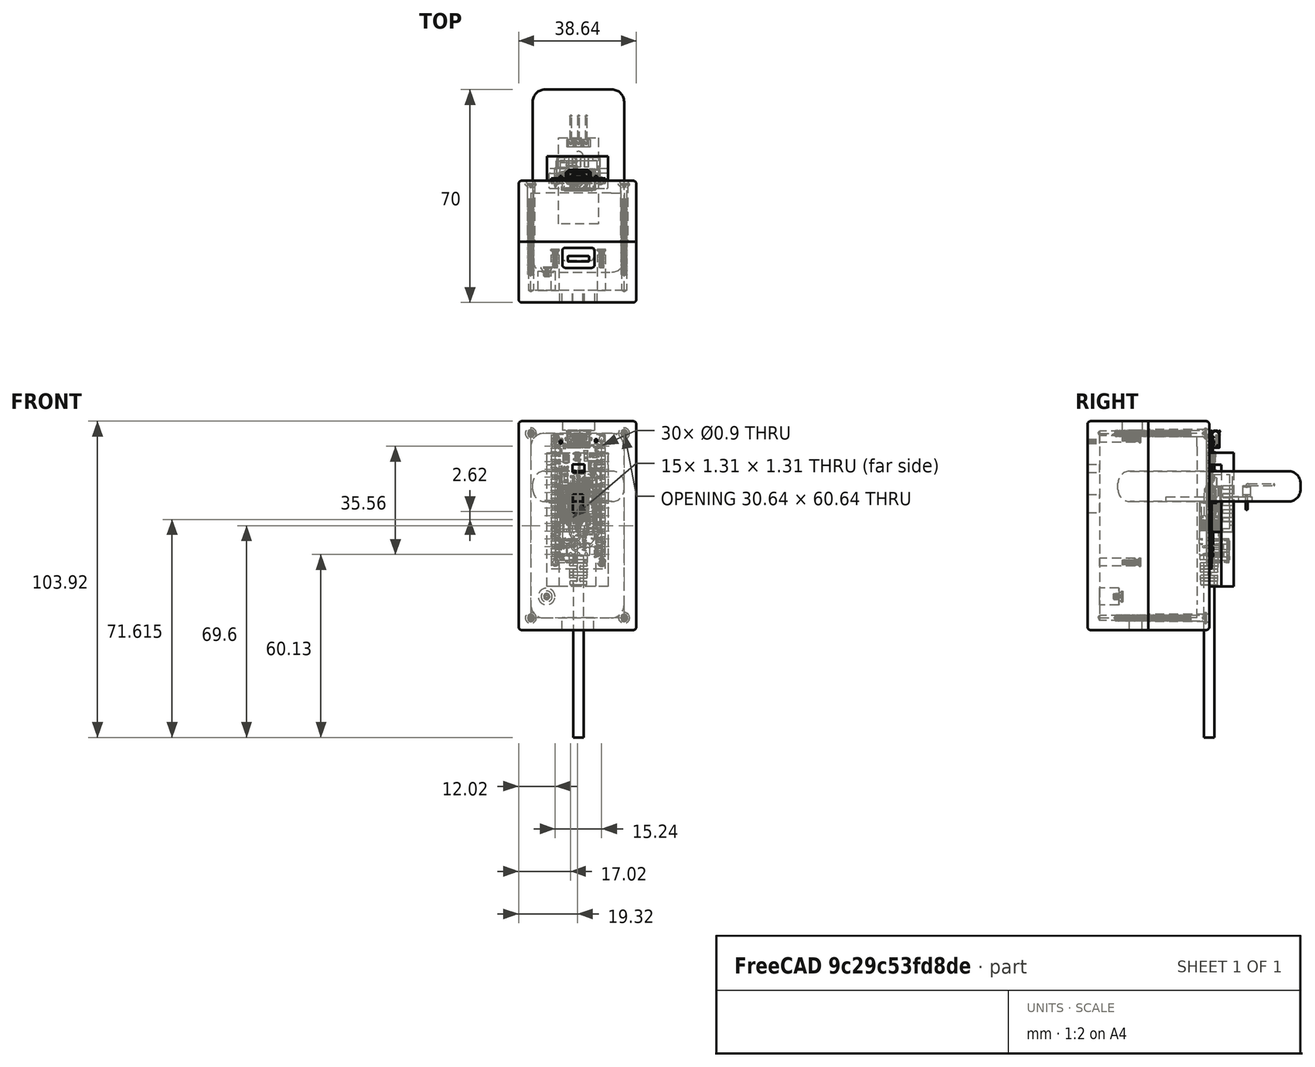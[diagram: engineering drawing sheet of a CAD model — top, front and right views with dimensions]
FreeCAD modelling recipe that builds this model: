
FCSTD DOCUMENT  (FreeCAD 1.0RUnknown)
Label: iot_assembly
License: All rights reserved
LicenseURL: https://en.wikipedia.org/wiki/All_rights_reserved
objects: TechDraw::DrawViewDimension×105, Part::Feature×69, Sketcher::SketchObject×21, App::FeaturePython×18, TechDraw::DrawProjGroupItem×18, App::Part×14, PartDesign::Pad×11, TechDraw::DrawViewDetail×10, TechDraw::DrawViewBalloon×9, Part::FeaturePython×7, PartDesign::SubShapeBinder×6, PartDesign::Pocket×6, PartDesign::Fillet×5, TechDraw::DrawViewSection×5, Spreadsheet::Sheet×4, PartDesign::Hole×4, Assembly::JointGroup×3, Assembly::AssemblyObject×3, PartDesign::Body×3, TechDraw::DrawSVGTemplate×3, +7 more types
note: 411 computed .brp shape members not serialized (recipe doc carries the construction recipe); baked Part::Feature solids carry a one-line shape summary decoded from their .brp

FEATURE [Part::Feature] Part__Feature  label="Nano_33IoT Body"
  shape: bbox 17.78 x 1.75 x 44 mm, 2561 faces (baked)
FEATURE [Part::Feature] Part__Feature001  label="User Library-arduino_nano_reset core"
  shape: bbox 5.209 x 2.159 x 2.809 mm, 76 faces (baked)
FEATURE [Part::Feature] Part__Feature002  label="User Library-arduino_nano_reset shell"
  Placement = pos=(1e-16,1.65,-1e-16) rot=(0,-1,0;1.5708rad)
  shape: bbox 4 x 1.65 x 3 mm, 71 faces (baked)
FEATURE [App::Part] Reser_Button  label="Reser Button"
  Group = -> [Part__Feature001,Part__Feature002]
  Origin = -> Origin001
  Placement = pos=(4.5e-15,0.8,10.91) rot=(0,0,1;0rad)
FEATURE [Part::Feature] Part__Feature003  label="atmegaSAMD21"
  Placement = pos=(-1.21,0.82,-0.24) rot=(0,1,0;1.5708rad)
  shape: bbox 7.242 x 1.032 x 7.242 mm, 984 faces (baked)
FEATURE [Part::Feature] Part__Feature004  label="HSMG-C190 LED"
  Placement = pos=(5.79,0.8,19.6) rot=(0,-1,0;1.5708rad)
  shape: bbox 0.8 x 0.8 x 1.6 mm, 18 faces (baked)
FEATURE [Part::Feature] Part__Feature005  label="HSMG-C190 LED001"
  Placement = pos=(-5.81,0.8,20.1) rot=(0,-1,0;1.5708rad)
  shape: bbox 0.8 x 0.8 x 1.6 mm, 18 faces (baked)
FEATURE [Part::Feature] Part__Feature006  label="ZX62-AB-5PA Micro USB"
  Placement = pos=(-4e-16,2.22,19.2) rot=(0,0,1;0rad)
  shape: bbox 8.814 x 3.085 x 5.639 mm, 861 faces (baked)
FEATURE [Part::Feature] Part__Feature007  label="ZX62-AB-5PA Micro USB001"
  Placement = pos=(-4e-16,2.22,19.2) rot=(0,0,1;0rad)
  shape: bbox 2e-07 x 0.3 x 0.3464 mm, 2 faces, 0 solids (baked)
FEATURE [Part::Feature] Part__Feature008  label="ZX62-AB-5PA Micro USB002"
  Placement = pos=(-4e-16,2.22,19.2) rot=(0,0,1;0rad)
  shape: bbox 2e-07 x 0.3 x 0.3464 mm, 2 faces, 0 solids (baked)
FEATURE [Part::Feature] Part__Feature009  label="ZX62-AB-5PA Micro USB003"
  Placement = pos=(-4e-16,2.22,19.2) rot=(0,0,1;0rad)
  shape: bbox 2e-07 x 0.3 x 0.3464 mm, 2 faces, 0 solids (baked)
FEATURE [Part::Feature] Part__Feature010  label="ZX62-AB-5PA Micro USB004"
  Placement = pos=(-4e-16,2.22,19.2) rot=(0,0,1;0rad)
  shape: bbox 2e-07 x 0.3 x 0.3464 mm, 2 faces, 0 solids (baked)
FEATURE [Part::Feature] Part__Feature011  label="ZX62-AB-5PA Micro USB005"
  Placement = pos=(-4e-16,2.22,19.2) rot=(0,0,1;0rad)
  shape: bbox 0.3 x 0.3 x 2e-07 mm, 1 faces, 0 solids (baked)
FEATURE [Part::Feature] Part__Feature012  label="ZX62-AB-5PA Micro USB006"
  Placement = pos=(-4e-16,2.22,19.2) rot=(0,0,1;0rad)
  shape: bbox 0.3 x 0.3 x 2e-07 mm, 1 faces, 0 solids (baked)
FEATURE [App::Part] ZX62_AB_5PA_Micro_USB  label="ZX62-AB-5PA Micro USB007"
  Group = -> [Part__Feature006,Part__Feature007,Part__Feature008,Part__Feature009,Part__Feature010,Part__Feature011,Part__Feature012]
  Origin = -> Origin002
FEATURE [Part::Feature] Part__Feature013  label="LSM6DS3 Accelerometer"
  Placement = pos=(4.6275,0.82,12) rot=(0,1,0;3.14159rad)
  shape: bbox 2.5 x 0.85 x 3 mm, 190 faces (baked)
FEATURE [Part::Feature] Part__Feature014  label="MPM3610 Step-Down Module"
  Placement = pos=(3.69,1.65,6.25) rot=(0,-1,0;1.5708rad)
  shape: bbox 5.15 x 1.65 x 3.3 mm, 330 faces (baked)
FEATURE [Part::Feature] Part__Feature015  label="NINA-W102 Body"
  shape: bbox 14 x 0.85 x 10 mm, 250 faces (baked)
FEATURE [Part::Feature] Part__Feature016  label="NINA-W102 Antenna"
  Placement = pos=(7,0.8,2.2e-15) rot=(0,0,1;0rad)
  shape: bbox 3.8 x 3 x 10 mm, 99 faces (baked)
FEATURE [Part::Feature] Part__Feature017  label="NINA-W102 Cover"
  Placement = pos=(-1.7,2,0) rot=(0,-1,0;1.5708rad)
  shape: bbox 9.6 x 1.45 x 9.5 mm, 75 faces (baked)
FEATURE [App::Part] NINA_W102_Module  label="NINA-W102 Module"
  Group = -> [Part__Feature015,Part__Feature016,Part__Feature017]
  Origin = -> Origin003
  Placement = pos=(2.17e-14,0.85,-14.5) rot=(0,1,0;1.5708rad)
FEATURE [Part::Feature] Part__Feature018  label="ATECC608A No Lead Crypto Auth"
  Placement = pos=(-4.035,0.8,-6.08) rot=(0,1,0;1.5708rad)
  shape: bbox 3.3 x 0.55 x 2 mm, 213 faces (baked)
FEATURE [Part::Feature] Part__Feature019  label="CL21A226MQCLQNC Capacitor"
  Placement = pos=(4.44,1.225,-5.85) rot=(0,1,0;3.14159rad)
  shape: bbox 3 x 0.8705 x 1.25 mm, 52 faces (baked)
FEATURE [Part::Feature] Part__Feature020  label="TDK C1005 Capacitor"
  Placement = pos=(5.5825,1.05,-15.55) rot=(0,1,0;1.5708rad)
  shape: bbox 0.5 x 0.5165 x 1.8 mm, 46 faces (baked)
FEATURE [Part::Feature] Part__Feature021  label="TDK C1005 Capacitor001"
  Placement = pos=(5.5825,1.05,-17.5125) rot=(0,1,0;1.5708rad)
  shape: bbox 0.5 x 0.5165 x 1.8 mm, 46 faces (baked)
FEATURE [Part::Feature] Part__Feature022  label="CL21A226MQCLQNC Capacitor001"
  Placement = pos=(-4.11,1.225,7.8375) rot=(0,-1,0;1.5708rad)
  shape: bbox 1.25 x 0.8705 x 3 mm, 52 faces (baked)
FEATURE [Part::Feature] Part__Feature023  label="TDK C1005 Capacitor002"
  Placement = pos=(5.385,1.05,15.7375) rot=(0,0,1;0rad)
  shape: bbox 1.8 x 0.5165 x 0.5 mm, 46 faces (baked)
FEATURE [Part::Feature] Part__Feature024  label="TDK C1005 Capacitor003"
  Placement = pos=(5.385,1.05,14.7625) rot=(0,0,1;0rad)
  shape: bbox 1.8 x 0.5165 x 0.5 mm, 46 faces (baked)
FEATURE [Part::Feature] Part__Feature025  label="PRTR5V0U2X Protection Diode"
  Placement = pos=(-0.41,1.45,14.77) rot=(0,1,0;1.5708rad)
  shape: bbox 2.5 x 1.1 x 3 mm, 139 faces (baked)
FEATURE [Part::Feature] Part__Feature026  label="PMEG6020AELR Diode"
  Placement = pos=(-4.06,0.85,14.1) rot=(0,-1,0;1.5708rad)
  shape: bbox 1.9 x 1.11 x 3.3 mm, 80 faces (baked)
FEATURE [Part::Feature] Part__Feature027  label="C0805C472KDRACTU Capacitor"
  Placement = pos=(2.415,1.425,15.1325) rot=(0,-1,0;1.5708rad)
  shape: bbox 1.25 x 1.301 x 3.5 mm, 52 faces (baked)
FEATURE [Part::Feature] Part__Feature028  label="TDK C1005 Capacitor004"
  Placement = pos=(-1.52,1.05,-6.46) rot=(0,1,0;1.5708rad)
  shape: bbox 0.5 x 0.5165 x 1.8 mm, 46 faces (baked)
FEATURE [Part::Feature] Part__Feature029  label="BLM18PG471SN1D Ferrite Bead"
  Placement = pos=(0.61,1.2,-6.1) rot=(0,1,0;3.14159rad)
  shape: bbox 2.5 x 0.8142 x 0.8 mm, 52 faces (baked)
FEATURE [Part::Feature] Part__Feature030  label="TDK C1005 Capacitor005"
  Placement = pos=(-5.66,1.05,-4.35) rot=(0,1,0;3.14159rad)
  shape: bbox 1.8 x 0.5165 x 0.5 mm, 46 faces (baked)
FEATURE [Part::Feature] Part__Feature031  label="TDK C1005 Capacitor006"
  Placement = pos=(-3.64,1.05,10.73) rot=(0,-1,0;1.5708rad)
  shape: bbox 0.5 x 0.5165 x 1.8 mm, 46 faces (baked)
FEATURE [Part::Feature] Part__Feature032  label="TDK C1005 Capacitor007"
  Placement = pos=(-3.79,1.05,5.1) rot=(0,0,1;0rad)
  shape: bbox 1.8 x 0.5165 x 0.5 mm, 46 faces (baked)
FEATURE [Part::Feature] Part__Feature033  label="GRM188R61E475KE11D Capacitor"
  Placement = pos=(-5.59,1.2,4.4) rot=(0,-1,0;1.5708rad)
  shape: bbox 0.8 x 0.8142 x 2.5 mm, 52 faces (baked)
FEATURE [Part::Feature] Part__Feature034  label="RC0402FR-07100KL Resistor"
  Placement = pos=(-2.01,1,8.1625) rot=(0,1,0;3.14159rad)
  shape: bbox 1.47 x 0.4379 x 0.5 mm, 68 faces (baked)
FEATURE [Part::Feature] Part__Feature035  label="RC0402FR-07100KL Resistor001"
  Placement = pos=(-1.6975,1,6.7125) rot=(0,-1,0;1.5708rad)
  shape: bbox 0.5 x 0.4379 x 1.47 mm, 68 faces (baked)
FEATURE [Part::Feature] Part__Feature036  label="RC0402FR-07330RL Resistor"
  Placement = pos=(-5.81,1,16.6) rot=(0,-1,0;1.5708rad)
  shape: bbox 0.5 x 0.4379 x 1.47 mm, 68 faces (baked)
FEATURE [Part::Feature] Part__Feature037  label="RC0402FR-07330RL Resistor001"
  Placement = pos=(5.8025,1,17.2) rot=(0,-1,0;1.5708rad)
  shape: bbox 0.5 x 0.4379 x 1.47 mm, 68 faces (baked)
FEATURE [Part::Feature] Part__Feature038  label="RC0402FR-07330RL Resistor002"
  Placement = pos=(3.915,1,15.2325) rot=(0,-1,0;1.5708rad)
  shape: bbox 0.5 x 0.4379 x 1.47 mm, 68 faces (baked)
FEATURE [Part::Feature] Part__Feature039  label="TDK C1005 Capacitor008"
  Placement = pos=(5.09,1.05,3.1) rot=(0,1,0;3.14159rad)
  shape: bbox 1.8 x 0.5165 x 0.5 mm, 46 faces (baked)
FEATURE [Part::Feature] Part__Feature040  label="RC0402FR-074K7L Resistor"
  Placement = pos=(5.09,1,2.1) rot=(0,0,1;0rad)
  shape: bbox 1.47 x 0.4379 x 0.5 mm, 68 faces (baked)
FEATURE [Part::Feature] Part__Feature041  label="RC0402FR-074K7L Resistor001"
  Placement = pos=(5.09,1,1.1) rot=(0,1,0;3.14159rad)
  shape: bbox 1.47 x 0.4379 x 0.5 mm, 68 faces (baked)
FEATURE [Part::Feature] Part__Feature042  label="GRM155R61E105KA12D Capacitor"
  Placement = pos=(5.09,1.05,0.1) rot=(0,0,1;0rad)
  shape: bbox 1.8 x 0.5165 x 0.5 mm, 46 faces (baked)
FEATURE [Part::Feature] Part__Feature043  label="TDK C1005 Capacitor009"
  Placement = pos=(5.09,1.05,-0.9) rot=(0,1,0;3.14159rad)
  shape: bbox 1.8 x 0.5165 x 0.5 mm, 46 faces (baked)
FEATURE [Part::Feature] Part__Feature044  label="RC0402FR-071KL Resistor"
  Placement = pos=(5.09,1,-1.9) rot=(0,1,0;3.14159rad)
  shape: bbox 1.47 x 0.4379 x 0.5 mm, 68 faces (baked)
FEATURE [Part::Feature] Part__Feature045  label="RC0402FR-07100KL Resistor002"
  Placement = pos=(-5.74,1,-13.5) rot=(0,1,0;1.5708rad)
  shape: bbox 0.5 x 0.4379 x 1.47 mm, 68 faces (baked)
FEATURE [Part::Feature] Part__Feature046  label="RC0402FR-07100KL Resistor003"
  Placement = pos=(-4.64,1,10.73) rot=(0,-1,0;1.5708rad)
  shape: bbox 0.5 x 0.4379 x 1.47 mm, 68 faces (baked)
FEATURE [Part::Feature] Part__Feature047  label="AC0402JR-0724KL Resistor"
  Placement = pos=(4.665,0.985,9.725) rot=(0,0,1;0rad)
  shape: bbox 1.47 x 0.4079 x 0.5 mm, 68 faces (baked)
FEATURE [Part::Feature] Part__Feature048  label="AC0402JR-0775KL Resistor"
  Placement = pos=(4.665,0.985,8.725) rot=(0,0,1;0rad)
  shape: bbox 1.47 x 0.4079 x 0.5 mm, 68 faces (baked)
FEATURE [App::Part] Arduino_Nano_33_IoT  label="Part_ArduinoNano33IoT"
  Group = -> [Part__Feature,Reser_Button,Part__Feature003,Part__Feature004,Part__Feature005,ZX62_AB_5PA_Micro_USB,Part__Feature013,Part__Feature014,NINA_W102_Module,Part__Feature018,Part__Feature019,Part__Feature020,Part__Feature021,Part__Feature022,Part__Feature023,Part__Feature024,Part__Feature025,Part__Feature026,Part__Feature027,Part__Feature028,Part__Feature029,Part__Feature030,Part__Feature031,+17 more]
  Origin = -> Origin004
  Placement = pos=(0,0,0) rot=(0,0,1;3.14159rad)
FEATURE [Part::Feature] Part__Feature049  label="Part_JST2PinConnector"
  Placement = pos=(-7.47,3.7,-16.1) rot=(0.707107,0.707107,0;3.14159rad)
  shape: bbox 7.466 x 8.736 x 7.806 mm, 204 faces (baked)
FEATURE [App::FeaturePython] GroundedJoint  # Assembly grounded joint (typed FeaturePython)
  ObjectToGround = -> Arduino_Nano_33_IoT
  Placement = pos=(0,0,0) rot=(0,0,1;3.14159rad)
FEATURE [App::FeaturePython] Joint  label="Fixed"  # Assembly joint (typed FeaturePython)
  Activated = true
  AngleMax = 0
  AngleMin = 0
  Detach1 = false
  Detach2 = false
  Distance = 0
  Distance2 = 0
  EnableAngleMax = false
  EnableAngleMin = false
  EnableLengthMax = false
  EnableLengthMin = false
  JointType = 0 (Fixed)
  LengthMax = 0
  LengthMin = 0
  Offset2 = pos=(0,0,-3) rot=(0,0,1;1.5708rad)
  Placement1 = pos=(7.62,-0.85,-14.83) rot=(-1,0,0;1.5708rad)
  Placement2 = pos=(-2.85,-0.15,-1.27) rot=(0.57735,-0.57735,-0.57735;2.0944rad)
  Reference1 = -> Assembly [Arduino_Nano_33_IoT.Part__Feature.Edge6193,Arduino_Nano_33_IoT.Part__Feature.Edge6193]
  Reference2 = -> Assembly [Part__Feature049.Face14,Part__Feature049.Face14]
FEATURE [Assembly::JointGroup] Joints
  Group = -> [GroundedJoint,Joint]
FEATURE [Assembly::AssemblyObject] Assembly  label="Assembly_PCB"
  Group = -> [Joints,Arduino_Nano_33_IoT,Part__Feature049,GroundedJoint,Joint]
  Origin = -> Origin
  Placement = pos=(-6.6e-15,-23.55,-1.3e-15) rot=(0,0,1;0rad)
  Type = Assembly
FEATURE [Sketcher::SketchObject] Sketch
  ArcFitTolerance = 1e-06
  AttachmentSupport = -> [XY_Plane008]
  FullyConstrained = true
  MakeInternals = false
  MapMode = 5
  expr: Constraints[8] = <<Spreadsheet_Battery>>.BatteryWidth
  expr: Constraints[9] = <<Spreadsheet_Battery>>.BatteryLength
  sketch-geometry (4):
    g0: LineSegment StartX=-15 StartY=30 StartZ=0 EndX=-15 EndY=-30 EndZ=0
    g1: LineSegment StartX=-15 StartY=-30 StartZ=0 EndX=15 EndY=-30 EndZ=0
    g2: LineSegment StartX=15 StartY=-30 StartZ=0 EndX=15 EndY=30 EndZ=0
    g3: LineSegment StartX=15 StartY=30 StartZ=0 EndX=-15 EndY=30 EndZ=0
  constraints (11):
    c: Coincident(g0,g1)
    c: Coincident(g1,g2)
    c: Coincident(g2,g3)
    c: Coincident(g3,g0)
    c: Vertical(g0)
    c: Vertical(g2)
    c: Horizontal(g1)
    c: Horizontal(g3)
    c: DistanceX(g3,g3) = 30
    c: DistanceY(g0,g0) = 60
    c: Symmetric(g0,g1,g-1)
FEATURE [Spreadsheet::Sheet] Spreadsheet  label="Spreadsheet_Battery"
  cells = A1='BatteryHeight; B1(BatteryHeight)==10 mm; A2='BatteryLength; B2(BatteryLength)==60 mm; A3='BatteryWidth; B3(BatteryWidth)==30 mm; A4='BatteryExpansionTolerancePercentage; B4(BatteryExpansionTolerancePercentage)=8
FEATURE [PartDesign::Pad] Pad
  Direction = (0,0,1)
  Length = 10
  Length2 = 10
  Profile = -> Sketch
  ReferenceAxis = -> Sketch [N_Axis]
  Refine = true
  Suppressed = false
  Type = 0
  expr: Length = <<Spreadsheet_Battery>>.BatteryHeight
FEATURE [PartDesign::Fillet] Fillet
  Base = -> Pad [Face6,Face5,Face4,Face1]
  BaseFeature = -> Pad
  Radius = 4
  Refine = true
  SupportTransform = false
  Suppressed = false
  UseAllEdges = true
FEATURE [PartDesign::Body] Body  label="Body_Battery"
  AllowCompound = false
  Group = -> [Sketch,Pad,Fillet]
  Origin = -> Origin008
  Tip = -> Fillet
FEATURE [App::Part] Part  label="Part_Battery"
  Group = -> [Body,Spreadsheet]
  Origin = -> Origin007
  Placement = pos=(-0.32,-4,-7.9) rot=(1,0,0;1.5708rad)
FEATURE [Spreadsheet::Sheet] Spreadsheet001  label="Spreadsheet_Enclosure"
  cells = A1='EnclosureWallThickness; B1(EnclosureWallThickness)==4 mm; A2='EnclosureBevel; B2(EnclosureBevel)==1 mm; A3='EnclosureWallThicknessTolerance; B3(EnclosureWallThicknessTolerance)==B1 * <<Spreadsheet_Battery>>.BatteryExpansionTolerancePercentage / 100; A4='EnclosureScrewHoles; B4(EnclosureScrewHoles)==2 mm; A5='EnclosureTopDepth; B5(EnclosureTopDepth)==20 mm; A6='EnclosureBottomDepth; B6(EnclosureBottomDepth)==20 mm; A7='EnclosureSlidingMechanismLength; B7(EnclosureSlidingMechanismLength)==40 mm; A8='EnclosureSlidingMechanismWidth; B8(EnclosureSlidingMechanismWidth)==20 mm; A9='EnclosureSlidingMechanismChannel; B9(EnclosureSlidingMechanismChannel)==4 mm; A10='EnclosureSlidingMechanismThickness; B10(EnclosureSlidingMechanismThickness)==B9; A11='EnclosureGasketChannelDiameter; B11(EnclosureGasketChannelDiameter)==2 mm
FEATURE [PartDesign::SubShapeBinder] Binder  label="Binder_Battery"
  BindCopyOnChange = 0
  BindMode = 0
  ClaimChildren = false
  Context = -> Assembly001 [Assembly002.Part001.Body001.Binder.]
  Fuse = false
  MakeFace = true
  OffsetFill = false
  OffsetIntersection = false
  OffsetJoinType = 0
  OffsetOpenResult = false
  PartialLoad = false
  Refine = true
  Relative = true
  Support = -> [Part]
  _Version = 2
FEATURE [Sketcher::SketchObject] Sketch001
  ArcFitTolerance = 1e-06
  AttachmentSupport = -> [XZ_Plane010]
  ExternalGeometry = -> [Binder]
  FullyConstrained = true
  MakeInternals = false
  MapMode = 5
  Placement = pos=(0,0,0) rot=(1,0,0;1.5708rad)
  expr: Constraints[10] = <<Spreadsheet_Enclosure>>.EnclosureWallThickness + <<Spreadsheet_Enclosure>>.EnclosureWallThicknessTolerance
  expr: Constraints[11] = <<Spreadsheet_Enclosure>>.EnclosureWallThickness + <<Spreadsheet_Enclosure>>.EnclosureWallThicknessTolerance
  expr: Constraints[8] = <<Spreadsheet_Enclosure>>.EnclosureWallThickness + <<Spreadsheet_Enclosure>>.EnclosureWallThicknessTolerance
  expr: Constraints[9] = <<Spreadsheet_Enclosure>>.EnclosureWallThickness + <<Spreadsheet_Enclosure>>.EnclosureWallThicknessTolerance
  sketch-geometry (4):
    g0: LineSegment StartX=-19.64 StartY=26.42 StartZ=0 EndX=-19.64 EndY=-42.22 EndZ=0
    g1: LineSegment StartX=-19.64 StartY=-42.22 StartZ=0 EndX=19 EndY=-42.22 EndZ=0
    g2: LineSegment StartX=19 StartY=-42.22 StartZ=0 EndX=19 EndY=26.42 EndZ=0
    g3: LineSegment StartX=19 StartY=26.42 StartZ=0 EndX=-19.64 EndY=26.42 EndZ=0
  constraints (12):
    c: Coincident(g0,g1)
    c: Coincident(g1,g2)
    c: Coincident(g2,g3)
    c: Coincident(g3,g0)
    c: Vertical(g0)
    c: Vertical(g2)
    c: Horizontal(g1)
    c: Horizontal(g3)
    c: Distance(g3,g-4) = 4.32
    c: Distance(g-10,g0) = 4.32
    c: Distance(g-6,g2) = 4.32
    c: Distance(g-8,g1) = 4.32
FEATURE [PartDesign::Pad] Pad001  label="EnclosureBottom"
  Direction = (0,-1,2e-16)
  Length = 20
  Length2 = 10
  Placement = pos=(0,0,0) rot=(1,0,0;1.5708rad)
  Profile = -> Sketch001
  ReferenceAxis = -> Sketch001 [N_Axis]
  Refine = true
  Suppressed = false
  Type = 0
  expr: Length = <<Spreadsheet_Enclosure>>.EnclosureBottomDepth
FEATURE [PartDesign::Thickness] Thickness  label="EnclosureWallThickness001"
  Base = -> Pad001 [Face6]
  BaseFeature = -> Pad001
  Intersection = false
  Join = 0
  Mode = 0
  Refine = true
  Reversed = true
  SupportTransform = false
  Suppressed = false
  Value = 4
  expr: Value = <<Spreadsheet_Enclosure>>.EnclosureWallThickness
FEATURE [Part::Feature] Part__Feature050  label="Right angle 3 pin header v1"
  Placement = pos=(3.85985,21.4856,5.86108) rot=(0,0,1;3.14159rad)
  shape: bbox 2.54 x 10.45 x 8.635 mm, 35 faces (baked)
FEATURE [Part::Feature] Part__Feature051  label="Right angle 3 pin header v002"
  Placement = pos=(3.85985,21.4856,5.86108) rot=(0,0,1;3.14159rad)
  shape: bbox 2.54 x 10.45 x 8.635 mm, 35 faces (baked)
FEATURE [Part::Feature] Part__Feature052  label="Right angle 3 pin header v003"
  Placement = pos=(3.85985,21.4856,5.86108) rot=(0,0,1;3.14159rad)
  shape: bbox 2.54 x 10.45 x 8.635 mm, 35 faces (baked)
FEATURE [App::Part] Right_angle_3_pin_header_v1  label="Right angle 3 pin header v004"
  Group = -> [Part__Feature050,Part__Feature051,Part__Feature052]
  Origin = -> Origin011
FEATURE [Part::Feature] Part__Feature053  label="dht22"
  shape: bbox 14.22 x 7.7 x 25.72 mm, 182 faces (baked)
FEATURE [App::Part] DHT22_v2  label="DHT22 v2"
  Group = -> [Part__Feature053]
  Origin = -> Origin012
  Placement = pos=(-0.011245,-7.07326,1.6615) rot=(0,0.707107,0.707107;3.14159rad)
FEATURE [Part::Feature] Part__Feature054  label="SOLID"
  shape: bbox 13 x 28.3 x 1.6 mm, 7 faces (baked)
FEATURE [App::Part] DHT22_Module_v3  label="Part_DHT22Modulev3"
  Group = -> [Right_angle_3_pin_header_v1,DHT22_v2,Part__Feature054]
  Origin = -> Origin013
  Placement = pos=(8.96326,-31.3615,-31.1776) rot=(0.57735,0.57735,0.57735;4.18879rad)
FEATURE [PartDesign::SubShapeBinder] Binder001  label="Binder_EnclosureBottom"
  BindCopyOnChange = 0
  BindMode = 0
  ClaimChildren = false
  Context = -> Assembly001 [Assembly002.Part002.Body002.Binder001.]
  Fuse = false
  MakeFace = true
  OffsetFill = false
  OffsetIntersection = false
  OffsetJoinType = 0
  OffsetOpenResult = false
  PartialLoad = false
  Refine = true
  Relative = true
  Support = -> [Part001]
  _Version = 2
FEATURE [Sketcher::SketchObject] Sketch002
  ArcFitTolerance = 1e-06
  AttachmentSupport = -> [Binder001]
  ExternalGeometry = -> [Binder001]
  FullyConstrained = true
  MakeInternals = false
  MapMode = 5
  Placement = pos=(0,-20,5.2e-15) rot=(1,0,0;1.5708rad)
  sketch-geometry (4):
    g0: LineSegment StartX=-19.64 StartY=26.42 StartZ=0 EndX=-19.64 EndY=-42.22 EndZ=0
    g1: LineSegment StartX=-19.64 StartY=-42.22 StartZ=0 EndX=19 EndY=-42.22 EndZ=0
    g2: LineSegment StartX=19 StartY=-42.22 StartZ=0 EndX=19 EndY=26.42 EndZ=0
    g3: LineSegment StartX=19 StartY=26.42 StartZ=0 EndX=-19.64 EndY=26.42 EndZ=0
  constraints (12):
    c: Coincident(g0,g1)
    c: Coincident(g1,g2)
    c: Coincident(g2,g3)
    c: Coincident(g3,g0)
    c: Vertical(g0)
    c: Vertical(g2)
    c: Horizontal(g1)
    c: Horizontal(g3)
    c: Horizontal(g0,g-4)
    c: Horizontal(g0,g-6)
    c: Vertical(g-5,g0)
    c: Vertical(g-7,g2)
FEATURE [PartDesign::Pad] Pad002  label="EnclosureTop"
  Direction = (0,-1,2e-16)
  Length = 20
  Length2 = 10
  Profile = -> Sketch002
  ReferenceAxis = -> Sketch002 [N_Axis]
  Refine = true
  Suppressed = false
  Type = 0
  expr: Length = <<Spreadsheet_Enclosure>>.EnclosureTopDepth
FEATURE [PartDesign::Thickness] Thickness001  label="EnclosureWallThickness"
  Base = -> Pad002 [Face5]
  BaseFeature = -> Pad002
  Intersection = false
  Join = 0
  Mode = 0
  Refine = true
  Reversed = true
  SupportTransform = false
  Suppressed = false
  Value = 4
  expr: Value = <<Spreadsheet_Enclosure>>.EnclosureWallThickness
FEATURE [PartDesign::SubShapeBinder] Binder002  label="Binder_ArduinoNano"
  BindCopyOnChange = 0
  BindMode = 0
  ClaimChildren = false
  Context = -> Assembly001 [Assembly002.Part002.Body002.Binder002.]
  Fuse = false
  MakeFace = true
  OffsetFill = false
  OffsetIntersection = false
  OffsetJoinType = 0
  OffsetOpenResult = false
  PartialLoad = false
  Refine = true
  Relative = true
  Support = -> [Assembly]
  _Version = 2
FEATURE [PartDesign::SubShapeBinder] Binder003  label="Binder_DHT22"
  BindCopyOnChange = 0
  BindMode = 0
  ClaimChildren = false
  Context = -> Assembly001 [Assembly002.Part002.Body002.Binder003.]
  Fuse = false
  MakeFace = true
  OffsetFill = false
  OffsetIntersection = false
  OffsetJoinType = 0
  OffsetOpenResult = false
  PartialLoad = false
  Refine = true
  Relative = true
  Support = -> [DHT22_Module_v3]
  _Version = 2
FEATURE [Sketcher::SketchObject] Sketch003
  ArcFitTolerance = 1e-06
  AttachmentSupport = -> [Thickness001,Binder002]
  ExternalGeometry = -> [Binder002]
  FullyConstrained = true
  MakeInternals = false
  MapMode = 5
  Placement = pos=(0,-36,9.4e-15) rot=(0,0.707107,0.707107;3.14159rad)
  sketch-geometry (4):
    g0: Circle CenterX=-7.62 CenterY=20.73 CenterZ=0 NormalX=0 NormalY=0 NormalZ=1 AngleXU=0 Radius=1.27
    g1: Circle CenterX=7.62 CenterY=20.73 CenterZ=0 NormalX=0 NormalY=0 NormalZ=1 AngleXU=0 Radius=1.27
    g2: Circle CenterX=-7.62 CenterY=-19.91 CenterZ=0 NormalX=0 NormalY=0 NormalZ=1 AngleXU=0 Radius=1.27
    g3: Circle CenterX=7.62 CenterY=-19.91 CenterZ=0 NormalX=0 NormalY=0 NormalZ=1 AngleXU=0 Radius=1.27
  constraints (8):
    c: Coincident(g0,g-3)
    c: Tangent(g0,g-7)
    c: Coincident(g1,g-13)
    c: Tangent(g1,g-5)
    c: Coincident(g2,g-12)
    c: Tangent(g2,g-11)
    c: Coincident(g3,g-8)
    c: Tangent(g3,g-9)
FEATURE [PartDesign::Pad] Pad003  label="PCBStandoffs"
  BaseFeature = -> Thickness001
  Direction = (0,1,-2e-16)
  Length = 10
  Length2 = 10
  Profile = -> Sketch003
  ReferenceAxis = -> Sketch003 [N_Axis]
  Refine = true
  Suppressed = false
  Type = 3
  UpToFace = -> Binder002 [Face2229]
FEATURE [Sketcher::SketchObject] Sketch004
  ArcFitTolerance = 1e-06
  AttachmentSupport = -> [Pad003]
  ExternalGeometry = -> [Binder002]
  FullyConstrained = true
  MakeInternals = false
  MapMode = 5
  Placement = pos=(0,-36,9.4e-15) rot=(0,0.707107,0.707107;3.14159rad)
  sketch-geometry (2):
    g0: Circle CenterX=-7.62 CenterY=20.73 CenterZ=0 NormalX=0 NormalY=0 NormalZ=1 AngleXU=0 Radius=0.8
    g1: Circle CenterX=7.62 CenterY=-19.91 CenterZ=0 NormalX=0 NormalY=0 NormalZ=1 AngleXU=0 Radius=0.8
  constraints (4):
    c: Coincident(g0,g-3)
    c: PointOnObject(g-3,g0)
    c: Coincident(g1,g-4)
    c: PointOnObject(g-4,g1)
FEATURE [PartDesign::Pad] Pad004  label="PCBPins"
  BaseFeature = -> Pad003
  Direction = (0,1,-2e-16)
  Length = 10
  Length2 = 10
  Profile = -> Sketch004
  ReferenceAxis = -> Sketch004 [N_Axis]
  Refine = true
  Suppressed = false
  Type = 3
  UpToFace = -> Binder002 [Face1966]
FEATURE [Sketcher::SketchObject] Sketch005
  ArcFitTolerance = 1e-06
  AttachmentSupport = -> [Pad004]
  ExternalGeometry = -> [Binder002]
  FullyConstrained = true
  MakeInternals = false
  MapMode = 5
  Placement = pos=(0,-24.35,0) rot=(0,0.707107,0.707107;3.14159rad)
  sketch-geometry (2):
    g0: Circle CenterX=-7.62 CenterY=-19.91 CenterZ=0 NormalX=0 NormalY=0 NormalZ=1 AngleXU=0 Radius=0.8
    g1: Circle CenterX=7.62 CenterY=20.73 CenterZ=0 NormalX=0 NormalY=0 NormalZ=1 AngleXU=0 Radius=0.8
  constraints (4):
    c: Coincident(g0,g-4)
    c: Equal(g0,g-4)
    c: Coincident(g1,g-3)
    c: Equal(g1,g-3)
FEATURE [PartDesign::Hole] Hole  label="PCBScrewHoles"
  BaseFeature = -> Pad004
  CustomThreadClearance = 0
  Depth = 2
  DepthType = 0
  Diameter = 0.75
  DrillForDepth = false
  DrillPoint = 1
  DrillPointAngle = 118
  HoleCutCountersinkAngle = 90
  HoleCutCustomValues = false
  HoleCutDepth = 0
  HoleCutDiameter = 6.1
  HoleCutType = 0
  ModelThread = false
  Profile = -> Sketch005
  Refine = true
  Suppressed = false
  Tapered = false
  TaperedAngle = 90
  ThreadClass = 0
  ThreadDepth = 2
  ThreadDepthType = 0
  ThreadDirection = 0
  ThreadFit = 0
  ThreadSize = 0
  ThreadType = 1
  Threaded = true
  UseCustomThreadClearance = false
FEATURE [Sketcher::SketchObject] Sketch006
  ArcFitTolerance = 1e-06
  AttachmentSupport = -> [Hole]
  ExternalGeometry = -> [Binder003]
  FullyConstrained = true
  MakeInternals = false
  MapMode = 5
  Placement = pos=(0,-36,9.4e-15) rot=(0,0.707107,0.707107;3.14159rad)
  sketch-geometry (1):
    g0: Circle CenterX=10.46 CenterY=-31.1889 CenterZ=0 NormalX=0 NormalY=0 NormalZ=1 AngleXU=0 Radius=2.75
  constraints (2):
    c: Coincident(g0,g-3)
    c: Tangent(g0,g-4)
FEATURE [PartDesign::Pad] Pad005  label="DHT22Standoff"
  BaseFeature = -> Hole
  Direction = (0,1,-2e-16)
  Length = 10
  Length2 = 10
  Profile = -> Sketch006
  ReferenceAxis = -> Sketch006 [N_Axis]
  Refine = true
  Suppressed = false
  Type = 3
  UpToFace = -> Binder003 [Face161]
FEATURE [Sketcher::SketchObject] Sketch007
  ArcFitTolerance = 1e-06
  AttachmentSupport = -> [Pad005]
  ExternalGeometry = -> [Binder003]
  FullyConstrained = true
  MakeInternals = false
  MapMode = 5
  Placement = pos=(0,-29.7,1.57e-14) rot=(0,0.707107,0.707107;3.14159rad)
  sketch-geometry (1):
    g0: Circle CenterX=10.46 CenterY=-31.1889 CenterZ=0 NormalX=0 NormalY=0 NormalZ=1 AngleXU=0 Radius=1.55
  constraints (2):
    c: Coincident(g0,g-3)
    c: PointOnObject(g-3,g0)
FEATURE [PartDesign::Hole] Hole001  label="DHT22ScrewHole"
  BaseFeature = -> Pad005
  CustomThreadClearance = 0
  Depth = 1
  DepthType = 0
  Diameter = 1.6
  DrillForDepth = false
  DrillPoint = 1
  DrillPointAngle = 118
  HoleCutCountersinkAngle = 90
  HoleCutCustomValues = false
  HoleCutDepth = 0
  HoleCutDiameter = 6.1
  HoleCutType = 0
  ModelThread = false
  Profile = -> Sketch007
  Refine = true
  Suppressed = false
  Tapered = false
  TaperedAngle = 90
  ThreadClass = 0
  ThreadDepth = 1
  ThreadDepthType = 0
  ThreadDirection = 0
  ThreadFit = 0
  ThreadSize = 6
  ThreadType = 1
  Threaded = true
  UseCustomThreadClearance = false
FEATURE [Sketcher::SketchObject] Sketch008
  ArcFitTolerance = 1e-06
  AttachmentSupport = -> [Hole001]
  ExternalGeometry = -> [Hole001,Binder003]
  FullyConstrained = true
  MakeInternals = false
  MapMode = 5
  Placement = pos=(0,-9.3e-15,-42.22) rot=(1,0,0;3.14159rad)
  sketch-geometry (4):
    g0: LineSegment StartX=-5.38001 StartY=26.2 StartZ=0 EndX=-5.38001 EndY=22 EndZ=0
    g1: LineSegment StartX=-5.38001 StartY=22 StartZ=0 EndX=5 EndY=22 EndZ=0
    g2: LineSegment StartX=5 StartY=22 StartZ=0 EndX=5 EndY=26.2 EndZ=0
    g3: LineSegment StartX=5 StartY=26.2 StartZ=0 EndX=-5.38001 EndY=26.2 EndZ=0
  constraints (12):
    c: Coincident(g0,g1)
    c: Coincident(g1,g2)
    c: Coincident(g2,g3)
    c: Coincident(g3,g0)
    c: Vertical(g0)
    c: Vertical(g2)
    c: Horizontal(g1)
    c: Horizontal(g3)
    c: Distance(g1,g-3) = 2
    c: Distance(g3,g-4) = 1
    c: Distance(g2,g-2) = 5
    c: Equal(g2,g0)
FEATURE [PartDesign::Pocket] Pocket  label="DHT22Opening"
  BaseFeature = -> Hole001
  Direction = (0,0,1)
  Length = 0
  Length2 = 5
  Profile = -> Sketch008
  ReferenceAxis = -> Sketch008 [N_Axis]
  Refine = true
  Suppressed = false
  Type = 2
FEATURE [Sketcher::SketchObject] Sketch009
  ArcFitTolerance = 1e-06
  AttachmentSupport = -> [Pocket]
  ExternalGeometry = -> [Binder002]
  FullyConstrained = true
  MakeInternals = false
  MapMode = 5
  Placement = pos=(0,5.8e-15,26.42) rot=(0,0,1;0rad)
  sketch-geometry (8):
    g0: LineSegment StartX=-3.25 StartY=-24.7 StartZ=0 EndX=3.25 EndY=-24.7 EndZ=0
    g1: LineSegment StartX=3.45 StartY=-24.9 StartZ=0 EndX=3.45 EndY=-26.35 EndZ=0
    g2: LineSegment StartX=-3.25 StartY=-26.55 StartZ=0 EndX=3.25 EndY=-26.55 EndZ=0
    g3: LineSegment StartX=-3.45 StartY=-26.35 StartZ=0 EndX=-3.45 EndY=-24.9 EndZ=0
    g4: ArcOfCircle CenterX=-3.25 CenterY=-24.9 CenterZ=0 NormalX=0 NormalY=0 NormalZ=1 AngleXU=0 Radius=0.2 StartAngle=1.5708 EndAngle=3.14159
    g5: ArcOfCircle CenterX=-3.25 CenterY=-26.35 CenterZ=0 NormalX=0 NormalY=0 NormalZ=1 AngleXU=0 Radius=0.2 StartAngle=3.14159 EndAngle=4.71239
    g6: ArcOfCircle CenterX=3.25 CenterY=-24.9 CenterZ=0 NormalX=0 NormalY=0 NormalZ=1 AngleXU=0 Radius=0.2 StartAngle=7.6e-15 EndAngle=1.5708
    g7: ArcOfCircle CenterX=3.25 CenterY=-26.35 CenterZ=0 NormalX=0 NormalY=0 NormalZ=1 AngleXU=0 Radius=0.2 StartAngle=4.71239 EndAngle=6.28319
  constraints (16):
    c: Coincident(g7,g-3)
    c: Tangent(g-3,g7) = -1.5708
    c: Tangent(g6,g-4) = -1.5708
    c: Coincident(g6,g-4)
    c: Coincident(g0,g6)
    c: Coincident(g7,g2)
    c: Coincident(g1,g6)
    c: Coincident(g7,g1)
    c: Coincident(g-6,g4)
    c: Tangent(g-6,g4) = -1.5708
    c: Coincident(g5,g-5)
    c: Tangent(g-5,g5) = -1.5708
    c: Coincident(g4,g0)
    c: Coincident(g5,g2)
    c: Coincident(g3,g4)
    c: Coincident(g5,g3)
FEATURE [PartDesign::Pocket] Pocket001  label="MicroUSBConnectorOpening"
  BaseFeature = -> Pocket
  Direction = (0,0,-1)
  Length = 4
  Length2 = 5
  Profile = -> Sketch009
  ReferenceAxis = -> Sketch009 [N_Axis]
  Refine = true
  Suppressed = false
  Type = 0
FEATURE [Part::Feature] Part__Feature055  label="Cable"
  shape: bbox 3.5 x 3.5 x 60 mm, 3 faces (baked)
FEATURE [Part::Feature] Part__Feature056  label="Micro_USB_Plug_Connector"
  shape: bbox 0.32 x 1.625 x 4.7 mm, 11 faces (baked)
FEATURE [Part::Feature] Part__Feature057  label="Micro_USB_Plug_Connector001"
  shape: bbox 6.35 x 1.35 x 7.5 mm, 54 faces (baked)
FEATURE [Part::Feature] Part__Feature058  label="Micro_USB_Plug_Connector002"
  shape: bbox 6.85 x 1.85 x 7.5 mm, 68 faces (baked)
FEATURE [Part::Feature] Part__Feature059  label="Micro_USB_Plug_Connector003"
  shape: bbox 0.32 x 1.625 x 4.574 mm, 11 faces (baked)
FEATURE [App::Part] Micro_USB_Plug_Connector  label="Micro_USB_Plug_Connector004"
  Group = -> [Part__Feature056,Part__Feature057,Part__Feature058,Part__Feature059]
  Origin = -> Origin016
FEATURE [Part::Feature] Part__Feature060  label="COMPOUND"
  shape: bbox 0.2 x 0.4672 x 4.78 mm, 14 faces (baked)
FEATURE [Part::Feature] Part__Feature061  label="COMPOUND001"
  shape: bbox 0.2 x 0.4672 x 4.78 mm, 14 faces (baked)
FEATURE [Part::Feature] Part__Feature062  label="COMPOUND002"
  shape: bbox 0.2 x 0.4672 x 4.78 mm, 14 faces (baked)
FEATURE [Part::Feature] Part__Feature063  label="COMPOUND003"
  shape: bbox 0.2 x 0.4672 x 4.78 mm, 14 faces (baked)
FEATURE [Part::Feature] Part__Feature064  label="COMPOUND004"
  shape: bbox 0.2 x 0.4672 x 4.78 mm, 14 faces (baked)
FEATURE [Part::Feature] Part__Feature065  label="COMPOUND005"
  shape: bbox 10.8 x 6.798 x 27.4 mm, 378 faces (baked)
FEATURE [App::Part] COMPOUND  label="COMPOUND006"
  Group = -> [Part__Feature060,Part__Feature061,Part__Feature062,Part__Feature063,Part__Feature064,Part__Feature065]
  Origin = -> Origin017
FEATURE [App::Part] Micro_USB_Plug_v10  label="Part_MicroUSBCable"
  Group = -> [Part__Feature055,Micro_USB_Plug_Connector,COMPOUND]
  Origin = -> Origin018
  Placement = pos=(0.025,-25.625,42.85) rot=(0,1,0;3.14159rad)
FEATURE [App::FeaturePython] Joint001  label="Slider"  # Assembly joint (typed FeaturePython)
  Activated = true
  AngleMax = 0
  AngleMin = 0
  Detach1 = false
  Detach2 = false
  Distance = 0
  Distance2 = 0
  EnableAngleMax = false
  EnableAngleMin = false
  EnableLengthMax = true
  EnableLengthMin = true
  JointType = 3 (Slider)
  LengthMax = -2.41
  LengthMin = -20
  Placement1 = pos=(-3.225,-0.925,2.25) rot=(0,1,0;3.14159rad)
  Placement2 = pos=(-3.25,0.78,1.4) rot=(0,1,0;3.14159rad)
  Reference1 = -> Assembly001 [Micro_USB_Plug_v10.Micro_USB_Plug_Connector.Part__Feature058.Edge133,Micro_USB_Plug_v10.Micro_USB_Plug_Connector.Part__Feature058.Edge133]
  Reference2 = -> Assembly001 [Assembly.Arduino_Nano_33_IoT.ZX62_AB_5PA_Micro_USB.Part__Feature006.Edge36,Assembly.Arduino_Nano_33_IoT.ZX62_AB_5PA_Micro_USB.Part__Feature006.Edge36]
FEATURE [PartDesign::SubShapeBinder] Binder004  label="Binder_MicroUSBCable"
  BindCopyOnChange = 0
  BindMode = 0
  ClaimChildren = false
  Context = -> Assembly001 [Assembly002.Part002.Body002.Binder004.]
  Fuse = false
  MakeFace = true
  OffsetFill = false
  OffsetIntersection = false
  OffsetJoinType = 0
  OffsetOpenResult = false
  PartialLoad = false
  Refine = true
  Relative = true
  Support = -> [Micro_USB_Plug_v10]
  _Version = 2
FEATURE [Sketcher::SketchObject] Sketch010
  ArcFitTolerance = 1e-06
  AttachmentSupport = -> [Pocket001]
  ExternalGeometry = -> [Pocket001]
  FullyConstrained = true
  MakeInternals = false
  MapMode = 5
  Placement = pos=(0,5.8e-15,26.42) rot=(0,0,1;0rad)
  sketch-geometry (4):
    g0: LineSegment StartX=5.3 StartY=-28.6 StartZ=0 EndX=-5.3 EndY=-28.6 EndZ=0
    g1: LineSegment StartX=5.3 StartY=-22 StartZ=0 EndX=5.3 EndY=-28.6 EndZ=0
    g2: LineSegment StartX=5.3 StartY=-22 StartZ=0 EndX=-5.3 EndY=-22 EndZ=0
    g3: LineSegment StartX=-5.3 StartY=-28.6 StartZ=0 EndX=-5.3 EndY=-22 EndZ=0
  constraints (12):
    c: Distance(g2,g0) = 6.6
    c: Distance(g1,g3) = 10.6
    c: Distance(g-3,g2) = 2
    c: Horizontal(g2)
    c: Horizontal(g0)
    c: Vertical(g1)
    c: Vertical(g3)
    c: Coincident(g1,g2)
    c: Coincident(g0,g1)
    c: Coincident(g3,g0)
    c: Coincident(g2,g3)
    c: Distance(g1,g-2) = 5.3
FEATURE [PartDesign::Pocket] Pocket002  label="MicroUSBConnectorBodyOpening"
  BaseFeature = -> Pocket001
  Direction = (0,0,-1)
  Length = 3
  Length2 = 5
  Profile = -> Sketch010
  ReferenceAxis = -> Sketch010 [N_Axis]
  Refine = true
  Suppressed = false
  Type = 0
FEATURE [PartDesign::Fillet] Fillet001  label="OpeningFillets"
  Base = -> Pocket002 [Edge33,Edge39,Edge35,Edge37,Edge25,Edge30,Edge28,Edge26]
  BaseFeature = -> Pocket002
  Radius = 1
  Refine = true
  SupportTransform = false
  Suppressed = false
  UseAllEdges = false
FEATURE [Sketcher::SketchObject] Sketch011
  ArcFitTolerance = 1e-06
  AttachmentSupport = -> [Fillet001]
  ExternalGeometry = -> [Binder002]
  FullyConstrained = true
  MakeInternals = false
  MapMode = 5
  Placement = pos=(0,-40,1.04e-14) rot=(1,0,0;1.5708rad)
  sketch-geometry (8):
    g0: LineSegment StartX=-6.14626 StartY=20.0563 StartZ=0 EndX=-6.14626 EndY=19.1437 EndZ=0
    g1: LineSegment StartX=-6.14626 StartY=19.1437 StartZ=0 EndX=-5.43374 EndY=19.1437 EndZ=0
    g2: LineSegment StartX=-5.43374 StartY=19.1437 StartZ=0 EndX=-5.43374 EndY=20.0563 EndZ=0
    g3: LineSegment StartX=-5.43374 StartY=20.0563 StartZ=0 EndX=-6.14626 EndY=20.0563 EndZ=0
    g4: LineSegment StartX=5.45374 StartY=20.5563 StartZ=0 EndX=5.45374 EndY=19.6437 EndZ=0
    g5: LineSegment StartX=5.45374 StartY=19.6437 StartZ=0 EndX=6.16626 EndY=19.6437 EndZ=0
    g6: LineSegment StartX=6.16626 StartY=19.6437 StartZ=0 EndX=6.16626 EndY=20.5563 EndZ=0
    g7: LineSegment StartX=6.16626 StartY=20.5563 StartZ=0 EndX=5.45374 EndY=20.5563 EndZ=0
  constraints (20):
    c: Coincident(g0,g1)
    c: Coincident(g1,g2)
    c: Coincident(g2,g3)
    c: Coincident(g3,g0)
    c: Vertical(g0)
    c: Vertical(g2)
    c: Horizontal(g1)
    c: Horizontal(g3)
    c: Coincident(g0,g-3)
    c: Coincident(g1,g-4)
    c: Coincident(g4,g5)
    c: Coincident(g5,g6)
    c: Coincident(g6,g7)
    c: Coincident(g7,g4)
    c: Vertical(g4)
    c: Vertical(g6)
    c: Horizontal(g5)
    c: Horizontal(g7)
    c: Coincident(g4,g-7)
    c: Coincident(g5,g-8)
FEATURE [PartDesign::Pocket] Pocket003  label="LEDHoles"
  BaseFeature = -> Fillet001
  Direction = (0,1,-2e-16)
  Length = 5
  Length2 = 5
  Profile = -> Sketch011
  ReferenceAxis = -> Sketch011 [N_Axis]
  Refine = true
  Suppressed = false
  Type = 1
FEATURE [PartDesign::Fillet] Fillet002  label="EnclosureFillet001"
  Base = -> Thickness [Edge1,Edge8,Edge5,Edge2,Edge3,Edge6,Edge9,Edge11]
  BaseFeature = -> Thickness
  Radius = 1
  Refine = true
  SupportTransform = false
  Suppressed = false
  UseAllEdges = false
  expr: Radius = <<Spreadsheet_Enclosure>>.EnclosureBevel
FEATURE [PartDesign::Fillet] Fillet003  label="EnclosureFillet"
  Base = -> Pocket003 [Edge12,Edge48,Edge29,Edge39,Edge31,Edge9,Edge38,Edge11]
  BaseFeature = -> Pocket003
  Radius = 1
  Refine = true
  SupportTransform = false
  Suppressed = false
  UseAllEdges = false
  expr: Radius = <<Spreadsheet_Enclosure>>.EnclosureBevel
FEATURE [Sketcher::SketchObject] Sketch012
  ArcFitTolerance = 1e-06
  AttachmentSupport = -> [Fillet002]
  ExternalGeometry = -> [Binder,Fillet002]
  FullyConstrained = true
  MakeInternals = false
  MapMode = 5
  Placement = pos=(0,-4,0) rot=(1,0,0;1.5708rad)
  expr: Constraints[14] = <<Spreadsheet_Enclosure>>.EnclosureWallThickness + <<Spreadsheet_Enclosure>>.EnclosureWallThicknessTolerance
  expr: Constraints[1] = <<Spreadsheet_Enclosure>>.EnclosureWallThickness + <<Spreadsheet_Enclosure>>.EnclosureWallThicknessTolerance
  expr: Constraints[20] = <<Spreadsheet_Enclosure>>.EnclosureWallThickness + <<Spreadsheet_Enclosure>>.EnclosureWallThicknessTolerance
  expr: Constraints[8] = <<Spreadsheet_Enclosure>>.EnclosureWallThickness + <<Spreadsheet_Enclosure>>.EnclosureWallThicknessTolerance
  sketch-geometry (12):
    g0: ArcOfCircle CenterX=-11.32 CenterY=18.1 CenterZ=0 NormalX=0 NormalY=0 NormalZ=1 AngleXU=0 Radius=4.32 StartAngle=1.5708 EndAngle=3.14159
    g1: LineSegment StartX=-15.64 StartY=22.42 StartZ=0 EndX=-15.64 EndY=18.1 EndZ=0
    g2: LineSegment StartX=-11.32 StartY=22.42 StartZ=0 EndX=-15.64 EndY=22.42 EndZ=0
    g3: ArcOfCircle CenterX=10.68 CenterY=18.1 CenterZ=0 NormalX=0 NormalY=0 NormalZ=1 AngleXU=0 Radius=4.32 StartAngle=8.06468e-08 EndAngle=1.5708
    g4: LineSegment StartX=15 StartY=22.42 StartZ=0 EndX=15 EndY=18.1 EndZ=0
    g5: LineSegment StartX=10.68 StartY=22.42 StartZ=0 EndX=15 EndY=22.42 EndZ=0
    g6: ArcOfCircle CenterX=10.68 CenterY=-33.9 CenterZ=0 NormalX=0 NormalY=0 NormalZ=1 AngleXU=0 Radius=4.32 StartAngle=4.71239 EndAngle=6.28319
    g7: LineSegment StartX=10.68 StartY=-38.22 StartZ=0 EndX=15 EndY=-38.22 EndZ=0
    g8: LineSegment StartX=15 StartY=-38.22 StartZ=0 EndX=15 EndY=-33.9 EndZ=0
    g9: LineSegment StartX=-15.64 StartY=-38.22 StartZ=0 EndX=-15.64 EndY=-33.9 EndZ=0
    g10: ArcOfCircle CenterX=-11.32 CenterY=-33.9 CenterZ=0 NormalX=0 NormalY=0 NormalZ=1 AngleXU=0 Radius=4.32 StartAngle=3.14159 EndAngle=4.71239
    g11: LineSegment StartX=-11.32 StartY=-38.22 StartZ=0 EndX=-15.64 EndY=-38.22 EndZ=0
  constraints (32):
    c: Coincident(g0,g-3)
    c: Radius(g0) = 4.32
    c: Coincident(g2,g1)
    c: Vertical(g1)
    c: Horizontal(g2)
    c: Coincident(g1,g-5)
    c: Coincident(g0,g2)
    c: Coincident(g0,g1)
    c: Radius(g3) = 4.32
    c: Coincident(g5,g4)
    c: Vertical(g4)
    c: Horizontal(g5)
    c: Coincident(g3,g5)
    c: Coincident(g3,g4)
    c: Radius(g10) = 4.32
    c: Coincident(g11,g9)
    c: Vertical(g9)
    c: Horizontal(g11)
    c: Coincident(g10,g11)
    c: Coincident(g10,g9)
    c: Radius(g6) = 4.32
    c: Coincident(g7,g8)
    c: Vertical(g8)
    c: Horizontal(g7)
    c: Coincident(g6,g7)
    c: Coincident(g6,g8)
    c: Coincident(g-6,g3)
    c: Coincident(g4,g-9)
    c: Coincident(g7,g-10)
    c: Coincident(g6,g-8)
    c: Coincident(g9,g-10)
    c: Coincident(g10,g-7)
FEATURE [PartDesign::Pad] Pad006  label="EnclosureReinforcement"
  BaseFeature = -> Fillet002
  Direction = (0,-1,2e-16)
  Length = 10
  Length2 = 10
  Profile = -> Sketch012
  ReferenceAxis = -> Sketch012 [N_Axis]
  Refine = true
  Suppressed = false
  Type = 3
  UpToFace = -> Fillet002 [Face2]
FEATURE [Sketcher::SketchObject] Sketch013
  ArcFitTolerance = 1e-06
  AttachmentSupport = -> [Pad006]
  ExternalGeometry = -> [Pad006]
  FullyConstrained = true
  MakeInternals = false
  MapMode = 5
  Placement = pos=(0,-1.8e-15,0) rot=(0,0.707107,0.707107;3.14159rad)
  expr: Constraints[0] = <<Spreadsheet_Enclosure>>.EnclosureScrewHoles
  expr: Constraints[3] = <<Spreadsheet_Enclosure>>.EnclosureScrewHoles
  expr: Constraints[6] = <<Spreadsheet_Enclosure>>.EnclosureScrewHoles
  expr: Constraints[7] = <<Spreadsheet_Enclosure>>.EnclosureScrewHoles
  sketch-geometry (4):
    g0: Circle CenterX=-15 CenterY=22.42 CenterZ=0 NormalX=0 NormalY=0 NormalZ=1 AngleXU=0 Radius=1
    g1: Circle CenterX=15.64 CenterY=22.42 CenterZ=0 NormalX=0 NormalY=0 NormalZ=1 AngleXU=0 Radius=1
    g2: Circle CenterX=-15 CenterY=-38.22 CenterZ=0 NormalX=0 NormalY=0 NormalZ=1 AngleXU=0 Radius=1
    g3: Circle CenterX=15.64 CenterY=-38.22 CenterZ=0 NormalX=0 NormalY=0 NormalZ=1 AngleXU=0 Radius=1
  constraints (12):
    c: Diameter(g0) = 2
    c: Vertical(g0,g-8)
    c: Horizontal(g-9,g0)
    c: Diameter(g1) = 2
    c: Horizontal(g-10,g1)
    c: Vertical(g-11,g1)
    c: Diameter(g2) = 2
    c: Diameter(g3) = 2
    c: Vertical(g3,g-12)
    c: Horizontal(g3,g-13)
    c: Vertical(g-14,g2)
    c: Horizontal(g2,g-14)
FEATURE [PartDesign::Hole] Hole002  label="EnclosureScrewHoles"
  BaseFeature = -> Pad006
  CustomThreadClearance = 0
  Depth = 25
  DepthType = 0
  Diameter = 2.4
  DrillForDepth = false
  DrillPoint = 1
  DrillPointAngle = 118
  HoleCutCountersinkAngle = 90
  HoleCutCustomValues = false
  HoleCutDepth = 0
  HoleCutDiameter = 6.1
  HoleCutType = 0
  ModelThread = false
  Profile = -> Sketch013
  Refine = true
  Suppressed = false
  Tapered = false
  TaperedAngle = 90
  ThreadClass = 0
  ThreadDepth = 25
  ThreadDepthType = 0
  ThreadDirection = 0
  ThreadFit = 0
  ThreadSize = 6
  ThreadType = 1
  Threaded = false
  UseCustomThreadClearance = false
FEATURE [PartDesign::Fillet] Fillet004  label="EnclosureScrewHolesFillet"
  Base = -> Hole002 [Edge41,Edge45,Edge63,Edge43]
  BaseFeature = -> Hole002
  Radius = 1
  Refine = true
  SupportTransform = false
  Suppressed = false
  UseAllEdges = false
FEATURE [Sketcher::SketchObject] Sketch014
  ArcFitTolerance = 1e-06
  AttachmentSupport = -> [Fillet003]
  ExternalGeometry = -> [Binder001,Fillet003]
  FullyConstrained = true
  MakeInternals = false
  MapMode = 5
  Placement = pos=(0,-36,9.4e-15) rot=(0,0.707107,0.707107;3.14159rad)
  expr: Constraints[11] = <<Spreadsheet_Enclosure>>.EnclosureWallThickness + <<Spreadsheet_Enclosure>>.EnclosureWallThicknessTolerance
  expr: Constraints[19] = <<Spreadsheet_Enclosure>>.EnclosureWallThickness + <<Spreadsheet_Enclosure>>.EnclosureWallThicknessTolerance
  expr: Constraints[23] = <<Spreadsheet_Enclosure>>.EnclosureWallThickness + <<Spreadsheet_Enclosure>>.EnclosureWallThicknessTolerance
  expr: Constraints[5] = <<Spreadsheet_Enclosure>>.EnclosureWallThickness + <<Spreadsheet_Enclosure>>.EnclosureWallThicknessTolerance
  sketch-geometry (12):
    g0: ArcOfCircle CenterX=-10.68 CenterY=18.1 CenterZ=0 NormalX=0 NormalY=0 NormalZ=1 AngleXU=0 Radius=4.32 StartAngle=1.5708 EndAngle=3.14159
    g1: LineSegment StartX=-15 StartY=18.1 StartZ=0 EndX=-15 EndY=22.42 EndZ=0
    g2: LineSegment StartX=-15 StartY=22.42 StartZ=0 EndX=-10.68 EndY=22.42 EndZ=0
    g3: ArcOfCircle CenterX=11.32 CenterY=18.1 CenterZ=0 NormalX=0 NormalY=0 NormalZ=1 AngleXU=0 Radius=4.32 StartAngle=3.58653e-06 EndAngle=1.5708
    g4: LineSegment StartX=15.64 StartY=18.1 StartZ=0 EndX=15.64 EndY=22.42 EndZ=0
    g5: LineSegment StartX=15.64 StartY=22.42 StartZ=0 EndX=11.32 EndY=22.42 EndZ=0
    g6: ArcOfCircle CenterX=-10.68 CenterY=-33.9 CenterZ=0 NormalX=0 NormalY=0 NormalZ=1 AngleXU=0 Radius=4.32 StartAngle=3.14159 EndAngle=4.71238
    g7: LineSegment StartX=-15 StartY=-38.22 StartZ=0 EndX=-10.68 EndY=-38.22 EndZ=0
    g8: LineSegment StartX=-15 StartY=-33.9 StartZ=0 EndX=-15 EndY=-38.22 EndZ=0
    g9: ArcOfCircle CenterX=11.32 CenterY=-33.9 CenterZ=0 NormalX=0 NormalY=0 NormalZ=1 AngleXU=0 Radius=4.32 StartAngle=4.71239 EndAngle=6.28319
    g10: LineSegment StartX=15.64 StartY=-38.22 StartZ=0 EndX=11.32 EndY=-38.22 EndZ=0
    g11: LineSegment StartX=15.64 StartY=-33.9 StartZ=0 EndX=15.64 EndY=-38.22 EndZ=0
  constraints (32):
    c: Coincident(g1,g2)
    c: Coincident(g-11,g1)
    c: Coincident(g0,g2)
    c: Coincident(g1,g0)
    c: Coincident(g-8,g0)
    c: Radius(g0) = 4.32
    c: Horizontal(g0,g-8)
    c: Vertical(g0,g-8)
    c: Coincident(g4,g5)
    c: Coincident(g3,g5)
    c: Coincident(g4,g3)
    c: Radius(g3) = 4.32
    c: Coincident(g3,g-12)
    c: Coincident(g4,g-14)
    c: Horizontal(g3,g-12)
    c: Vertical(g3,g-12)
    c: Coincident(g8,g7)
    c: Coincident(g6,g7)
    c: Coincident(g8,g6)
    c: Radius(g6) = 4.32
    c: Coincident(g11,g10)
    c: Coincident(g9,g10)
    c: Coincident(g11,g9)
    c: Radius(g9) = 4.32
    c: Coincident(g7,g-13)
    c: Coincident(g10,g-14)
    c: Coincident(g9,g-3)
    c: Vertical(g9,g-5)
    c: Horizontal(g-4,g9)
    c: Coincident(g-9,g6)
    c: Vertical(g6,g-9)
    c: Horizontal(g-9,g6)
FEATURE [PartDesign::Pad] Pad007  label="EnclosureReinforcements"
  BaseFeature = -> Fillet003
  Direction = (0,1,-2e-16)
  Length = 10
  Length2 = 10
  Profile = -> Sketch014
  ReferenceAxis = -> Sketch014 [N_Axis]
  Refine = true
  Suppressed = false
  Type = 3
  UpToFace = -> Fillet003 [Face2]
FEATURE [Sketcher::SketchObject] Sketch015
  ArcFitTolerance = 1e-06
  AttachmentSupport = -> [Pad007]
  ExternalGeometry = -> [Binder001]
  FullyConstrained = true
  MakeInternals = false
  MapMode = 5
  Placement = pos=(0,-20,5.2e-15) rot=(0,0.707107,0.707107;3.14159rad)
  sketch-geometry (4):
    g0: Circle CenterX=-15 CenterY=22.42 CenterZ=0 NormalX=0 NormalY=0 NormalZ=1 AngleXU=0 Radius=1.2
    g1: Circle CenterX=15.64 CenterY=22.42 CenterZ=0 NormalX=0 NormalY=0 NormalZ=1 AngleXU=0 Radius=1.2
    g2: Circle CenterX=15.64 CenterY=-38.22 CenterZ=0 NormalX=0 NormalY=0 NormalZ=1 AngleXU=0 Radius=1.2
    g3: Circle CenterX=-15 CenterY=-38.22 CenterZ=0 NormalX=0 NormalY=0 NormalZ=1 AngleXU=0 Radius=1.2
  constraints (8):
    c: Coincident(g0,g-3)
    c: Equal(g0,g-3)
    c: Coincident(g1,g-4)
    c: Equal(g1,g-4)
    c: Coincident(g2,g-5)
    c: Equal(g2,g-5)
    c: Coincident(g3,g-6)
    c: Equal(g3,g-6)
FEATURE [PartDesign::Hole] Hole003  label="EnclosureScrewHoles001"
  BaseFeature = -> Pad007
  CustomThreadClearance = 0
  Depth = 16
  DepthType = 0
  Diameter = 1.6
  DrillForDepth = false
  DrillPoint = 1
  DrillPointAngle = 118
  HoleCutCountersinkAngle = 90
  HoleCutCustomValues = false
  HoleCutDepth = 0
  HoleCutDiameter = 6.1
  HoleCutType = 0
  ModelThread = false
  Profile = -> Sketch015
  Refine = true
  Suppressed = false
  Tapered = false
  TaperedAngle = 90
  ThreadClass = 0
  ThreadDepth = 16
  ThreadDepthType = 0
  ThreadDirection = 0
  ThreadFit = 0
  ThreadSize = 6
  ThreadType = 1
  Threaded = true
  UseCustomThreadClearance = false
  expr: Depth = <<Spreadsheet_Enclosure>>.EnclosureTopDepth - <<Spreadsheet_Enclosure>>.EnclosureWallThickness
FEATURE [Sketcher::SketchObject] Sketch016
  ArcFitTolerance = 1e-06
  AttachmentSupport = -> [Hole003]
  ExternalGeometry = -> [Binder002]
  FullyConstrained = true
  MakeInternals = false
  MapMode = 5
  Placement = pos=(0,-40,1.04e-14) rot=(1,0,0;1.5708rad)
  sketch-geometry (4):
    g0: LineSegment StartX=-2 StartY=12.2 StartZ=0 EndX=-2 EndY=9.62 EndZ=0
    g1: LineSegment StartX=-2 StartY=9.62 StartZ=0 EndX=2 EndY=9.62 EndZ=0
    g2: LineSegment StartX=2 StartY=9.62 StartZ=0 EndX=2 EndY=12.2 EndZ=0
    g3: LineSegment StartX=2 StartY=12.2 StartZ=0 EndX=-2 EndY=12.2 EndZ=0
  constraints (10):
    c: Coincident(g0,g1)
    c: Coincident(g1,g2)
    c: Coincident(g2,g3)
    c: Coincident(g3,g0)
    c: Vertical(g0)
    c: Vertical(g2)
    c: Horizontal(g1)
    c: Horizontal(g3)
    c: Coincident(g0,g-6)
    c: Coincident(g1,g-5)
FEATURE [PartDesign::Pocket] Pocket004  label="ResetButtonHole"
  BaseFeature = -> Hole003
  Direction = (0,1,-2e-16)
  Length = 5
  Length2 = 5
  Profile = -> Sketch016
  ReferenceAxis = -> Sketch016 [N_Axis]
  Refine = true
  Suppressed = false
  Type = 1
FEATURE [Part::Feature] Part__Feature066  label="Housing"
  shape: bbox 19.5 x 6 x 5.395 mm, 54 faces (baked)
FEATURE [Part::Feature] Part__Feature067  label="Endplate"
  shape: bbox 11.25 x 5.5 x 2.9 mm, 102 faces (baked)
FEATURE [Part::Feature] Part__Feature068  label="Switch"
  shape: bbox 2.95 x 3.3 x 8.77 mm, 13 faces (baked)
FEATURE [App::Part] SP2T_Switch  label="Part_SP2TSwitch"
  Group = -> [Part__Feature066,Part__Feature067,Part__Feature068]
  Origin = -> Origin019
  Placement = pos=(-0.190858,-36,-0.64621) rot=(0.57735,-0.57735,0.57735;2.0944rad)
FEATURE [App::FeaturePython] Joint002  label="Fixed001"  # Assembly joint (typed FeaturePython)
  Activated = true
  AngleMax = 0
  AngleMin = 0
  Detach1 = false
  Detach2 = false
  Distance = 0
  Distance2 = 0
  EnableAngleMax = false
  EnableAngleMin = false
  EnableLengthMax = false
  EnableLengthMin = false
  JointType = 0 (Fixed)
  LengthMax = 0
  LengthMin = 0
  Placement1 = pos=(-0.190858,-36,-7.89621) rot=(0.57735,0.57735,0.57735;4.18879rad)
  Placement2 = pos=(-7.25,0,0) rot=(0,0,1;0rad)
  Reference1 = -> Assembly001 [Assembly002.Part002.Body002.Face50,Assembly002.Part002.Body002.Face50]
  Reference2 = -> Assembly001 [SP2T_Switch.Part__Feature066.Edge21,SP2T_Switch.Part__Feature066.Edge21]
FEATURE [PartDesign::SubShapeBinder] Binder005  label="Binder_SlideSwitch"
  BindCopyOnChange = 0
  BindMode = 0
  ClaimChildren = false
  Context = -> Assembly001 [Assembly002.Part002.Body002.Binder005.]
  Fuse = false
  MakeFace = true
  OffsetFill = false
  OffsetIntersection = false
  OffsetJoinType = 0
  OffsetOpenResult = false
  PartialLoad = false
  Refine = true
  Relative = true
  Support = -> [SP2T_Switch]
  _Version = 2
FEATURE [Sketcher::SketchObject] Sketch017
  ArcFitTolerance = 1e-06
  AttachmentSupport = -> [Pocket004]
  ExternalGeometry = -> [Binder005]
  FullyConstrained = true
  MakeInternals = false
  MapMode = 5
  Placement = pos=(0,-40,1.04e-14) rot=(1,0,0;1.5708rad)
  sketch-geometry (4):
    g0: LineSegment StartX=-1.89086 StartY=2.35379 StartZ=0 EndX=-1.89086 EndY=-3.64621 EndZ=0
    g1: LineSegment StartX=-1.89086 StartY=-3.64621 StartZ=0 EndX=1.50914 EndY=-3.64621 EndZ=0
    g2: LineSegment StartX=1.50914 StartY=-3.64621 StartZ=0 EndX=1.50914 EndY=2.35379 EndZ=0
    g3: LineSegment StartX=1.50914 StartY=2.35379 StartZ=0 EndX=-1.89086 EndY=2.35379 EndZ=0
  constraints (10):
    c: Coincident(g0,g1)
    c: Coincident(g1,g2)
    c: Coincident(g2,g3)
    c: Coincident(g3,g0)
    c: Vertical(g0)
    c: Vertical(g2)
    c: Horizontal(g1)
    c: Horizontal(g3)
    c: Coincident(g0,g-3)
    c: Coincident(g1,g-5)
FEATURE [PartDesign::Pocket] Pocket005  label="SlideSwitchHole"
  BaseFeature = -> Pocket004
  Direction = (0,1,-2e-16)
  Length = 15
  Length2 = 5
  Profile = -> Sketch017
  ReferenceAxis = -> Sketch017 [N_Axis]
  Refine = true
  Suppressed = false
  Type = 0
FEATURE [PartDesign::Body] Body002  label="Body_EnclosureTop"
  AllowCompound = false
  Group = -> [Binder001,Sketch002,Pad002,Thickness001,Binder002,Binder003,Sketch003,Pad003,Sketch004,Pad004,Sketch005,Hole,Sketch006,Pad005,Sketch007,Hole001,Sketch008,Pocket,Sketch009,Pocket001,Binder004,Sketch010,Pocket002,Fillet001,Sketch011,Pocket003,Fillet003,Sketch014,Pad007,Sketch015,Hole003,Sketch016,Pocket004,Binder005,Sketch017,Pocket005]
  Origin = -> Origin015
  Tip = -> Pocket005
FEATURE [App::Part] Part002  label="Part_EnclosureTop"
  Group = -> [Body002]
  Origin = -> Origin014
FEATURE [App::FeaturePython] Joint003  label="Fixed002"  # Assembly joint (typed FeaturePython)
  Activated = true
  AngleMax = 0
  AngleMin = 0
  Detach1 = false
  Detach2 = false
  Distance = 0
  Distance2 = 0
  EnableAngleMax = false
  EnableAngleMin = false
  EnableLengthMax = false
  EnableLengthMin = false
  JointType = 0 (Fixed)
  LengthMax = 0
  LengthMin = 0
  Offset2 = pos=(0,0,0) rot=(0,0,1;1.5708rad)
  Placement1 = pos=(7.62,-24.35,20.73) rot=(0,-0.707107,0.707107;3.14159rad)
  Placement2 = pos=(-7.62,0.8,20.73) rot=(-1,0,0;4.71239rad)
  Reference1 = -> Assembly001 [Assembly002.Part002.Body002.Edge219,Assembly002.Part002.Body002.Edge219]
  Reference2 = -> Assembly001 [Assembly.Arduino_Nano_33_IoT.Part__Feature.Edge6180,Assembly.Arduino_Nano_33_IoT.Part__Feature.Edge6180]
FEATURE [App::FeaturePython] Joint004  label="Fixed003"  # Assembly joint (typed FeaturePython)
  Activated = true
  AngleMax = 0
  AngleMin = 0
  Detach1 = false
  Detach2 = false
  Distance = 0
  Distance2 = 0
  EnableAngleMax = false
  EnableAngleMin = false
  EnableLengthMax = false
  EnableLengthMin = false
  JointType = 0 (Fixed)
  LengthMax = 0
  LengthMin = 0
  Offset2 = pos=(0,0,0) rot=(0,0,1;1.5708rad)
  Placement1 = pos=(-10.46,-29.7,-31.1889) rot=(-1,0,0;1.5708rad)
  Placement2 = pos=(0,0,-12.35) rot=(0.57735,-0.57735,0.57735;2.0944rad)
  Reference1 = -> Assembly001 [Assembly002.Part002.Body002.Edge220,Assembly002.Part002.Body002.Edge220]
  Reference2 = -> Assembly001 [DHT22_Module_v3.DHT22_v2.Part__Feature053.Edge489,DHT22_Module_v3.DHT22_v2.Part__Feature053.Edge489]
FEATURE [App::FeaturePython] Joint008  label="Fixed007"  # Assembly joint (typed FeaturePython)
  Activated = true
  AngleMax = 0
  AngleMin = 0
  Detach1 = false
  Detach2 = false
  Distance = 0
  Distance2 = 0
  EnableAngleMax = false
  EnableAngleMin = false
  EnableLengthMax = false
  EnableLengthMin = false
  JointType = 0 (Fixed)
  LengthMax = 0
  LengthMin = 0
  Offset2 = pos=(0,0,0) rot=(0,0,1;1.5708rad)
  Placement1 = pos=(-0.32,-4,-7.9) rot=(0.57735,0.57735,0.57735;4.18879rad)
  Placement2 = pos=(1.5e-15,-3.4e-15,0) rot=(0,0,1;1.5708rad)
  Reference1 = -> Assembly001 [Assembly002.Part001.Body001.Face41,Assembly002.Part001.Body001.Face41]
  Reference2 = -> Assembly001 [Part.Body.Face9,Part.Body.Face9]
FEATURE [Sketcher::SketchObject] Sketch018
  ArcFitTolerance = 1e-06
  AttachmentSupport = -> [Fillet004]
  ExternalGeometry = -> [Fillet004]
  FullyConstrained = true
  MakeInternals = false
  MapMode = 5
  Placement = pos=(0,-1.8e-15,0) rot=(0,0.707107,0.707107;3.14159rad)
  expr: Constraints[8] = <<Spreadsheet_Enclosure>>.EnclosureSlidingMechanismWidth - <<Spreadsheet_Enclosure>>.EnclosureSlidingMechanismThickness * 2
  expr: Constraints[9] = <<Spreadsheet_Enclosure>>.EnclosureSlidingMechanismLength
  sketch-geometry (9):
    g0: LineSegment StartX=-5.68 StartY=12.1 StartZ=0 EndX=-5.68 EndY=-27.9 EndZ=0
    g1: LineSegment StartX=-5.68 StartY=-27.9 StartZ=0 EndX=6.32 EndY=-27.9 EndZ=0
    g2: LineSegment StartX=6.32 StartY=-27.9 StartZ=0 EndX=6.32 EndY=12.1 EndZ=0
    g3: LineSegment StartX=6.32 StartY=12.1 StartZ=0 EndX=-5.68 EndY=12.1 EndZ=0
    g4: LineSegment [constr] StartX=-18 StartY=25.42 StartZ=0 EndX=-18 EndY=-41.22 EndZ=0
    g5: LineSegment [constr] StartX=-18 StartY=-41.22 StartZ=0 EndX=18.64 EndY=-41.22 EndZ=0
    g6: LineSegment [constr] StartX=18.64 StartY=-41.22 StartZ=0 EndX=18.64 EndY=25.42 EndZ=0
    g7: LineSegment [constr] StartX=18.64 StartY=25.42 StartZ=0 EndX=-18 EndY=25.42 EndZ=0
    g8: GeomPoint [constr] X=0.32 Y=-7.9 Z=0
  constraints (22):
    c: Coincident(g0,g1)
    c: Coincident(g1,g2)
    c: Coincident(g2,g3)
    c: Coincident(g3,g0)
    c: Vertical(g0)
    c: Vertical(g2)
    c: Horizontal(g1)
    c: Horizontal(g3)
    c: DistanceX(g3,g3) = 12
    c: DistanceY(g0,g0) = 40
    c: Coincident(g4,g5)
    c: Coincident(g5,g6)
    c: Coincident(g6,g7)
    c: Coincident(g7,g4)
    c: Vertical(g4)
    c: Vertical(g6)
    c: Horizontal(g5)
    c: Horizontal(g7)
    c: Coincident(g4,g-3)
    c: Coincident(g5,g-4)
    c: Symmetric(g5,g4,g8)
    c: Symmetric(g0,g1,g8)
FEATURE [PartDesign::Pad] Pad008  label="EnclosureSlidingMechanismSupport"
  BaseFeature = -> Fillet004
  Direction = (0,1,-2e-16)
  Length = 4
  Length2 = 10
  Profile = -> Sketch018
  ReferenceAxis = -> Sketch018 [N_Axis]
  Refine = true
  Suppressed = false
  Type = 0
  expr: Length = <<Spreadsheet_Enclosure>>.EnclosureSlidingMechanismThickness
FEATURE [Sketcher::SketchObject] Sketch019
  ArcFitTolerance = 1e-06
  AttachmentSupport = -> [Pad008]
  ExternalGeometry = -> [Pad008]
  FullyConstrained = true
  MakeInternals = false
  MapMode = 5
  Placement = pos=(0,4,0) rot=(0,0.707107,0.707107;3.14159rad)
  expr: Constraints[8] = <<Spreadsheet_Enclosure>>.EnclosureSlidingMechanismWidth
  expr: Constraints[9] = <<Spreadsheet_Enclosure>>.EnclosureSlidingMechanismLength
  sketch-geometry (9):
    g0: LineSegment StartX=-9.68 StartY=12.1 StartZ=0 EndX=-9.68 EndY=-27.9 EndZ=0
    g1: LineSegment StartX=-9.68 StartY=-27.9 StartZ=0 EndX=10.32 EndY=-27.9 EndZ=0
    g2: LineSegment StartX=10.32 StartY=-27.9 StartZ=0 EndX=10.32 EndY=12.1 EndZ=0
    g3: LineSegment StartX=10.32 StartY=12.1 StartZ=0 EndX=-9.68 EndY=12.1 EndZ=0
    g4: LineSegment [constr] StartX=-18 StartY=25.42 StartZ=0 EndX=-18 EndY=-41.22 EndZ=0
    g5: LineSegment [constr] StartX=-18 StartY=-41.22 StartZ=0 EndX=18.64 EndY=-41.22 EndZ=0
    g6: LineSegment [constr] StartX=18.64 StartY=-41.22 StartZ=0 EndX=18.64 EndY=25.42 EndZ=0
    g7: LineSegment [constr] StartX=18.64 StartY=25.42 StartZ=0 EndX=-18 EndY=25.42 EndZ=0
    g8: GeomPoint [constr] X=0.32 Y=-7.9 Z=0
  constraints (22):
    c: Coincident(g0,g1)
    c: Coincident(g1,g2)
    c: Coincident(g2,g3)
    c: Coincident(g3,g0)
    c: Vertical(g0)
    c: Vertical(g2)
    c: Horizontal(g1)
    c: Horizontal(g3)
    c: DistanceX(g3,g3) = 20
    c: DistanceY(g0,g0) = 40
    c: Coincident(g4,g5)
    c: Coincident(g5,g6)
    c: Coincident(g6,g7)
    c: Coincident(g7,g4)
    c: Vertical(g4)
    c: Vertical(g6)
    c: Horizontal(g5)
    c: Horizontal(g7)
    c: Coincident(g4,g-3)
    c: Coincident(g5,g-4)
    c: Symmetric(g4,g5,g8)
    c: Symmetric(g1,g0,g8)
FEATURE [PartDesign::Pad] Pad009  label="EnclosureSlidingMechanismSupportMaleChannel"
  BaseFeature = -> Pad008
  Direction = (0,1,-2e-16)
  Length = 4
  Length2 = 10
  Profile = -> Sketch019
  ReferenceAxis = -> Sketch019 [N_Axis]
  Refine = true
  Suppressed = false
  Type = 0
  expr: Length = <<Spreadsheet_Enclosure>>.EnclosureSlidingMechanismChannel
FEATURE [Sketcher::SketchObject] Sketch020
  ArcFitTolerance = 1e-06
  AttachmentSupport = -> [Pad009]
  ExternalGeometry = -> [Pad009]
  FullyConstrained = true
  MakeInternals = false
  MapMode = 5
  Placement = pos=(0,0,12.1) rot=(0,0,1;0rad)
  sketch-geometry (4):
    g0: LineSegment StartX=-10.32 StartY=8 StartZ=0 EndX=-10.32 EndY=0 EndZ=0
    g1: LineSegment StartX=-10.32 StartY=0 StartZ=0 EndX=9.68 EndY=0 EndZ=0
    g2: LineSegment StartX=9.68 StartY=0 StartZ=0 EndX=9.68 EndY=8 EndZ=0
    g3: LineSegment StartX=9.68 StartY=8 StartZ=0 EndX=-10.32 EndY=8 EndZ=0
  constraints (11):
    c: Coincident(g0,g1)
    c: Coincident(g1,g2)
    c: Coincident(g2,g3)
    c: Coincident(g3,g0)
    c: Vertical(g0)
    c: Vertical(g2)
    c: Horizontal(g1)
    c: Horizontal(g3)
    c: Coincident(g0,g-3)
    c: Vertical(g1,g-4)
    c: Horizontal(g1,g-1)
FEATURE [PartDesign::Pad] Pad010  label="EnclosureSlidingMechanismStop"
  BaseFeature = -> Pad009
  Direction = (0,0,1)
  Length = 4
  Length2 = 10
  Profile = -> Sketch020
  ReferenceAxis = -> Sketch020 [N_Axis]
  Refine = true
  Suppressed = false
  Type = 0
  expr: Length = <<Spreadsheet_Enclosure>>.EnclosureSlidingMechanismThickness
FEATURE [PartDesign::Body] Body001  label="Body_EnclosureBottom"
  AllowCompound = false
  Group = -> [Binder,Sketch001,Pad001,Thickness,Fillet002,Sketch012,Pad006,Sketch013,Hole002,Fillet004,Sketch018,Pad008,Sketch019,Pad009,Sketch020,Pad010]
  Origin = -> Origin010
  Tip = -> Pad010
FEATURE [App::Part] Part001  label="Part_EnclosureBottom"
  Group = -> [Body001]
  Origin = -> Origin009
FEATURE [App::FeaturePython] GroundedJoint002  # Assembly grounded joint (typed FeaturePython)
  ObjectToGround = -> Part001
FEATURE [Assembly::JointGroup] Joints002
  Group = -> [GroundedJoint002]
FEATURE [Spreadsheet::Sheet] Spreadsheet002  label="Spreadsheet_Assembly_BoM"
  cells = A1='Index; B1='Item; C1='Description; D1='Quantity; E1='Material; G1='Source; H1='Link; I1='Source Min. Order Limit; J1='Price / Source Min. Order Limit; K1='Price / Quantity ($USD); L1='Cost Without Shipping($USD); E2='Name; F2='Density(g/cm^3); A3=1; B3='Assembly_PCB; C3='Arduino Nano 33 IoT with Soldered JST Connector (VIN, GND); A4=1.1; B4='Arduino Nano 33 IoT; C4='Without Soldered Headers; D4=1; G4='Arduino; H4='https://store-usa.arduino.cc/products/arduino-nano-33-iot; I4=1; J4=23.9; K4==J4 / I4; L4==D4 * K4; A5=1.2; B5='2 Pin JST Female Connector; C5='90 Deg. Connector; D5=1; G5='Aliexpress; <blob elided: 513 chars, md5=f0ea656a> I5=10; J5=0.81; K5==J5 / I5; L5==D5 * K5; A6=2; B6='Assembly_Enclosure; C6='2 Piece 3D Printed Assembly with Gaskets; A7=2.1; B7='Enclosure Top; D7==<<Body_EnclosureTop>>.Shape.Volume; E7='ASA; F7==(1.07 + 1.24) / 2; G7='eSun; H7='https://www.aliexpress.us/item/3256804784111067.html?gatewayAdapt=4itemAdapt; I7=1; J7=24.31; K7==J7 / 1000 / I7; L7==D7 / 1000 * F7 * K7; A8=2.2; B8='Enclosure Bottom; D8==<<Body_EnclosureBottom>>.Shape.Volume; L8==D8 / 1000 * F7 * K7; A9=2.3; B9='M2x30-Screw; C9='ISO 7046 Phillips Head Screws - Threaded Along Half of Shaft; D9=4; E9='Black Carbon Steel; G9='Aliexpress; <blob elided: 626 chars, md5=40afeb43> I9=50; J9=3.66; K9==J9 / I9; L9==D9 * K9; A10=3; B10='DHT22 Module; D10=1; <blob elided: 563 chars, md5=ca1bc7dd> I10=1; J10=0.99; K10==J10 / I10; L10==D10 * K10; A11=4; B11='103060 LiPo Battery; C11='103060 3.7V With JST Male Connector; D11=1; E11='Lithium Polymer; G11='Alibaba; H11='https://www.alibaba.com/product-detail/DTP-103060-Lipo-Battery-3-7v_1600384790776.html; I11=5; J11=2.2; K11==J11 / I11; L11==D11 * K11; A12=6; B12='M1.6x6-Screw; C12='ISO 7046 Phillips Countersunk Head Screws; D12=2; E12='Black Carbon Steel; G12='Aliexpress; <blob elided: 627 chars, md5=db507b46> I12=100; J12=2.33; K12==J12 / I12; L12==D12 * K12; A13=5; B13='M2x3-Screw; D13=1; <blob elided: 627 chars, md5=3b50e64d> I13=50; J13=1.2; K13==J13 / I13; L13==D13 * K13; A14='Sub-Total ($USD); L14(SubTotal)==sum(L2:L13); A15='Contingency (%); L15(Contingency)=10; A16='Total ($USD); L16==SubTotal + SubTotal * Contingency / 100
FEATURE [Part::FeaturePython] Screw005  label="M1.6x6-Screw001"  # WARN: FeaturePython — macro-defined, semantics opaque (R4)
  BaseObject = -> Assembly [Arduino_Nano_33_IoT.Part__Feature.Edge5499]
  Diameter = 1
  Invert = true
  LeftHanded = false
  Length = 3
  LengthCustom = 6
  MatchOuter = false
  Offset = 0.2
  OffsetAngle = 0
  Placement = pos=(-7.62,-22.55,20.73) rot=(-1,0,0;1.5708rad)
  Thread = true
  Type = 78
FEATURE [Part::FeaturePython] Screw  label="M2x3-Screw"  # WARN: FeaturePython — macro-defined, semantics opaque (R4)
  BaseObject = -> DHT22_Module_v3 [DHT22_v2.Part__Feature053.Edge484]
  Diameter = 2
  Invert = false
  LeftHanded = false
  Length = 0
  LengthCustom = 3
  MatchOuter = false
  OffsetAngle = 0
  Placement = pos=(-10.46,-28.4,-31.1889) rot=(-1,0,0;1.5708rad)
  Thread = true
  Type = 78
FEATURE [Part::FeaturePython] Screw006  label="M2x30-Screw"  # WARN: FeaturePython — macro-defined, semantics opaque (R4)
  BaseObject = -> Part001 [Body001.Pad010.Edge77]
  Diameter = 2
  Invert = false
  LeftHanded = false
  Length = 10
  LengthCustom = 30
  MatchOuter = true
  OffsetAngle = 0
  Placement = pos=(15,-1,-38.22) rot=(-1,0,0;1.5708rad)
  Thread = true
  Type = 78
FEATURE [Part::FeaturePython] Screw007  label="M2x30-Screw061"  # WARN: FeaturePython — macro-defined, semantics opaque (R4)
  BaseObject = -> Part001 [Body001.Pad010.Edge57]
  Diameter = 2
  Invert = false
  LeftHanded = false
  Length = 10
  LengthCustom = 30
  MatchOuter = true
  OffsetAngle = 0
  Placement = pos=(-15.64,-1,-38.22) rot=(-1,0,0;1.5708rad)
  Thread = true
  Type = 78
FEATURE [Part::FeaturePython] Screw008  label="M2x30-Screw062"  # WARN: FeaturePython — macro-defined, semantics opaque (R4)
  BaseObject = -> Part001 [Body001.Pad010.Edge2]
  Diameter = 2
  Invert = false
  LeftHanded = false
  Length = 10
  LengthCustom = 30
  MatchOuter = true
  OffsetAngle = 0
  Placement = pos=(-15.64,-1,22.42) rot=(-1,0,0;1.5708rad)
  Thread = true
  Type = 78
FEATURE [Part::FeaturePython] Screw009  label="M2x30-Screw063"  # WARN: FeaturePython — macro-defined, semantics opaque (R4)
  BaseObject = -> Part001 [Body001.Pad010.Edge59]
  Diameter = 2
  Invert = false
  LeftHanded = false
  Length = 10
  LengthCustom = 30
  MatchOuter = true
  OffsetAngle = 0
  Placement = pos=(15,-1,22.42) rot=(-1,0,0;1.5708rad)
  Thread = true
  Type = 78
FEATURE [Assembly::AssemblyObject] Assembly002  label="Assembly_Enclosure"
  Group = -> [Joints002,Spreadsheet001,Part002,Part001,GroundedJoint002,Screw006,Screw007,Screw008,Screw009]
  Origin = -> Origin006
  Type = Assembly
FEATURE [App::FeaturePython] GroundedJoint001  # Assembly grounded joint (typed FeaturePython)
  ObjectToGround = -> Assembly002
FEATURE [Assembly::JointGroup] Joints001
  Group = -> [GroundedJoint001,Joint001,Joint002,Joint003,Joint004,Joint008]
FEATURE [Part::FeaturePython] Screw010  label="M1.6x6-Screw"  # WARN: FeaturePython — macro-defined, semantics opaque (R4)
  BaseObject = -> Assembly [Arduino_Nano_33_IoT.Part__Feature.Edge5496]
  Diameter = 1
  Invert = true
  LeftHanded = false
  Length = 3
  LengthCustom = 6
  MatchOuter = false
  Offset = 0.2
  OffsetAngle = 0
  Placement = pos=(7.62,-22.55,-19.91) rot=(-1,0,0;1.5708rad)
  Thread = true
  Type = 78
FEATURE [TechDraw::DrawSVGTemplate] Template
  EditableTexts = creator=Peter; date_of_issue=8/13/25; document_type=Assembly Drawing; general_tolerances=ISO 2768-m; identification_number=DN; language_code=EN; legal_owner_2=Orbtronics; part_material=Polycarbonate/ASA Alloy; scale=1 : 1; sheet_number=1 / 3; title=IoT Device Assembly
  Height = 297
  Orientation = 1
  Template = <userpath>/projects/.interviews/orbtronics/l1-mechatronics-engineer/cad/assets/templates/A3_Landscape_ISO5457_minimal_third-angle.svg
  Width = 420
FEATURE [TechDraw::DrawSVGTemplate] Template001
  EditableTexts = creator=Peter; date_of_issue=8/13/25; document_type=Component Drawing; general_tolerances=ISO 2768-m; identification_number=DN; language_code=EN; legal_owner_2=Orbtronics; part_material=Polycarbonate/ASA Alloy; revision_index=AAA; scale=1 : 1; sheet_number=2 / 3; title=IoT Device Assembly
  Height = 297
  Orientation = 1
  Template = <userpath>/projects/.interviews/orbtronics/l1-mechatronics-engineer/cad/assets/templates/A3_Landscape_ISO5457_minimal_third-angle.svg
  Width = 420
FEATURE [TechDraw::DrawProjGroupItem] View002  label="Front002"
  Caption = Front
  CoarseView = false
  Direction = (0,-1,0)
  Focus = 100
  HardHidden = false
  IsoCount = 0
  IsoHidden = false
  IsoVisible = false
  LockPosition = true
  Perspective = false
  Rotation = 0
  RotationVector = (1,0,0)
  ScaleType = 2
  ScrubCount = 1
  SeamHidden = false
  SeamVisible = false
  SmoothHidden = false
  SmoothVisible = true
  Source = -> [Part002]
  Type = 0
  X = 0
  XDirection = (1,0,0)
  Y = 0
FEATURE [TechDraw::DrawProjGroupItem] ProjItem006  label="Right002"
  Caption = Right Side
  CoarseView = false
  Direction = (1,-1e-16,0)
  Focus = 100
  HardHidden = false
  IsoCount = 0
  IsoHidden = false
  IsoVisible = false
  LockPosition = false
  Perspective = false
  Rotation = 0
  RotationVector = (1,0,0)
  ScaleType = 0
  ScrubCount = 1
  SeamHidden = false
  SeamVisible = false
  SmoothHidden = false
  SmoothVisible = true
  Source = -> [Part002]
  Type = 2
  X = 64.32
  XDirection = (1e-16,1,0)
  Y = 0
FEATURE [TechDraw::DrawProjGroupItem] ProjItem007  label="Left001"
  Caption = Left Side
  CoarseView = false
  Direction = (-1,-1e-16,0)
  Focus = 100
  HardHidden = false
  IsoCount = 0
  IsoHidden = false
  IsoVisible = false
  LockPosition = false
  Perspective = false
  Rotation = 0
  RotationVector = (1,0,0)
  ScaleType = 0
  ScrubCount = 1
  SeamHidden = false
  SeamVisible = false
  SmoothHidden = false
  SmoothVisible = true
  Source = -> [Part002]
  Type = 1
  X = -74.8453
  XDirection = (1e-16,-1,0)
  Y = 0
FEATURE [TechDraw::DrawProjGroupItem] ProjItem008  label="Bottom001"
  Caption = Bottom
  CoarseView = false
  Direction = (0,0,-1)
  Focus = 100
  HardHidden = false
  IsoCount = 0
  IsoHidden = false
  IsoVisible = false
  LockPosition = false
  Perspective = false
  Rotation = 0
  RotationVector = (1,0,0)
  ScaleType = 0
  ScrubCount = 1
  SeamHidden = false
  SeamVisible = false
  SmoothHidden = false
  SmoothVisible = true
  Source = -> [Part002]
  Type = 5
  X = 0
  XDirection = (1,0,0)
  Y = -79.32
FEATURE [TechDraw::DrawProjGroupItem] ProjItem009  label="Top001"
  Caption = Top
  CoarseView = false
  Direction = (0,0,1)
  Focus = 100
  HardHidden = false
  IsoCount = 0
  IsoHidden = false
  IsoVisible = false
  LockPosition = false
  Perspective = false
  Rotation = 0
  RotationVector = (1,0,0)
  ScaleType = 0
  ScrubCount = 1
  SeamHidden = false
  SeamVisible = false
  SmoothHidden = false
  SmoothVisible = true
  Source = -> [Part002]
  Type = 4
  X = 0
  XDirection = (1,0,0)
  Y = 108.84
FEATURE [TechDraw::DrawViewSection] SectionView  label="Section 1 - 1"
  BaseView = -> View002
  Caption = Section 1 - 1
  CoarseView = false
  CutSurfaceDisplay = 2
  Direction = (1e-16,0,-1)
  FileGeomPattern = /nix/store/pq0nyxxy2kqpbxa60sq5alwp8h08jyz9-freecad-1.0.1/share/Mod/TechDraw/PAT/FCPAT.pat
  FileHatchPattern = /nix/store/pq0nyxxy2kqpbxa60sq5alwp8h08jyz9-freecad-1.0.1/share/Mod/TechDraw/Patterns/simple.svg
  Focus = 100
  FuseBeforeCut = false
  HardHidden = false
  HatchOffset = (0,0,0)
  HatchRotation = 0
  HatchScale = 1
  IsoCount = 0
  IsoHidden = false
  IsoVisible = false
  LockPosition = false
  NameGeomPattern = Diamond
  Perspective = false
  Rotation = 0
  ScaleType = 0
  ScrubCount = 1
  SeamHidden = false
  SeamVisible = false
  SectionDirection = 4
  SectionLineStretch = 1
  SectionNormal = (1e-16,0,-1)
  SectionOrigin = (-0.32,-30,-7.9)
  SectionSymbol = 1
  SmoothHidden = false
  SmoothVisible = true
  Source = -> [Part002]
  TrimAfterCut = false
  UsePreviousCut = false
  X = 318.753
  XDirection = (1,0,1e-16)
  Y = 263.529
FEATURE [TechDraw::DrawViewSection] SectionView001  label="Section 2 - 2"
  BaseView = -> View002
  Caption = Section 2 - 2
  CoarseView = false
  CutSurfaceDisplay = 2
  Direction = (1,0,0)
  FileGeomPattern = /nix/store/pq0nyxxy2kqpbxa60sq5alwp8h08jyz9-freecad-1.0.1/share/Mod/TechDraw/PAT/FCPAT.pat
  FileHatchPattern = /nix/store/pq0nyxxy2kqpbxa60sq5alwp8h08jyz9-freecad-1.0.1/share/Mod/TechDraw/Patterns/simple.svg
  Focus = 100
  FuseBeforeCut = false
  HardHidden = false
  HatchOffset = (0,0,0)
  HatchRotation = 0
  HatchScale = 1
  IsoCount = 0
  IsoHidden = false
  IsoVisible = false
  LockPosition = false
  NameGeomPattern = Diamond
  Perspective = false
  Rotation = 90
  ScaleType = 0
  ScrubCount = 1
  SeamHidden = false
  SeamVisible = false
  SectionDirection = 4
  SectionLineStretch = 1
  SectionNormal = (1,0,0)
  SectionOrigin = (-0.32,-30,-7.9)
  SectionSymbol = 2
  SmoothHidden = false
  SmoothVisible = true
  Source = -> [Part002]
  TrimAfterCut = false
  UsePreviousCut = false
  X = 273.26
  XDirection = (0,0,1)
  Y = 203.415
FEATURE [TechDraw::DrawViewSection] SectionView002  label="Section 3 - 3"
  BaseView = -> ProjItem009
  Caption = Section 3 - 3
  CoarseView = false
  CutSurfaceDisplay = 2
  Direction = (1e-16,-1,0)
  FileGeomPattern = /nix/store/pq0nyxxy2kqpbxa60sq5alwp8h08jyz9-freecad-1.0.1/share/Mod/TechDraw/PAT/FCPAT.pat
  FileHatchPattern = /nix/store/pq0nyxxy2kqpbxa60sq5alwp8h08jyz9-freecad-1.0.1/share/Mod/TechDraw/Patterns/simple.svg
  Focus = 100
  FuseBeforeCut = false
  HardHidden = false
  HatchOffset = (0,0,0)
  HatchRotation = 0
  HatchScale = 1
  IsoCount = 0
  IsoHidden = false
  IsoVisible = false
  LockPosition = false
  NameGeomPattern = Diamond
  Perspective = false
  Rotation = 0
  ScaleType = 0
  ScrubCount = 1
  SeamHidden = false
  SeamVisible = false
  SectionDirection = 4
  SectionLineStretch = 1
  SectionNormal = (1e-16,-1,0)
  SectionOrigin = (-0.32,-30,-7.9)
  SectionSymbol = 3
  SmoothHidden = false
  SmoothVisible = true
  Source = -> [Part002]
  TrimAfterCut = false
  UsePreviousCut = false
  X = 319.082
  XDirection = (1,1e-16,0)
  Y = 203.834
FEATURE [TechDraw::DrawViewSection] SectionView003  label="Section 4 - 4"
  BaseView = -> ProjItem008
  Caption = Section 4 - 4
  CoarseView = false
  CutSurfaceDisplay = 2
  Direction = (1e-16,-1,0)
  FileGeomPattern = /nix/store/pq0nyxxy2kqpbxa60sq5alwp8h08jyz9-freecad-1.0.1/share/Mod/TechDraw/PAT/FCPAT.pat
  FileHatchPattern = /nix/store/pq0nyxxy2kqpbxa60sq5alwp8h08jyz9-freecad-1.0.1/share/Mod/TechDraw/Patterns/simple.svg
  Focus = 100
  FuseBeforeCut = false
  HardHidden = false
  HatchOffset = (0,0,0)
  HatchRotation = 0
  HatchScale = 1
  IsoCount = 0
  IsoHidden = false
  IsoVisible = false
  LockPosition = false
  NameGeomPattern = Diamond
  Perspective = false
  Rotation = 0
  ScaleType = 0
  ScrubCount = 1
  SeamHidden = false
  SeamVisible = false
  SectionDirection = 4
  SectionLineStretch = 1
  SectionNormal = (1e-16,-1,0)
  SectionOrigin = (-0.32,-30,-7.9)
  SectionSymbol = 4
  SmoothHidden = false
  SmoothVisible = true
  Source = -> [Part002]
  TrimAfterCut = false
  UsePreviousCut = false
  X = 319.448
  XDirection = (1,1e-16,0)
  Y = 117.355
FEATURE [TechDraw::DrawProjGroupItem] ProjItem010  label="FrontTopLeft"
  Caption = FrontTopLeftIsometric
  CoarseView = false
  Direction = (-0.57735,-0.57735,0.57735)
  Focus = 100
  HardHidden = false
  IsoCount = 0
  IsoHidden = false
  IsoVisible = false
  LockPosition = false
  Perspective = false
  Rotation = 0
  RotationVector = (1,0,0)
  ScaleType = 0
  ScrubCount = 1
  SeamHidden = false
  SeamVisible = false
  SmoothHidden = false
  SmoothVisible = true
  Source = -> [Part002]
  Type = 6
  X = -74.8453
  XDirection = (0.707107,-0.707107,0)
  Y = 108.84
FEATURE [TechDraw::DrawProjGroup] ProjGroup002
  Anchor = -> View002
  AutoDistribute = true
  LockPosition = false
  ProjectionType = 2
  Rotation = 0
  ScaleType = 0
  Source = -> [Part002]
  Views = -> [View002,ProjItem006,ProjItem007,ProjItem008,ProjItem009,ProjItem010]
  X = 126.99
  Y = 127.884
  spacingX = 35
  spacingY = 35
FEATURE [TechDraw::DrawSVGTemplate] Template002
  EditableTexts = creator=Peter; date_of_issue=8/13/25; document_type=Component Drawing; general_tolerances=ISO 2768-m; identification_number=DN; language_code=EN; legal_owner_2=Orbtronics; part_material=Polycarbonate/ASA Alloy; revision_index=AAA; scale=1 : 1; sheet_number=3 / 3; title=IoT Device Assembly
  Height = 297
  Orientation = 1
  Template = <userpath>/projects/.interviews/orbtronics/l1-mechatronics-engineer/cad/assets/templates/A3_Landscape_ISO5457_minimal_third-angle.svg
  Width = 420
FEATURE [Spreadsheet::Sheet] Spreadsheet003  label="Spreadsheet_AssemblySpecifications"
  cells = A1='Item; B1='Weight (g); C1='Length (mm); D1='Width (mm); E1='Depth (mm); A2='EnclosureTop; B2==23249.6 / 1000 * 1.16; C2=68.64; D2=38.64; E2=20; A3='EnclosureBottom; B3==28901 / 1000 * 1.16; C3=68.64; D3=38.64; E3=20; A4='ArduinoNano33IoT; B4=5; C4=45; D4=18; E4=7; A5='DHT22; B5=2.4; C5=28; D5=12; E5=10; A6='103060 Battery; B6=38; C6=60; D6=30; E6=10; A7='Total; B7==sum(B2:B6)
FEATURE [TechDraw::DrawRichAnno] RichTextAnnotation
  AnnoText = <!DOCTYPE HTML PUBLIC "-//W3C//DTD HTML 4.0//EN" "http://www.w3.org/TR/REC-html40/strict.dtd">\n<html><head><meta name="qrichtext" content="1" /><meta charset="utf-8" /><style type="text/css">\np, li { white-space: pre-wrap; }\nhr { height: 1px; border-width: 0; }\nli.unchecked::marker { content: "\2610"; }\nli.checked::marker { content: "\2612"; }\n</style></head><body style=" font-family:'FiraCode Nerd Font Propo'; font-size:9pt; font-weight:400; font-style:normal;">\n<p style=" margin-top:0px; margin-bottom:0px; margin-left:0px; margin-right:0px; -qt-block-indent:0; text-indent:0px;"><span style=" font-size:8pt; font-weight:700; text-decoration: underline;">Notes</span></p>\n<p style="-qt-paragraph-type:empty; margin-top:0px; margin-bottom:0px; margin-left:0px; margin-right:0px; -qt-block-indent:0; text-indent:0px; font-size:8pt;"><br /></p>\n<p style=" margin-top:0px; margin-bottom:0px; margin-left:0px; margin-right:0px; -qt-block-indent:0; text-indent:0px;"><span style=" font-size:8pt;">PartDensity: 23.25 cm^3</span></p>\n<p style=" margin-top:0px; margin-bottom:0px; margin-left:0px; margin-right:0px; -qt-block-indent:0; text-indent:0px;"><span style=" font-size:8pt;">PartWeight: ≈26.97g</span></p>\n<p style=" margin-top:0px; margin-bottom:0px; margin-left:0px; margin-right:0px; -qt-block-indent:0; text-indent:0px;"><span style=" font-size:8pt;">PartWallThickness: 4mm</span></p>\n<p style=" margin-top:0px; margin-bottom:0px; margin-left:0px; margin-right:0px; -qt-block-indent:0; text-indent:0px;"><span style=" font-size:8pt;">Material: ASA</span></p>\n<p style=" margin-top:0px; margin-bottom:0px; margin-left:0px; margin-right:0px; -qt-block-indent:0; text-indent:0px;"><span style=" font-size:8pt;">MaterialAverageDensity: ≈1.16</span></p></body></html>
  LockPosition = false
  MaxWidth = -1
  Rotation = 0
  ScaleType = 0
  ShowFrame = false
  X = 60.9391
  Y = 32.9242
FEATURE [TechDraw::DrawViewDetail] Detail005  label="Detail 009"
  AnchorPoint = (-10.14,-23.27,0)
  BaseView = -> SectionView002
  Caption = Detail 3
  CoarseView = false
  Direction = (1e-16,-1,0)
  Focus = 100
  HardHidden = false
  IsoCount = 0
  IsoHidden = false
  IsoVisible = false
  LockPosition = false
  Perspective = false
  Radius = 5
  Reference = 3
  Rotation = 0
  Scale = 2
  ScaleType = 2
  ScrubCount = 1
  SeamHidden = false
  SeamVisible = false
  ShowHighlight = true
  ShowMatting = true
  SmoothHidden = false
  SmoothVisible = true
  Source = -> [Part002]
  X = 374.201
  XDirection = (1,1e-16,0)
  Y = 156.9
FEATURE [TechDraw::DrawViewDetail] Detail006  label="Detail 007"
  AnchorPoint = (-7.32,-12.1,0)
  BaseView = -> SectionView002
  Caption = Detail 2
  CoarseView = false
  Direction = (1e-16,-1,0)
  Focus = 100
  HardHidden = false
  IsoCount = 0
  IsoHidden = false
  IsoVisible = false
  LockPosition = false
  Perspective = false
  Radius = 5
  Reference = 2
  Rotation = 0
  Scale = 2
  ScaleType = 2
  ScrubCount = 1
  SeamHidden = false
  SeamVisible = false
  ShowHighlight = true
  ShowMatting = true
  SmoothHidden = false
  SmoothVisible = true
  Source = -> [Part002]
  X = 373.762
  XDirection = (1,1e-16,0)
  Y = 203.415
FEATURE [TechDraw::DrawViewDetail] Detail007  label="Detail 008"
  AnchorPoint = (-12.53,27.89,0)
  BaseView = -> SectionView002
  Caption = Detail 1
  CoarseView = false
  Direction = (1e-16,-1,0)
  Focus = 100
  HardHidden = false
  IsoCount = 0
  IsoHidden = false
  IsoVisible = false
  LockPosition = false
  Perspective = false
  Radius = 10
  Reference = 1
  Rotation = 0
  Scale = 2
  ScaleType = 2
  ScrubCount = 1
  SeamHidden = false
  SeamVisible = false
  ShowHighlight = true
  ShowMatting = true
  SmoothHidden = false
  SmoothVisible = true
  Source = -> [Part002]
  X = 374.201
  XDirection = (1,1e-16,0)
  Y = 256.219
FEATURE [TechDraw::DrawViewDimension] Dimension082
  AngleOverride = false
  Arbitrary = false
  ArbitraryTolerances = false
  BoxCorners = (2) [(-5.5,-5.46229,0),(5.5,5.53771,0)]
  EqualTolerance = true
  ExtensionAngle = 0
  FormatSpec = ⌀%.2w
  FormatSpecOverTolerance = %+.2w
  FormatSpecUnderTolerance = %+.2w
  Inverted = false
  LineAngle = 0
  LockPosition = false
  MeasureType = 1
  OverTolerance = 0
  References2D = -> [Detail005]
  Rotation = 0
  ScaleType = 0
  TheoreticalExact = false
  Type = 5
  UnderTolerance = 0
  X = 24.105
  Y = 4.37727
FEATURE [TechDraw::DrawViewDimension] Dimension083
  AngleOverride = false
  Arbitrary = false
  ArbitraryTolerances = false
  BoxCorners = (2) [(-2.5,-2.72,0),(2.58,2.36,0)]
  EqualTolerance = true
  ExtensionAngle = 0
  FormatSpec = ⌀%.2w
  FormatSpecOverTolerance = %+.2w
  FormatSpecUnderTolerance = %+.2w
  Inverted = false
  LineAngle = 0
  LockPosition = false
  MeasureType = 1
  OverTolerance = 0
  References2D = -> [Detail006]
  Rotation = 0
  ScaleType = 0
  TheoreticalExact = false
  Type = 5
  UnderTolerance = 0
  X = 24.0864
  Y = 4.36692
FEATURE [TechDraw::DrawViewDimension] Dimension084
  AngleOverride = false
  Arbitrary = false
  ArbitraryTolerances = false
  BoxCorners = (2) [(-10,-34.32,-1e-07),(10,34.32,1e-07)]
  EqualTolerance = true
  ExtensionAngle = 0
  FormatSpec = %.2w
  FormatSpecOverTolerance = %+.2w
  FormatSpecUnderTolerance = %+.2w
  Inverted = false
  LineAngle = 0
  LockPosition = false
  MeasureType = 1
  OverTolerance = 0
  References2D = -> [ProjItem007]
  Rotation = 0
  ScaleType = 0
  TheoreticalExact = false
  Type = 0
  UnderTolerance = 0
  X = 0
  Y = 45.2363
FEATURE [TechDraw::DrawViewDimension] Dimension085
  AngleOverride = false
  Arbitrary = false
  ArbitraryTolerances = false
  BoxCorners = (2) [(-10,-34.32,-1e-07),(10,34.32,1e-07)]
  EqualTolerance = true
  ExtensionAngle = 0
  FormatSpec = %.2w
  FormatSpecOverTolerance = %+.2w
  FormatSpecUnderTolerance = %+.2w
  Inverted = false
  LineAngle = 0
  LockPosition = false
  MeasureType = 1
  OverTolerance = 0
  References2D = -> [ProjItem007]
  Rotation = 0
  ScaleType = 0
  TheoreticalExact = false
  Type = 0
  UnderTolerance = 0
  X = 21.2378
  Y = 0
FEATURE [TechDraw::DrawViewDimension] Dimension086
  AngleOverride = false
  Arbitrary = false
  ArbitraryTolerances = false
  BoxCorners = (2) [(-10,-34.32,-1e-07),(10,34.32,1e-07)]
  EqualTolerance = true
  ExtensionAngle = 0
  FormatSpec = %.2w
  FormatSpecOverTolerance = %+.2w
  FormatSpecUnderTolerance = %+.2w
  Inverted = false
  LineAngle = 0
  LockPosition = false
  MeasureType = 1
  OverTolerance = 0
  References2D = -> [ProjItem006]
  Rotation = 0
  ScaleType = 0
  TheoreticalExact = false
  Type = 0
  UnderTolerance = 0
  X = 0
  Y = 45.3099
FEATURE [TechDraw::DrawViewDimension] Dimension087
  AngleOverride = false
  Arbitrary = false
  ArbitraryTolerances = false
  BoxCorners = (2) [(-10,-34.32,-1e-07),(10,34.32,1e-07)]
  EqualTolerance = true
  ExtensionAngle = 0
  FormatSpec = %.2w
  FormatSpecOverTolerance = %+.2w
  FormatSpecUnderTolerance = %+.2w
  Inverted = false
  LineAngle = 0
  LockPosition = false
  MeasureType = 1
  OverTolerance = 0
  References2D = -> [ProjItem006]
  Rotation = 0
  ScaleType = 0
  TheoreticalExact = false
  Type = 0
  UnderTolerance = 0
  X = -21.339
  Y = 0
FEATURE [TechDraw::DrawViewDimension] Dimension088
  AngleOverride = false
  Arbitrary = false
  ArbitraryTolerances = false
  BoxCorners = (2) [(-19.32,-10,-1e-07),(19.32,10,1e-07)]
  EqualTolerance = true
  ExtensionAngle = 0
  FormatSpec = %.2w
  FormatSpecOverTolerance = %+.2w
  FormatSpecUnderTolerance = %+.2w
  Inverted = false
  LineAngle = 0
  LockPosition = false
  MeasureType = 1
  OverTolerance = 0
  References2D = -> [ProjItem008]
  Rotation = 0
  ScaleType = 0
  TheoreticalExact = false
  Type = 0
  UnderTolerance = 0
  X = 0
  Y = 19.8592
FEATURE [TechDraw::DrawViewDimension] Dimension089
  AngleOverride = false
  Arbitrary = false
  ArbitraryTolerances = false
  BoxCorners = (2) [(-19.32,-10,-1e-07),(19.32,10,1e-07)]
  EqualTolerance = true
  ExtensionAngle = 0
  FormatSpec = %.2w
  FormatSpecOverTolerance = %+.2w
  FormatSpecUnderTolerance = %+.2w
  Inverted = false
  LineAngle = 0
  LockPosition = false
  MeasureType = 1
  OverTolerance = 0
  References2D = -> [ProjItem008]
  Rotation = 0
  ScaleType = 0
  TheoreticalExact = false
  Type = 0
  UnderTolerance = 0
  X = -36.1503
  Y = 0
FEATURE [TechDraw::DrawViewDimension] Dimension090
  AngleOverride = false
  Arbitrary = false
  ArbitraryTolerances = false
  BoxCorners = (2) [(-19.32,-10,-1e-07),(19.32,10,1e-07)]
  EqualTolerance = true
  ExtensionAngle = 0
  FormatSpec = %.2w
  FormatSpecOverTolerance = %+.2w
  FormatSpecUnderTolerance = %+.2w
  Inverted = false
  LineAngle = 0
  LockPosition = false
  MeasureType = 1
  OverTolerance = 0
  References2D = -> [ProjItem009]
  Rotation = 0
  ScaleType = 0
  TheoreticalExact = false
  Type = 0
  UnderTolerance = 0
  X = 0
  Y = 20.4365
FEATURE [TechDraw::DrawViewDimension] Dimension091
  AngleOverride = false
  Arbitrary = false
  ArbitraryTolerances = false
  BoxCorners = (2) [(-19.32,-10,-1e-07),(19.32,10,1e-07)]
  EqualTolerance = true
  ExtensionAngle = 0
  FormatSpec = %.2w
  FormatSpecOverTolerance = %+.2w
  FormatSpecUnderTolerance = %+.2w
  Inverted = false
  LineAngle = 0
  LockPosition = false
  MeasureType = 1
  OverTolerance = 0
  References2D = -> [ProjItem009]
  Rotation = 0
  ScaleType = 0
  TheoreticalExact = false
  Type = 0
  UnderTolerance = 0
  X = -35.6401
  Y = 0
FEATURE [TechDraw::DrawViewDetail] Detail008  label="Detail 010"
  AnchorPoint = (0,16.41,0)
  BaseView = -> View002
  Caption = Detail 4
  CoarseView = false
  Direction = (0,-1,0)
  Focus = 100
  HardHidden = false
  IsoCount = 0
  IsoHidden = false
  IsoVisible = false
  LockPosition = false
  Perspective = false
  Radius = 16
  Reference = 4
  Rotation = 0
  Scale = 2
  ScaleType = 2
  ScrubCount = 1
  SeamHidden = false
  SeamVisible = false
  ShowHighlight = true
  ShowMatting = true
  SmoothHidden = false
  SmoothVisible = true
  Source = -> [Part002]
  X = 204.031
  XDirection = (1,0,0)
  Y = 241.915
FEATURE [TechDraw::DrawViewDimension] Dimension092
  AngleOverride = false
  Arbitrary = false
  ArbitraryTolerances = false
  BoxCorners = (2) [(-32.32,-32.32,0),(32.32,32.32,0)]
  EqualTolerance = true
  ExtensionAngle = 0
  FormatSpec = %.2w
  FormatSpecOverTolerance = %+.2w
  FormatSpecUnderTolerance = %+.2w
  Inverted = false
  LineAngle = 0
  LockPosition = false
  MeasureType = 1
  OverTolerance = 0
  References2D = -> [Detail008]
  Rotation = 0
  ScaleType = 0
  TheoreticalExact = false
  Type = 0
  UnderTolerance = 0
  X = 0.66
  Y = 30.3833
FEATURE [TechDraw::DrawViewDimension] Dimension094
  AngleOverride = false
  Arbitrary = false
  ArbitraryTolerances = false
  BoxCorners = (2) [(-32.32,-32.32,0),(32.32,32.32,0)]
  EqualTolerance = true
  ExtensionAngle = 0
  FormatSpec = %.2w
  FormatSpecOverTolerance = %+.2w
  FormatSpecUnderTolerance = %+.2w
  Inverted = false
  LineAngle = 0
  LockPosition = false
  MeasureType = 1
  OverTolerance = 0
  References2D = -> [Detail008]
  Rotation = 0
  ScaleType = 0
  TheoreticalExact = false
  Type = 2
  UnderTolerance = 0
  X = -19.0169
  Y = 14.3237
FEATURE [TechDraw::DrawViewDimension] Dimension095
  AngleOverride = false
  Arbitrary = false
  ArbitraryTolerances = false
  BoxCorners = (2) [(-32.32,-32.32,0),(32.32,32.32,0)]
  EqualTolerance = true
  ExtensionAngle = 0
  FormatSpec = %.2w
  FormatSpecOverTolerance = %+.2w
  FormatSpecUnderTolerance = %+.2w
  Inverted = false
  LineAngle = 0
  LockPosition = false
  MeasureType = 1
  OverTolerance = 0
  References2D = -> [Detail008]
  Rotation = 0
  ScaleType = 0
  TheoreticalExact = false
  Type = 2
  UnderTolerance = 0
  X = -26.0169
  Y = -5.0462
FEATURE [TechDraw::DrawViewDimension] Dimension096
  AngleOverride = false
  Arbitrary = false
  ArbitraryTolerances = false
  BoxCorners = (2) [(-32.32,-32.32,0),(32.32,32.32,0)]
  EqualTolerance = true
  ExtensionAngle = 0
  FormatSpec = %.2w
  FormatSpecOverTolerance = %+.2w
  FormatSpecUnderTolerance = %+.2w
  Inverted = false
  LineAngle = 0
  LockPosition = false
  MeasureType = 1
  OverTolerance = 0
  References2D = -> [Detail008]
  Rotation = 0
  ScaleType = 0
  TheoreticalExact = false
  Type = 0
  UnderTolerance = 0
  X = 18.0048
  Y = 15.1696
FEATURE [TechDraw::DrawViewDimension] Dimension097
  AngleOverride = false
  Arbitrary = false
  ArbitraryTolerances = false
  BoxCorners = (2) [(-32.32,-32.32,0),(32.32,32.32,0)]
  EqualTolerance = true
  ExtensionAngle = 0
  FormatSpec = %.2w
  FormatSpecOverTolerance = %+.2w
  FormatSpecUnderTolerance = %+.2w
  Inverted = false
  LineAngle = 0
  LockPosition = false
  MeasureType = 1
  OverTolerance = 0
  References2D = -> [Detail008]
  Rotation = 0
  ScaleType = 0
  TheoreticalExact = false
  Type = 0
  UnderTolerance = 0
  X = -12.0169
  Y = -18.3124
FEATURE [TechDraw::DrawViewDimension] Dimension098
  AngleOverride = false
  Arbitrary = false
  ArbitraryTolerances = false
  BoxCorners = (2) [(-10,-34.32,-1e-07),(10,34.32,1e-07)]
  EqualTolerance = true
  ExtensionAngle = 0
  FormatSpec = %.2w
  FormatSpecOverTolerance = %+.2w
  FormatSpecUnderTolerance = %+.2w
  Inverted = false
  LineAngle = 0
  LockPosition = false
  MeasureType = 1
  OverTolerance = 0
  References2D = -> [SectionView001]
  Rotation = 0
  ScaleType = 0
  TheoreticalExact = false
  Type = 0
  UnderTolerance = 0
  X = -18.1376
  Y = 46.2163
FEATURE [TechDraw::DrawViewDimension] Dimension099
  AngleOverride = false
  Arbitrary = false
  ArbitraryTolerances = false
  BoxCorners = (2) [(-32.32,-32.32,0),(32.32,32.32,0)]
  EqualTolerance = true
  ExtensionAngle = 0
  FormatSpec = %.2w
  FormatSpecOverTolerance = %+.2w
  FormatSpecUnderTolerance = %+.2w
  Inverted = false
  LineAngle = 0
  LockPosition = false
  MeasureType = 1
  OverTolerance = 0
  References2D = -> [Detail008]
  Rotation = 0
  ScaleType = 0
  TheoreticalExact = false
  Type = 0
  UnderTolerance = 0
  X = 11.4001
  Y = -1.90623
FEATURE [TechDraw::DrawViewDimension] Dimension100
  AngleOverride = false
  Arbitrary = false
  ArbitraryTolerances = false
  BoxCorners = (2) [(-32.32,-32.32,0),(32.32,32.32,0)]
  EqualTolerance = true
  ExtensionAngle = 0
  FormatSpec = %.2w
  FormatSpecOverTolerance = %+.2w
  FormatSpecUnderTolerance = %+.2w
  Inverted = false
  LineAngle = 0
  LockPosition = false
  MeasureType = 1
  OverTolerance = 0
  References2D = -> [Detail008]
  Rotation = 0
  ScaleType = 0
  TheoreticalExact = false
  Type = 0
  UnderTolerance = 0
  X = 12.4437
  Y = 16.4462
FEATURE [TechDraw::DrawViewDimension] Dimension101
  AngleOverride = false
  Arbitrary = false
  ArbitraryTolerances = false
  BoxCorners = (2) [(-10,-34.32,-1e-07),(10,34.32,1e-07)]
  EqualTolerance = true
  ExtensionAngle = 0
  FormatSpec = %.2w
  FormatSpecOverTolerance = %+.2w
  FormatSpecUnderTolerance = %+.2w
  Inverted = false
  LineAngle = 0
  LockPosition = false
  MeasureType = 1
  OverTolerance = 0
  References2D = -> [SectionView001]
  Rotation = 0
  ScaleType = 0
  TheoreticalExact = false
  Type = 0
  UnderTolerance = 0
  X = 19.9287
  Y = 42.8307
FEATURE [TechDraw::DrawViewDimension] Dimension103
  AngleOverride = false
  Arbitrary = false
  ArbitraryTolerances = false
  BoxCorners = (2) [(-19.32,-34.32,0),(19.32,34.32,0)]
  EqualTolerance = true
  ExtensionAngle = 0
  FormatSpec = %.2w
  FormatSpecOverTolerance = %+.2w
  FormatSpecUnderTolerance = %+.2w
  Inverted = false
  LineAngle = 0
  LockPosition = false
  MeasureType = 1
  OverTolerance = 0
  References2D = -> [SectionView002]
  Rotation = 0
  ScaleType = 0
  TheoreticalExact = false
  Type = 0
  UnderTolerance = 0
  X = 29.4096
  Y = 6e-06
FEATURE [TechDraw::DrawViewDimension] Dimension104
  AngleOverride = false
  Arbitrary = false
  ArbitraryTolerances = false
  BoxCorners = (2) [(-19.32,-10,-1e-07),(19.32,10,1e-07)]
  EqualTolerance = true
  ExtensionAngle = 0
  FormatSpec = %.2w
  FormatSpecOverTolerance = %+.2w
  FormatSpecUnderTolerance = %+.2w
  Inverted = false
  LineAngle = 0
  LockPosition = false
  MeasureType = 1
  OverTolerance = 0
  References2D = -> [SectionView]
  Rotation = 0
  ScaleType = 0
  TheoreticalExact = false
  Type = 0
  UnderTolerance = 0
  X = 0
  Y = 20.3521
FEATURE [TechDraw::DrawViewBalloon] Balloon012
  BubbleShape = 3
  EndType = 0
  EndTypeScale = 1
  KinkLength = 5
  LockPosition = false
  OriginX = -0.153982
  OriginY = 0.0805364
  Rotation = 0
  ScaleType = 0
  ShapeScale = 1
  SourceView = -> Detail006
  Text = M1.6x6
  TextWrapLen = -1
  X = 9.84602
  Y = 10.0805
FEATURE [TechDraw::DrawViewBalloon] Balloon013
  BubbleShape = 3
  EndType = 0
  EndTypeScale = 1
  KinkLength = 5
  LockPosition = false
  OriginX = 2.27e-14
  OriginY = -0.0188551
  Rotation = 0
  ScaleType = 0
  ShapeScale = 1
  SourceView = -> Detail005
  Text = M2x3
  TextWrapLen = -1
  X = 9.05714
  Y = 9.85816
FEATURE [TechDraw::DrawViewBalloon] Balloon014
  BubbleShape = 3
  EndType = 0
  EndTypeScale = 1
  KinkLength = 5
  LockPosition = false
  OriginX = -2.79
  OriginY = 2.43
  Rotation = 0
  ScaleType = 0
  ShapeScale = 1
  SourceView = -> Detail007
  Text = M2x30
  TextWrapLen = -1
  X = 8.07877
  Y = 12.43
FEATURE [TechDraw::DrawViewDimension] Dimension107
  AngleOverride = false
  Arbitrary = false
  ArbitraryTolerances = false
  BoxCorners = (2) [(-19.32,-34.32,0),(19.32,34.32,0)]
  EqualTolerance = true
  ExtensionAngle = 0
  FormatSpec = %.2w
  FormatSpecOverTolerance = %+.2w
  FormatSpecUnderTolerance = %+.2w
  Inverted = false
  LineAngle = 0
  LockPosition = false
  MeasureType = 1
  OverTolerance = 0
  References2D = -> [SectionView003]
  Rotation = 0
  ScaleType = 0
  TheoreticalExact = false
  Type = 0
  UnderTolerance = 0
  X = 34.7749
  Y = 14.7372
FEATURE [TechDraw::DrawViewDimension] Dimension108
  AngleOverride = false
  Arbitrary = false
  ArbitraryTolerances = false
  BoxCorners = (2) [(-19.32,-34.32,0),(19.32,34.32,0)]
  EqualTolerance = true
  ExtensionAngle = 0
  FormatSpec = %.2w
  FormatSpecOverTolerance = %+.2w
  FormatSpecUnderTolerance = %+.2w
  Inverted = false
  LineAngle = 0
  LockPosition = false
  MeasureType = 1
  OverTolerance = 0
  References2D = -> [SectionView003]
  Rotation = 0
  ScaleType = 0
  TheoreticalExact = false
  Type = 2
  UnderTolerance = 0
  X = -30.283
  Y = 8.31
FEATURE [TechDraw::DrawViewDimension] Dimension109
  AngleOverride = false
  Arbitrary = false
  ArbitraryTolerances = false
  BoxCorners = (2) [(-19.32,-34.32,0),(19.32,34.32,0)]
  EqualTolerance = true
  ExtensionAngle = 0
  FormatSpec = R%.2w
  FormatSpecOverTolerance = %+.2w
  FormatSpecUnderTolerance = %+.2w
  Inverted = false
  LineAngle = 0
  LockPosition = false
  MeasureType = 1
  OverTolerance = 0
  References2D = -> [SectionView003]
  Rotation = 0
  ScaleType = 0
  TheoreticalExact = false
  Type = 4
  UnderTolerance = 0
  X = -37.0221
  Y = -21.8942
FEATURE [TechDraw::DrawViewDimension] Dimension111
  AngleOverride = false
  Arbitrary = false
  ArbitraryTolerances = false
  BoxCorners = (2) [(-19.32,-34.32,0),(19.32,34.32,0)]
  EqualTolerance = true
  ExtensionAngle = 0
  FormatSpec = %.2w
  FormatSpecOverTolerance = %+.2w
  FormatSpecUnderTolerance = %+.2w
  Inverted = false
  LineAngle = 0
  LockPosition = false
  MeasureType = 1
  OverTolerance = 0
  References2D = -> [SectionView003]
  Rotation = 0
  ScaleType = 0
  TheoreticalExact = false
  Type = 0
  UnderTolerance = 0
  X = -36.3054
  Y = -13.0304
FEATURE [TechDraw::DrawViewDimension] Dimension112
  AngleOverride = false
  Arbitrary = false
  ArbitraryTolerances = false
  BoxCorners = (2) [(-19.32,-34.32,0),(19.32,34.32,0)]
  EqualTolerance = true
  ExtensionAngle = 0
  FormatSpec = %.2w
  FormatSpecOverTolerance = %+.2w
  FormatSpecUnderTolerance = %+.2w
  Inverted = false
  LineAngle = 0
  LockPosition = false
  MeasureType = 1
  OverTolerance = 0
  References2D = -> [SectionView003]
  Rotation = 0
  ScaleType = 0
  TheoreticalExact = false
  Type = 0
  UnderTolerance = 0
  X = 36.0955
  Y = 1.54116
FEATURE [TechDraw::DrawViewDimension] Dimension113
  AngleOverride = false
  Arbitrary = false
  ArbitraryTolerances = false
  BoxCorners = (2) [(-19.32,-34.32,0),(19.32,34.32,0)]
  EqualTolerance = true
  ExtensionAngle = 0
  FormatSpec = %.2w
  FormatSpecOverTolerance = %+.2w
  FormatSpecUnderTolerance = %+.2w
  Inverted = false
  LineAngle = 0
  LockPosition = false
  MeasureType = 1
  OverTolerance = 0
  References2D = -> [SectionView002]
  Rotation = 0
  ScaleType = 0
  TheoreticalExact = false
  Type = 0
  UnderTolerance = 0
  X = 1e-06
  Y = 7.67571
FEATURE [TechDraw::DrawPage] Page001  label="Page_02_EnclosureAssembly_Top"
  KeepUpdated = true
  NextBalloonIndex = 6
  ProjectionType = 1
  Template = -> Template001
  Views = -> [ProjGroup002,SectionView,SectionView001,SectionView002,SectionView003,RichTextAnnotation,Detail005,Detail006,Detail007,Dimension082,Dimension083,Dimension084,Dimension085,Dimension086,Dimension087,Dimension088,Dimension089,Dimension090,Dimension091,Detail008,Dimension092,Dimension094,Dimension095,Dimension096,Dimension097,Dimension098,Dimension099,Dimension100,Dimension101,Dimension103,+10 more]
FEATURE [TechDraw::DrawRichAnno] RichTextAnnotation001
  AnnoText = <!DOCTYPE HTML PUBLIC "-//W3C//DTD HTML 4.0//EN" "http://www.w3.org/TR/REC-html40/strict.dtd">\n<html><head><meta name="qrichtext" content="1" /><meta charset="utf-8" /><style type="text/css">\np, li { white-space: pre-wrap; }\nhr { height: 1px; border-width: 0; }\nli.unchecked::marker { content: "\2610"; }\nli.checked::marker { content: "\2612"; }\n</style></head><body style=" font-family:'FiraCode Nerd Font Propo'; font-size:9pt; font-weight:400; font-style:normal;">\n<p style=" margin-top:0px; margin-bottom:0px; margin-left:0px; margin-right:0px; -qt-block-indent:0; text-indent:0px;"><span style=" font-size:8pt; font-weight:700; text-decoration: underline;">Notes</span></p>\n<p style="-qt-paragraph-type:empty; margin-top:0px; margin-bottom:0px; margin-left:0px; margin-right:0px; -qt-block-indent:0; text-indent:0px; font-size:8pt;"><br /></p>\n<p style=" margin-top:0px; margin-bottom:0px; margin-left:0px; margin-right:0px; -qt-block-indent:0; text-indent:0px;"><span style=" font-size:8pt;">PartDensity: 28.9 cm^3</span></p>\n<p style=" margin-top:0px; margin-bottom:0px; margin-left:0px; margin-right:0px; -qt-block-indent:0; text-indent:0px;"><span style=" font-size:8pt;">PartWeight: ≈33.52g</span></p>\n<p style=" margin-top:0px; margin-bottom:0px; margin-left:0px; margin-right:0px; -qt-block-indent:0; text-indent:0px;"><span style=" font-size:8pt;">PartWallThickness: 4mm</span></p>\n<p style=" margin-top:0px; margin-bottom:0px; margin-left:0px; margin-right:0px; -qt-block-indent:0; text-indent:0px;"><span style=" font-size:8pt;">Material: ASA</span></p>\n<p style=" margin-top:0px; margin-bottom:0px; margin-left:0px; margin-right:0px; -qt-block-indent:0; text-indent:0px;"><span style=" font-size:8pt;">MaterialAverageDensity: ≈1.16</span></p></body></html>
  LockPosition = false
  MaxWidth = -1
  Rotation = 0
  ScaleType = 0
  ShowFrame = false
  X = 59.6107
  Y = 31.0677
FEATURE [TechDraw::DrawProjGroupItem] View003  label="Front003"
  Caption = Front
  CoarseView = false
  Direction = (0,-1,0)
  Focus = 100
  HardHidden = false
  IsoCount = 0
  IsoHidden = false
  IsoVisible = false
  LockPosition = true
  Perspective = false
  Rotation = 0
  RotationVector = (1,0,0)
  ScaleType = 2
  ScrubCount = 1
  SeamHidden = false
  SeamVisible = false
  SmoothHidden = false
  SmoothVisible = true
  Source = -> [Part001]
  Type = 0
  X = 0
  XDirection = (1,0,0)
  Y = 0
FEATURE [TechDraw::DrawProjGroupItem] ProjItem012  label="Right003"
  Caption = Right
  CoarseView = false
  Direction = (1,-1e-16,0)
  Focus = 100
  HardHidden = false
  IsoCount = 0
  IsoHidden = false
  IsoVisible = false
  LockPosition = false
  Perspective = false
  Rotation = 0
  RotationVector = (1,0,0)
  ScaleType = 0
  ScrubCount = 1
  SeamHidden = false
  SeamVisible = false
  SmoothHidden = false
  SmoothVisible = true
  Source = -> [Part001]
  Type = 2
  X = 68.32
  XDirection = (1e-16,1,0)
  Y = 0
FEATURE [TechDraw::DrawProjGroupItem] ProjItem013  label="Top002"
  Caption = Top
  CoarseView = false
  Direction = (0,0,1)
  Focus = 100
  HardHidden = false
  IsoCount = 0
  IsoHidden = false
  IsoVisible = false
  LockPosition = false
  Perspective = false
  Rotation = 0
  RotationVector = (1,0,0)
  ScaleType = 0
  ScrubCount = 1
  SeamHidden = false
  SeamVisible = false
  SmoothHidden = false
  SmoothVisible = true
  Source = -> [Part001]
  Type = 4
  X = 0
  XDirection = (1,0,0)
  Y = 108.84
FEATURE [TechDraw::DrawProjGroupItem] ProjItem014  label="Left002"
  Caption = Left
  CoarseView = false
  Direction = (-1,-1e-16,0)
  Focus = 100
  HardHidden = false
  IsoCount = 0
  IsoHidden = false
  IsoVisible = false
  LockPosition = false
  Perspective = false
  Rotation = 0
  RotationVector = (1,0,0)
  ScaleType = 0
  ScrubCount = 1
  SeamHidden = false
  SeamVisible = false
  SmoothHidden = false
  SmoothVisible = true
  Source = -> [Part001]
  Type = 1
  X = -74.8453
  XDirection = (1e-16,-1,0)
  Y = 0
FEATURE [TechDraw::DrawProjGroupItem] ProjItem015  label="FrontTopLeft001"
  Caption = FrontTopLeftIsometric
  CoarseView = false
  Direction = (-0.57735,-0.57735,0.57735)
  Focus = 100
  HardHidden = false
  IsoCount = 0
  IsoHidden = false
  IsoVisible = false
  LockPosition = false
  Perspective = false
  Rotation = 0
  RotationVector = (1,0,0)
  ScaleType = 0
  ScrubCount = 1
  SeamHidden = false
  SeamVisible = false
  SmoothHidden = false
  SmoothVisible = true
  Source = -> [Part001]
  Type = 6
  X = -74.8453
  XDirection = (0.707107,-0.707107,0)
  Y = 108.84
FEATURE [TechDraw::DrawProjGroupItem] ProjItem016  label="Bottom002"
  Caption = Bottom
  CoarseView = false
  Direction = (0,0,-1)
  Focus = 100
  HardHidden = false
  IsoCount = 0
  IsoHidden = false
  IsoVisible = false
  LockPosition = false
  Perspective = false
  Rotation = 0
  RotationVector = (1,0,0)
  ScaleType = 0
  ScrubCount = 1
  SeamHidden = false
  SeamVisible = false
  SmoothHidden = false
  SmoothVisible = true
  Source = -> [Part001]
  Type = 5
  X = 0
  XDirection = (1,0,0)
  Y = -83.32
FEATURE [TechDraw::DrawProjGroup] ProjGroup003
  Anchor = -> View003
  AutoDistribute = true
  LockPosition = false
  ProjectionType = 2
  Rotation = 0
  ScaleType = 0
  Source = -> [Part001]
  Views = -> [View003,ProjItem012,ProjItem013,ProjItem014,ProjItem015,ProjItem016]
  X = 128.456
  Y = 132.596
  spacingX = 35
  spacingY = 35
FEATURE [TechDraw::DrawViewDimension] Dimension114
  AngleOverride = false
  Arbitrary = false
  ArbitraryTolerances = false
  BoxCorners = (2) [(-19.32,-14,-1e-07),(19.32,14,1e-07)]
  EqualTolerance = true
  ExtensionAngle = 0
  FormatSpec = %.2w
  FormatSpecOverTolerance = %+.2w
  FormatSpecUnderTolerance = %+.2w
  Inverted = false
  LineAngle = 0
  LockPosition = false
  MeasureType = 1
  OverTolerance = 0
  References2D = -> [ProjItem013]
  Rotation = 0
  ScaleType = 0
  TheoreticalExact = false
  Type = 0
  UnderTolerance = 0
  X = 0
  Y = 30.3011
FEATURE [TechDraw::DrawViewDimension] Dimension115
  AngleOverride = false
  Arbitrary = false
  ArbitraryTolerances = false
  BoxCorners = (2) [(-19.32,-14,-1e-07),(19.32,14,1e-07)]
  EqualTolerance = true
  ExtensionAngle = 0
  FormatSpec = %.2w
  FormatSpecOverTolerance = %+.2w
  FormatSpecUnderTolerance = %+.2w
  Inverted = false
  LineAngle = 0
  LockPosition = false
  MeasureType = 1
  OverTolerance = 0
  References2D = -> [ProjItem013]
  Rotation = 0
  ScaleType = 0
  TheoreticalExact = false
  Type = 1
  UnderTolerance = 0
  X = 0
  Y = 23.3011
FEATURE [TechDraw::DrawViewDimension] Dimension116
  AngleOverride = false
  Arbitrary = false
  ArbitraryTolerances = false
  BoxCorners = (2) [(-19.32,-14,-1e-07),(19.32,14,1e-07)]
  EqualTolerance = true
  ExtensionAngle = 0
  FormatSpec = %.2w
  FormatSpecOverTolerance = %+.2w
  FormatSpecUnderTolerance = %+.2w
  Inverted = false
  LineAngle = 0
  LockPosition = false
  MeasureType = 1
  OverTolerance = 0
  References2D = -> [ProjItem013]
  Rotation = 0
  ScaleType = 0
  TheoreticalExact = false
  Type = 1
  UnderTolerance = 0
  X = -32.4142
  Y = 23.3011
FEATURE [TechDraw::DrawViewDimension] Dimension117
  AngleOverride = false
  Arbitrary = false
  ArbitraryTolerances = false
  BoxCorners = (2) [(-19.32,-14,-1e-07),(19.32,14,1e-07)]
  EqualTolerance = true
  ExtensionAngle = 0
  FormatSpec = %.2w
  FormatSpecOverTolerance = %+.2w
  FormatSpecUnderTolerance = %+.2w
  Inverted = false
  LineAngle = 0
  LockPosition = false
  MeasureType = 1
  OverTolerance = 0
  References2D = -> [ProjItem013]
  Rotation = 0
  ScaleType = 0
  TheoreticalExact = false
  Type = 1
  UnderTolerance = 0
  X = 30.8743
  Y = 22.8339
FEATURE [TechDraw::DrawViewDimension] Dimension118
  AngleOverride = false
  Arbitrary = false
  ArbitraryTolerances = false
  BoxCorners = (2) [(-19.32,-14,-1e-07),(19.32,14,1e-07)]
  EqualTolerance = true
  ExtensionAngle = 0
  FormatSpec = %.2w
  FormatSpecOverTolerance = %+.2w
  FormatSpecUnderTolerance = %+.2w
  Inverted = false
  LineAngle = 0
  LockPosition = false
  MeasureType = 1
  OverTolerance = 0
  References2D = -> [ProjItem013]
  Rotation = 0
  ScaleType = 0
  TheoreticalExact = false
  Type = 2
  UnderTolerance = 0
  X = -49.1468
  Y = 1.05138
FEATURE [TechDraw::DrawViewDimension] Dimension119
  AngleOverride = false
  Arbitrary = false
  ArbitraryTolerances = false
  BoxCorners = (2) [(-14,-34.32,-1e-07),(14,34.32,1e-07)]
  EqualTolerance = true
  ExtensionAngle = 0
  FormatSpec = %.2w
  FormatSpecOverTolerance = %+.2w
  FormatSpecUnderTolerance = %+.2w
  Inverted = false
  LineAngle = 0
  LockPosition = false
  MeasureType = 1
  OverTolerance = 0
  References2D = -> [ProjItem014]
  Rotation = 0
  ScaleType = 0
  TheoreticalExact = false
  Type = 0
  UnderTolerance = 0
  X = 4
  Y = 42.137
FEATURE [TechDraw::DrawViewDimension] Dimension120
  AngleOverride = false
  Arbitrary = false
  ArbitraryTolerances = false
  BoxCorners = (2) [(-14,-34.32,-1e-07),(14,34.32,1e-07)]
  EqualTolerance = true
  ExtensionAngle = 0
  FormatSpec = %.2w
  FormatSpecOverTolerance = %+.2w
  FormatSpecUnderTolerance = %+.2w
  Inverted = false
  LineAngle = 0
  LockPosition = false
  MeasureType = 1
  OverTolerance = 0
  References2D = -> [ProjItem014]
  Rotation = 0
  ScaleType = 0
  TheoreticalExact = false
  Type = 0
  UnderTolerance = 0
  X = -27.9974
  Y = 0
FEATURE [TechDraw::DrawViewDimension] Dimension121
  AngleOverride = false
  Arbitrary = false
  ArbitraryTolerances = false
  BoxCorners = (2) [(-14,-34.32,-1e-07),(14,34.32,1e-07)]
  EqualTolerance = true
  ExtensionAngle = 0
  FormatSpec = %.2w
  FormatSpecOverTolerance = %+.2w
  FormatSpecUnderTolerance = %+.2w
  Inverted = false
  LineAngle = 0
  LockPosition = false
  MeasureType = 1
  OverTolerance = 0
  References2D = -> [ProjItem014]
  Rotation = 0
  ScaleType = 0
  TheoreticalExact = false
  Type = 2
  UnderTolerance = 0
  X = -20.9974
  Y = 2
FEATURE [TechDraw::DrawViewDimension] Dimension122
  AngleOverride = false
  Arbitrary = false
  ArbitraryTolerances = false
  BoxCorners = (2) [(-19.32,-34.32,0),(19.32,34.32,0)]
  EqualTolerance = true
  ExtensionAngle = 0
  FormatSpec = %.2w
  FormatSpecOverTolerance = %+.2w
  FormatSpecUnderTolerance = %+.2w
  Inverted = false
  LineAngle = 0
  LockPosition = false
  MeasureType = 1
  OverTolerance = 0
  References2D = -> [View003]
  Rotation = 0
  ScaleType = 0
  TheoreticalExact = false
  Type = 1
  UnderTolerance = 0
  X = 0
  Y = 50.3743
FEATURE [TechDraw::DrawViewDimension] Dimension123
  AngleOverride = false
  Arbitrary = false
  ArbitraryTolerances = false
  BoxCorners = (2) [(-19.32,-34.32,0),(19.32,34.32,0)]
  EqualTolerance = true
  ExtensionAngle = 0
  FormatSpec = %.2w
  FormatSpecOverTolerance = %+.2w
  FormatSpecUnderTolerance = %+.2w
  Inverted = false
  LineAngle = 0
  LockPosition = false
  MeasureType = 1
  OverTolerance = 0
  References2D = -> [View003]
  Rotation = 0
  ScaleType = 0
  TheoreticalExact = false
  Type = 2
  UnderTolerance = 0
  X = -30.6896
  Y = 0
FEATURE [TechDraw::DrawViewDimension] Dimension124
  AngleOverride = false
  Arbitrary = false
  ArbitraryTolerances = false
  BoxCorners = (2) [(-19.32,-34.32,0),(19.32,34.32,0)]
  EqualTolerance = true
  ExtensionAngle = 0
  FormatSpec = %.2w
  FormatSpecOverTolerance = %+.2w
  FormatSpecUnderTolerance = %+.2w
  Inverted = false
  LineAngle = 0
  LockPosition = false
  MeasureType = 1
  OverTolerance = 0
  References2D = -> [View003]
  Rotation = 0
  ScaleType = 0
  TheoreticalExact = false
  Type = 2
  UnderTolerance = 0
  X = -4.00111
  Y = 0
FEATURE [TechDraw::DrawViewDimension] Dimension125
  AngleOverride = false
  Arbitrary = false
  ArbitraryTolerances = false
  BoxCorners = (2) [(-19.32,-34.32,0),(19.32,34.32,0)]
  EqualTolerance = true
  ExtensionAngle = 0
  FormatSpec = %.2w
  FormatSpecOverTolerance = %+.2w
  FormatSpecUnderTolerance = %+.2w
  Inverted = false
  LineAngle = 0
  LockPosition = false
  MeasureType = 1
  OverTolerance = 0
  References2D = -> [View003]
  Rotation = 0
  ScaleType = 0
  TheoreticalExact = false
  Type = 1
  UnderTolerance = 0
  X = 0
  Y = 43.3743
FEATURE [TechDraw::DrawViewDimension] Dimension126
  AngleOverride = false
  Arbitrary = false
  ArbitraryTolerances = false
  BoxCorners = (2) [(-14,-34.32,-1e-07),(14,34.32,1e-07)]
  EqualTolerance = true
  ExtensionAngle = 0
  FormatSpec = %.2w
  FormatSpecOverTolerance = %+.2w
  FormatSpecUnderTolerance = %+.2w
  Inverted = false
  LineAngle = 0
  LockPosition = false
  MeasureType = 1
  OverTolerance = 0
  References2D = -> [ProjItem012]
  Rotation = 0
  ScaleType = 0
  TheoreticalExact = false
  Type = 2
  UnderTolerance = 0
  X = -22.3791
  Y = 0
FEATURE [TechDraw::DrawViewDimension] Dimension127
  AngleOverride = false
  Arbitrary = false
  ArbitraryTolerances = false
  BoxCorners = (2) [(-14,-34.32,-1e-07),(14,34.32,1e-07)]
  EqualTolerance = true
  ExtensionAngle = 0
  FormatSpec = %.2w
  FormatSpecOverTolerance = %+.2w
  FormatSpecUnderTolerance = %+.2w
  Inverted = false
  LineAngle = 0
  LockPosition = false
  MeasureType = 1
  OverTolerance = 0
  References2D = -> [ProjItem012]
  Rotation = 0
  ScaleType = 0
  TheoreticalExact = false
  Type = 2
  UnderTolerance = 0
  X = 23.8067
  Y = 2
FEATURE [TechDraw::DrawViewDimension] Dimension128
  AngleOverride = false
  Arbitrary = false
  ArbitraryTolerances = false
  BoxCorners = (2) [(-14,-34.32,-1e-07),(14,34.32,1e-07)]
  EqualTolerance = true
  ExtensionAngle = 0
  FormatSpec = %.2w
  FormatSpecOverTolerance = %+.2w
  FormatSpecUnderTolerance = %+.2w
  Inverted = false
  LineAngle = 0
  LockPosition = false
  MeasureType = 1
  OverTolerance = 0
  References2D = -> [ProjItem012]
  Rotation = 0
  ScaleType = 0
  TheoreticalExact = false
  Type = 2
  UnderTolerance = 0
  X = 16.8067
  Y = 29.6175
FEATURE [TechDraw::DrawViewDimension] Dimension129
  AngleOverride = false
  Arbitrary = false
  ArbitraryTolerances = false
  BoxCorners = (2) [(-14,-34.32,-1e-07),(14,34.32,1e-07)]
  EqualTolerance = true
  ExtensionAngle = 0
  FormatSpec = %.2w
  FormatSpecOverTolerance = %+.2w
  FormatSpecUnderTolerance = %+.2w
  Inverted = false
  LineAngle = 0
  LockPosition = false
  MeasureType = 1
  OverTolerance = 0
  References2D = -> [ProjItem012]
  Rotation = 0
  ScaleType = 0
  TheoreticalExact = false
  Type = 2
  UnderTolerance = 0
  X = 16.8067
  Y = 0
FEATURE [TechDraw::DrawViewDimension] Dimension130
  AngleOverride = false
  Arbitrary = false
  ArbitraryTolerances = false
  BoxCorners = (2) [(-14,-34.32,-1e-07),(14,34.32,1e-07)]
  EqualTolerance = true
  ExtensionAngle = 0
  FormatSpec = %.2w
  FormatSpecOverTolerance = %+.2w
  FormatSpecUnderTolerance = %+.2w
  Inverted = false
  LineAngle = 0
  LockPosition = false
  MeasureType = 1
  OverTolerance = 0
  References2D = -> [ProjItem012]
  Rotation = 0
  ScaleType = 0
  TheoreticalExact = false
  Type = 1
  UnderTolerance = 0
  X = 0
  Y = 54.4326
FEATURE [TechDraw::DrawViewDimension] Dimension131
  AngleOverride = false
  Arbitrary = false
  ArbitraryTolerances = false
  BoxCorners = (2) [(-14,-34.32,-1e-07),(14,34.32,1e-07)]
  EqualTolerance = true
  ExtensionAngle = 0
  FormatSpec = %.2w
  FormatSpecOverTolerance = %+.2w
  FormatSpecUnderTolerance = %+.2w
  Inverted = false
  LineAngle = 0
  LockPosition = false
  MeasureType = 1
  OverTolerance = 0
  References2D = -> [ProjItem012]
  Rotation = 0
  ScaleType = 0
  TheoreticalExact = false
  Type = 1
  UnderTolerance = 0
  X = 19.9222
  Y = 47.4326
FEATURE [TechDraw::DrawViewDimension] Dimension132
  AngleOverride = false
  Arbitrary = false
  ArbitraryTolerances = false
  BoxCorners = (2) [(-14,-34.32,-1e-07),(14,34.32,1e-07)]
  EqualTolerance = true
  ExtensionAngle = 0
  FormatSpec = %.2w
  FormatSpecOverTolerance = %+.2w
  FormatSpecUnderTolerance = %+.2w
  Inverted = false
  LineAngle = 0
  LockPosition = false
  MeasureType = 1
  OverTolerance = 0
  References2D = -> [ProjItem012]
  Rotation = 0
  ScaleType = 0
  TheoreticalExact = false
  Type = 1
  UnderTolerance = 0
  X = -4
  Y = 42.9556
FEATURE [TechDraw::DrawViewDimension] Dimension133
  AngleOverride = false
  Arbitrary = false
  ArbitraryTolerances = false
  BoxCorners = (2) [(-14,-34.32,-1e-07),(14,34.32,1e-07)]
  EqualTolerance = true
  ExtensionAngle = 0
  FormatSpec = %.2w
  FormatSpecOverTolerance = %+.2w
  FormatSpecUnderTolerance = %+.2w
  Inverted = false
  LineAngle = 0
  LockPosition = false
  MeasureType = 1
  OverTolerance = 0
  References2D = -> [ProjItem012]
  Rotation = 0
  ScaleType = 0
  TheoreticalExact = false
  Type = 1
  UnderTolerance = 0
  X = 20.4348
  Y = -23.6573
FEATURE [TechDraw::DrawViewDimension] Dimension134
  AngleOverride = false
  Arbitrary = false
  ArbitraryTolerances = false
  BoxCorners = (2) [(-14,-34.32,-1e-07),(14,34.32,1e-07)]
  EqualTolerance = true
  ExtensionAngle = 0
  FormatSpec = %.2w
  FormatSpecOverTolerance = %+.2w
  FormatSpecUnderTolerance = %+.2w
  Inverted = false
  LineAngle = 0
  LockPosition = false
  MeasureType = 1
  OverTolerance = 0
  References2D = -> [ProjItem012]
  Rotation = 0
  ScaleType = 0
  TheoreticalExact = false
  Type = 1
  UnderTolerance = 0
  X = -4.5
  Y = 5.02379
FEATURE [TechDraw::DrawViewDimension] Dimension135
  AngleOverride = false
  Arbitrary = false
  ArbitraryTolerances = false
  BoxCorners = (2) [(-14,-34.32,-1e-07),(14,34.32,1e-07)]
  EqualTolerance = true
  ExtensionAngle = 0
  FormatSpec = %.2w
  FormatSpecOverTolerance = %+.2w
  FormatSpecUnderTolerance = %+.2w
  Inverted = false
  LineAngle = 0
  LockPosition = false
  MeasureType = 1
  OverTolerance = 0
  References2D = -> [ProjItem014]
  Rotation = 0
  ScaleType = 0
  TheoreticalExact = false
  Type = 1
  UnderTolerance = 0
  X = 4.5
  Y = 6.25825
FEATURE [TechDraw::DrawViewDimension] Dimension136
  AngleOverride = false
  Arbitrary = false
  ArbitraryTolerances = false
  BoxCorners = (2) [(-19.32,-14,-1e-07),(19.32,14,1e-07)]
  EqualTolerance = true
  ExtensionAngle = 0
  FormatSpec = %.2w
  FormatSpecOverTolerance = %+.2w
  FormatSpecUnderTolerance = %+.2w
  Inverted = false
  LineAngle = 0
  LockPosition = false
  MeasureType = 1
  OverTolerance = 0
  References2D = -> [ProjItem016]
  Rotation = 0
  ScaleType = 0
  TheoreticalExact = false
  Type = 2
  UnderTolerance = 0
  X = -4.27745
  Y = 4.5
FEATURE [TechDraw::DrawViewDimension] Dimension137
  AngleOverride = false
  Arbitrary = false
  ArbitraryTolerances = false
  BoxCorners = (2) [(-19.32,-14,-1e-07),(19.32,14,1e-07)]
  EqualTolerance = true
  ExtensionAngle = 0
  FormatSpec = %.2w
  FormatSpecOverTolerance = %+.2w
  FormatSpecUnderTolerance = %+.2w
  Inverted = false
  LineAngle = 0
  LockPosition = false
  MeasureType = 1
  OverTolerance = 0
  References2D = -> [ProjItem016]
  Rotation = 0
  ScaleType = 0
  TheoreticalExact = false
  Type = 1
  UnderTolerance = 0
  X = 0
  Y = 28.7337
FEATURE [TechDraw::DrawViewDimension] Dimension138
  AngleOverride = false
  Arbitrary = false
  ArbitraryTolerances = false
  BoxCorners = (2) [(-19.32,-14,-1e-07),(19.32,14,1e-07)]
  EqualTolerance = true
  ExtensionAngle = 0
  FormatSpec = %.2w
  FormatSpecOverTolerance = %+.2w
  FormatSpecUnderTolerance = %+.2w
  Inverted = false
  LineAngle = 0
  LockPosition = false
  MeasureType = 1
  OverTolerance = 0
  References2D = -> [ProjItem016]
  Rotation = 0
  ScaleType = 0
  TheoreticalExact = false
  Type = 2
  UnderTolerance = 0
  X = -27.2981
  Y = 4
FEATURE [TechDraw::DrawViewDimension] Dimension139
  AngleOverride = false
  Arbitrary = false
  ArbitraryTolerances = false
  BoxCorners = (2) [(-14,-34.32,-1e-07),(14,34.32,1e-07)]
  EqualTolerance = true
  ExtensionAngle = 0
  FormatSpec = %.2w
  FormatSpecOverTolerance = %+.2w
  FormatSpecUnderTolerance = %+.2w
  Inverted = false
  LineAngle = 0
  LockPosition = false
  MeasureType = 1
  OverTolerance = 0
  References2D = -> [ProjItem014]
  Rotation = 0
  ScaleType = 0
  TheoreticalExact = false
  Type = 1
  UnderTolerance = 0
  X = 0
  Y = 49.137
FEATURE [TechDraw::DrawViewDimension] Dimension140
  AngleOverride = false
  Arbitrary = false
  ArbitraryTolerances = false
  BoxCorners = (2) [(-19.32,-14,-1e-07),(19.32,14,1e-07)]
  EqualTolerance = true
  ExtensionAngle = 0
  FormatSpec = %.2w
  FormatSpecOverTolerance = %+.2w
  FormatSpecUnderTolerance = %+.2w
  Inverted = false
  LineAngle = 0
  LockPosition = false
  MeasureType = 1
  OverTolerance = 0
  References2D = -> [ProjItem016]
  Rotation = 0
  ScaleType = 0
  TheoreticalExact = false
  Type = 1
  UnderTolerance = 0
  X = 0
  Y = 21.7337
FEATURE [TechDraw::DrawViewDimension] Dimension141
  AngleOverride = false
  Arbitrary = false
  ArbitraryTolerances = false
  BoxCorners = (2) [(-19.32,-14,-1e-07),(19.32,14,1e-07)]
  EqualTolerance = true
  ExtensionAngle = 0
  FormatSpec = %.2w
  FormatSpecOverTolerance = %+.2w
  FormatSpecUnderTolerance = %+.2w
  Inverted = false
  LineAngle = 0
  LockPosition = false
  MeasureType = 1
  OverTolerance = 0
  References2D = -> [ProjItem013]
  Rotation = 0
  ScaleType = 0
  TheoreticalExact = false
  Type = 1
  UnderTolerance = 0
  X = 0
  Y = -1.68706
FEATURE [TechDraw::DrawViewSection] SectionView004  label="Section004 1 - 1"
  BaseView = -> View003
  Caption = Section 1 - 1
  CoarseView = false
  CutSurfaceDisplay = 2
  Direction = (1e-16,0,-1)
  FileGeomPattern = /nix/store/pq0nyxxy2kqpbxa60sq5alwp8h08jyz9-freecad-1.0.1/share/Mod/TechDraw/PAT/FCPAT.pat
  FileHatchPattern = /nix/store/pq0nyxxy2kqpbxa60sq5alwp8h08jyz9-freecad-1.0.1/share/Mod/TechDraw/Patterns/simple.svg
  Focus = 100
  FuseBeforeCut = false
  HardHidden = false
  HatchOffset = (0,0,0)
  HatchRotation = 0
  HatchScale = 1
  IsoCount = 0
  IsoHidden = false
  IsoVisible = false
  LockPosition = false
  NameGeomPattern = Diamond
  Perspective = false
  Rotation = 0
  ScaleType = 0
  ScrubCount = 1
  SeamHidden = false
  SeamVisible = false
  SectionDirection = 4
  SectionLineStretch = 1
  SectionNormal = (1e-16,0,-1)
  SectionOrigin = (-0.32,-6,-7.9)
  SectionSymbol = 1
  SmoothHidden = false
  SmoothVisible = true
  Source = -> [Part001]
  TrimAfterCut = false
  UsePreviousCut = false
  X = 194.961
  XDirection = (1,0,1e-16)
  Y = 49.1647
FEATURE [TechDraw::DrawViewDimension] Dimension142
  AngleOverride = false
  Arbitrary = false
  ArbitraryTolerances = false
  BoxCorners = (2) [(-19.32,-14,-1e-07),(19.32,14,1e-07)]
  EqualTolerance = true
  ExtensionAngle = 0
  FormatSpec = %.2w
  FormatSpecOverTolerance = %+.2w
  FormatSpecUnderTolerance = %+.2w
  Inverted = false
  LineAngle = 0
  LockPosition = false
  MeasureType = 1
  OverTolerance = 0
  References2D = -> [SectionView004]
  Rotation = 0
  ScaleType = 0
  TheoreticalExact = false
  Type = 0
  UnderTolerance = 0
  X = -24.2472
  Y = 21.1653
FEATURE [TechDraw::DrawViewDimension] Dimension143
  AngleOverride = false
  Arbitrary = false
  ArbitraryTolerances = false
  BoxCorners = (2) [(-19.32,-14,-1e-07),(19.32,14,1e-07)]
  EqualTolerance = true
  ExtensionAngle = 0
  FormatSpec = %.2w
  FormatSpecOverTolerance = %+.2w
  FormatSpecUnderTolerance = %+.2w
  Inverted = false
  LineAngle = 0
  LockPosition = false
  MeasureType = 1
  OverTolerance = 0
  References2D = -> [SectionView004]
  Rotation = 0
  ScaleType = 0
  TheoreticalExact = false
  Type = 0
  UnderTolerance = 0
  X = -29.7121
  Y = 4.02944
FEATURE [TechDraw::DrawViewDetail] Detail009
  AnchorPoint = (15.44,-30.64,0)
  BaseView = -> View003
  Caption = Detail 1
  CoarseView = false
  Direction = (0,-1,0)
  Focus = 100
  HardHidden = false
  IsoCount = 0
  IsoHidden = false
  IsoVisible = false
  LockPosition = false
  Perspective = false
  Radius = 8
  Reference = 1
  Rotation = 0
  Scale = 2
  ScaleType = 2
  ScrubCount = 1
  SeamHidden = false
  SeamVisible = false
  ShowHighlight = true
  ShowMatting = true
  SmoothHidden = false
  SmoothVisible = true
  Source = -> [Part001]
  X = 193.748
  XDirection = (1,0,0)
  Y = 241.435
FEATURE [TechDraw::DrawViewDimension] Dimension144
  AngleOverride = false
  Arbitrary = false
  ArbitraryTolerances = false
  BoxCorners = (2) [(-16.16,-16.16,0),(7.76,7.36,0)]
  EqualTolerance = true
  ExtensionAngle = 0
  FormatSpec = R%.2w
  FormatSpecOverTolerance = %+.2w
  FormatSpecUnderTolerance = %+.2w
  Inverted = false
  LineAngle = 0
  LockPosition = false
  MeasureType = 1
  OverTolerance = 0
  References2D = -> [Detail009]
  Rotation = 0
  ScaleType = 0
  TheoreticalExact = false
  Type = 4
  UnderTolerance = 0
  X = -11.1016
  Y = 27.9735
FEATURE [TechDraw::DrawViewDimension] Dimension145
  AngleOverride = false
  Arbitrary = false
  ArbitraryTolerances = false
  BoxCorners = (2) [(-16.16,-16.16,0),(7.76,7.36,0)]
  EqualTolerance = true
  ExtensionAngle = 0
  FormatSpec = %.2w
  FormatSpecOverTolerance = %+.2w
  FormatSpecUnderTolerance = %+.2w
  Inverted = false
  LineAngle = 0
  LockPosition = false
  MeasureType = 1
  OverTolerance = 0
  References2D = -> [Detail009]
  Rotation = 0
  ScaleType = 0
  TheoreticalExact = false
  Type = 1
  UnderTolerance = 0
  X = 3.76
  Y = 25.6593
FEATURE [TechDraw::DrawViewDimension] Dimension146
  AngleOverride = false
  Arbitrary = false
  ArbitraryTolerances = false
  BoxCorners = (2) [(-16.16,-16.16,0),(7.76,7.36,0)]
  EqualTolerance = true
  ExtensionAngle = 0
  FormatSpec = %.2w
  FormatSpecOverTolerance = %+.2w
  FormatSpecUnderTolerance = %+.2w
  Inverted = false
  LineAngle = 0
  LockPosition = false
  MeasureType = 1
  OverTolerance = 0
  References2D = -> [Detail009]
  Rotation = 0
  ScaleType = 0
  TheoreticalExact = false
  Type = 2
  UnderTolerance = 0
  X = -26.1282
  Y = -3.36
FEATURE [App::FeaturePython] Move  # WARN: FeaturePython — macro-defined, semantics opaque (R4)
  MoveType = 0
  MovementTransform = pos=(0,-75,0) rot=(0,0,1;0rad)
  References = -> Assembly001 [Assembly002.Part002.Body002.]
FEATURE [App::FeaturePython] Move001  # WARN: FeaturePython — macro-defined, semantics opaque (R4)
  MoveType = 0
  MovementTransform = pos=(0,26,0) rot=(0,0,1;0rad)
  References = -> Assembly001 [Assembly002.Part001.Body001.]
FEATURE [App::FeaturePython] Move002  # WARN: FeaturePython — macro-defined, semantics opaque (R4)
  MoveType = 0
  MovementTransform = pos=(0,51,0) rot=(-1.00436,0,0;0rad)
  References = -> Assembly001 [Assembly002.Screw008.,Assembly002.Screw007.,Assembly002.Screw006.,Assembly002.Screw009.]
FEATURE [App::FeaturePython] Move003  # WARN: FeaturePython — macro-defined, semantics opaque (R4)
  MoveType = 0
  MovementTransform = pos=(0,-12,0) rot=(0,0,1;0rad)
  References = -> Assembly001 [DHT22_Module_v3.]
FEATURE [App::FeaturePython] Move004  # WARN: FeaturePython — macro-defined, semantics opaque (R4)
  MoveType = 0
  MovementTransform = pos=(0,-10,0) rot=(0,0,1;0rad)
  References = -> Assembly001 [SP2T_Switch.]
FEATURE [App::FeaturePython] Move005  # WARN: FeaturePython — macro-defined, semantics opaque (R4)
  MoveType = 0
  MovementTransform = pos=(0,-9.00001,0) rot=(0,0,1;0rad)
  References = -> Assembly001 [Assembly.]
FEATURE [App::FeaturePython] Move006  # WARN: FeaturePython — macro-defined, semantics opaque (R4)
  MoveType = 0
  MovementTransform = pos=(0,38,0) rot=(0,0,1;0rad)
  References = -> Assembly001 [Assembly002.Part002.Body002.]
FEATURE [App::FeaturePython] Move007  # WARN: FeaturePython — macro-defined, semantics opaque (R4)
  MoveType = 0
  MovementTransform = pos=(0,2,0) rot=(-1.00436,0,0;0rad)
  References = -> Assembly001 [Screw005.,Screw010.]
FEATURE [App::FeaturePython] Exploded_View  # WARN: FeaturePython — macro-defined, semantics opaque (R4)
  Group = -> [Move,Move001,Move002,Move003,Move004,Move005,Move006,Move007]
FEATURE [Assembly::ViewGroup] Exploded_Views
  Group = -> [Exploded_View]
FEATURE [Assembly::AssemblyObject] Assembly001  label="Assembly_ioTDevice"
  Group = -> [Joints001,Assembly,DHT22_Module_v3,Part,Micro_USB_Plug_v10,SP2T_Switch,Assembly002,GroundedJoint001,Joint001,Joint002,Joint003,Joint004,Joint008,Screw010,Screw005,Screw,Exploded_Views,Exploded_View,Move,Move001,Move002,Move003,Move004,Move005,Move006,Move007,Spreadsheet003,Spreadsheet002]
  Origin = -> Origin005
  Type = Assembly
FEATURE [TechDraw::DrawProjGroupItem] View  label="Front"
  Caption = Front
  CoarseView = false
  Direction = (0,-1,0)
  Focus = 100
  HardHidden = false
  IsoCount = 0
  IsoHidden = false
  IsoVisible = false
  LockPosition = true
  Perspective = false
  Rotation = 0
  RotationVector = (1,0,0)
  ScaleType = 2
  ScrubCount = 1
  SeamHidden = false
  SeamVisible = false
  SmoothHidden = false
  SmoothVisible = true
  Source = -> [Assembly001]
  Type = 0
  X = 0
  XDirection = (1,0,0)
  Y = 0
FEATURE [TechDraw::DrawProjGroupItem] ProjItem001  label="Top"
  Caption = Top
  CoarseView = false
  Direction = (0,0,1)
  Focus = 100
  HardHidden = false
  IsoCount = 0
  IsoHidden = false
  IsoVisible = false
  LockPosition = false
  Perspective = false
  Rotation = 0
  RotationVector = (1,0,0)
  ScaleType = 0
  ScrubCount = 1
  SeamHidden = false
  SeamVisible = false
  SmoothHidden = false
  SmoothVisible = true
  Source = -> [Assembly001]
  Type = 4
  X = 0
  XDirection = (1,0,0)
  Y = 93.32
FEATURE [TechDraw::DrawProjGroupItem] ProjItem002  label="Right"
  Caption = Right Side
  CoarseView = false
  Direction = (1,-1e-16,0)
  Focus = 100
  HardHidden = false
  IsoCount = 0
  IsoHidden = false
  IsoVisible = false
  LockPosition = false
  Perspective = false
  Rotation = 0
  RotationVector = (1,0,0)
  ScaleType = 0
  ScrubCount = 1
  SeamHidden = false
  SeamVisible = false
  SmoothHidden = false
  SmoothVisible = true
  Source = -> [Assembly001]
  Type = 2
  X = 78.32
  XDirection = (1e-16,1,0)
  Y = 0
FEATURE [TechDraw::DrawProjGroupItem] ProjItem  label="Bottom"
  Caption = Bottom
  CoarseView = false
  Direction = (0,0,-1)
  Focus = 100
  HardHidden = false
  IsoCount = 0
  IsoHidden = false
  IsoVisible = false
  LockPosition = false
  Perspective = false
  Rotation = 0
  RotationVector = (1,0,0)
  ScaleType = 0
  ScrubCount = 1
  SeamHidden = false
  SeamVisible = false
  SmoothHidden = false
  SmoothVisible = true
  Source = -> [Assembly001]
  Type = 5
  X = 0
  XDirection = (1,0,0)
  Y = -93.32
FEATURE [TechDraw::DrawProjGroupItem] ProjItem003  label="Left"
  Caption = Left Side
  CoarseView = false
  Direction = (-1,-1e-16,0)
  Focus = 100
  HardHidden = false
  IsoCount = 0
  IsoHidden = false
  IsoVisible = false
  LockPosition = false
  Perspective = false
  Rotation = 0
  RotationVector = (1,0,0)
  ScaleType = 0
  ScrubCount = 1
  SeamHidden = false
  SeamVisible = false
  SmoothHidden = false
  SmoothVisible = true
  Source = -> [Assembly001]
  Type = 1
  X = -78.32
  XDirection = (1e-16,-1,0)
  Y = 0
FEATURE [TechDraw::DrawProjGroupItem] ProjItem004  label="Rear"
  Caption = Back
  CoarseView = false
  Direction = (0,1,0)
  Focus = 100
  HardHidden = false
  IsoCount = 0
  IsoHidden = false
  IsoVisible = false
  LockPosition = false
  Perspective = false
  Rotation = 0
  RotationVector = (1,0,0)
  ScaleType = 0
  ScrubCount = 1
  SeamHidden = false
  SeamVisible = false
  SmoothHidden = false
  SmoothVisible = true
  Source = -> [Assembly001]
  Type = 3
  X = 156.64
  XDirection = (-1,0,0)
  Y = 0
FEATURE [TechDraw::DrawProjGroup] ProjGroup
  Anchor = -> View
  AutoDistribute = true
  LockPosition = false
  ProjectionType = 2
  Rotation = 0
  ScaleType = 0
  Source = -> [Assembly001]
  Views = -> [View,ProjItem001,ProjItem002,ProjItem,ProjItem003,ProjItem004]
  X = 145.464
  Y = 143.429
  spacingX = 35
  spacingY = 35
FEATURE [TechDraw::DrawViewDimension] Dimension019
  AngleOverride = false
  Arbitrary = false
  ArbitraryTolerances = false
  BoxCorners = (2) [(-19.32,-34.32,-1e-07),(19.32,34.32,1e-07)]
  EqualTolerance = true
  ExtensionAngle = 0
  FormatSpec = %.2w
  FormatSpecOverTolerance = %+.2w
  FormatSpecUnderTolerance = %+.2w
  Inverted = false
  LineAngle = 0
  LockPosition = false
  MeasureType = 1
  OverTolerance = 0
  References2D = -> [View]
  Rotation = 0
  ScaleType = 0
  TheoreticalExact = false
  Type = 0
  UnderTolerance = 0
  X = 0
  Y = 43.7972
FEATURE [TechDraw::DrawViewDetail] Detail  label="Detail 1"
  AnchorPoint = (-0.06362,-8.51,0)
  BaseView = -> ProjItem001
  Caption = Detail 1
  CoarseView = false
  Direction = (0,0,1)
  Focus = 100
  HardHidden = false
  IsoCount = 0
  IsoHidden = false
  IsoVisible = false
  LockPosition = false
  Perspective = false
  Radius = 10
  Reference = 1
  Rotation = 0
  Scale = 2
  ScaleType = 2
  ScrubCount = 1
  SeamHidden = false
  SeamVisible = false
  ShowHighlight = true
  ShowMatting = true
  SmoothHidden = false
  SmoothVisible = true
  Source = -> [Assembly001]
  X = 68.9728
  XDirection = (1,0,0)
  Y = 242.104
FEATURE [TechDraw::DrawViewDetail] Detail001  label="Detail 2"
  AnchorPoint = (-0.0679258,-18.6367,0)
  BaseView = -> ProjItem
  Caption = Detail 2
  CoarseView = false
  Direction = (0,0,-1)
  Focus = 100
  HardHidden = false
  IsoCount = 0
  IsoHidden = false
  IsoVisible = false
  LockPosition = false
  Perspective = false
  Radius = 12
  Reference = 2
  Rotation = 0
  Scale = 2
  ScaleType = 2
  ScrubCount = 1
  SeamHidden = false
  SeamVisible = false
  ShowHighlight = true
  ShowMatting = true
  SmoothHidden = false
  SmoothVisible = true
  Source = -> [Assembly001]
  X = 68.9728
  XDirection = (1,0,0)
  Y = 49.2348
FEATURE [TechDraw::DrawViewDimension] Dimension023
  AngleOverride = false
  Arbitrary = false
  ArbitraryTolerances = false
  BoxCorners = (2) [(-23.0956,-24.24,0),(23.0956,8.64,0)]
  EqualTolerance = true
  ExtensionAngle = 0
  FormatSpec = %.2w
  FormatSpecOverTolerance = %+.2w
  FormatSpecUnderTolerance = %+.2w
  Inverted = false
  LineAngle = 0
  LockPosition = false
  MeasureType = 1
  OverTolerance = 0
  References2D = -> [Detail001]
  Rotation = 0
  ScaleType = 0
  TheoreticalExact = false
  Type = 1
  UnderTolerance = 0
  X = 0.135852
  Y = 42.8721
FEATURE [TechDraw::DrawViewDimension] Dimension028
  AngleOverride = false
  Arbitrary = false
  ArbitraryTolerances = false
  BoxCorners = (2) [(-23,-34.32,-1e-07),(23,34.32,1e-07)]
  EqualTolerance = true
  ExtensionAngle = 0
  FormatSpec = %.2w
  FormatSpecOverTolerance = %+.2w
  FormatSpecUnderTolerance = %+.2w
  Inverted = false
  LineAngle = 0
  LockPosition = false
  MeasureType = 1
  OverTolerance = 0
  References2D = -> [ProjItem002]
  Rotation = 0
  ScaleType = 0
  TheoreticalExact = false
  Type = 0
  UnderTolerance = 0
  X = -14
  Y = 43.9645
FEATURE [TechDraw::DrawViewDimension] Dimension031
  AngleOverride = false
  Arbitrary = false
  ArbitraryTolerances = false
  BoxCorners = (2) [(-23,-34.32,-1e-07),(23,34.32,1e-07)]
  EqualTolerance = true
  ExtensionAngle = 0
  FormatSpec = %.2w
  FormatSpecOverTolerance = %+.2w
  FormatSpecUnderTolerance = %+.2w
  Inverted = false
  LineAngle = 0
  LockPosition = false
  MeasureType = 1
  OverTolerance = 0
  References2D = -> [ProjItem003]
  Rotation = 0
  ScaleType = 0
  TheoreticalExact = false
  Type = 0
  UnderTolerance = 0
  X = 14
  Y = 43.3381
FEATURE [TechDraw::DrawViewDetail] Detail002  label="Detail 3"
  AnchorPoint = (15.08,30.07,0)
  BaseView = -> ProjItem004
  Caption = Detail 3
  CoarseView = false
  Direction = (0,1,0)
  Focus = 100
  HardHidden = false
  IsoCount = 0
  IsoHidden = false
  IsoVisible = false
  LockPosition = false
  Perspective = false
  Radius = 10
  Reference = 3
  Rotation = 0
  Scale = 2
  ScaleType = 2
  ScrubCount = 1
  SeamHidden = false
  SeamVisible = false
  ShowHighlight = true
  ShowMatting = true
  SmoothHidden = false
  SmoothVisible = true
  Source = -> [Assembly001]
  X = 200.011
  XDirection = (-1,0,0)
  Y = 237.084
FEATURE [TechDraw::DrawViewDimension] Dimension037
  AngleOverride = false
  Arbitrary = false
  ArbitraryTolerances = false
  BoxCorners = (2) [(-23.123,-24.24,0),(23.123,8.72651,0)]
  EqualTolerance = true
  ExtensionAngle = 0
  FormatSpec = %.2w
  FormatSpecOverTolerance = %+.2w
  FormatSpecUnderTolerance = %+.2w
  Inverted = false
  LineAngle = 0
  LockPosition = false
  MeasureType = 1
  OverTolerance = 0
  References2D = -> [Detail001]
  Rotation = 0
  ScaleType = 0
  TheoreticalExact = false
  Type = 0
  UnderTolerance = 0
  X = 0.135852
  Y = 35.4049
FEATURE [TechDraw::DrawViewDimension] Dimension038
  AngleOverride = false
  Arbitrary = false
  ArbitraryTolerances = false
  BoxCorners = (2) [(-23.123,-24.24,0),(23.123,8.72651,0)]
  EqualTolerance = true
  ExtensionAngle = 0
  FormatSpec = %.2w
  FormatSpecOverTolerance = %+.2w
  FormatSpecUnderTolerance = %+.2w
  Inverted = false
  LineAngle = 0
  LockPosition = false
  MeasureType = 1
  OverTolerance = 0
  References2D = -> [Detail001]
  Rotation = 0
  ScaleType = 0
  TheoreticalExact = false
  Type = 0
  UnderTolerance = 0
  X = -28.4348
  Y = 35.4049
FEATURE [TechDraw::DrawViewDimension] Dimension039
  AngleOverride = false
  Arbitrary = false
  ArbitraryTolerances = false
  BoxCorners = (2) [(-23.123,-24.24,0),(23.123,8.72651,0)]
  EqualTolerance = true
  ExtensionAngle = 0
  FormatSpec = %.2w
  FormatSpecOverTolerance = %+.2w
  FormatSpecUnderTolerance = %+.2w
  Inverted = false
  LineAngle = 0
  LockPosition = false
  MeasureType = 1
  OverTolerance = 0
  References2D = -> [Detail001]
  Rotation = 0
  ScaleType = 0
  TheoreticalExact = false
  Type = 0
  UnderTolerance = 0
  X = 28.9021
  Y = 35.4049
FEATURE [TechDraw::DrawViewDimension] Dimension040
  AngleOverride = false
  Arbitrary = false
  ArbitraryTolerances = false
  BoxCorners = (2) [(-23.123,-24.24,0),(23.123,8.72651,0)]
  EqualTolerance = true
  ExtensionAngle = 0
  FormatSpec = %.2w
  FormatSpecOverTolerance = %+.2w
  FormatSpecUnderTolerance = %+.2w
  Inverted = false
  LineAngle = 0
  LockPosition = false
  MeasureType = 1
  OverTolerance = 0
  References2D = -> [Detail001]
  Rotation = 0
  ScaleType = 0
  TheoreticalExact = false
  Type = 0
  UnderTolerance = 0
  X = -39.8933
  Y = -2.72651
FEATURE [TechDraw::DrawViewDimension] Dimension041
  AngleOverride = false
  Arbitrary = false
  ArbitraryTolerances = false
  BoxCorners = (2) [(-23.123,-24.24,0),(23.123,8.72651,0)]
  EqualTolerance = true
  ExtensionAngle = 0
  FormatSpec = %.2w
  FormatSpecOverTolerance = %+.2w
  FormatSpecUnderTolerance = %+.2w
  Inverted = false
  LineAngle = 0
  LockPosition = false
  MeasureType = 1
  OverTolerance = 0
  References2D = -> [Detail001]
  Rotation = 0
  ScaleType = 0
  TheoreticalExact = false
  Type = 2
  UnderTolerance = 0
  X = -32.8933
  Y = 15.9357
FEATURE [TechDraw::DrawViewDimension] Dimension
  AngleOverride = false
  Arbitrary = false
  ArbitraryTolerances = false
  BoxCorners = (2) [(-24,-34.32,-1e-07),(24,34.32,1e-07)]
  EqualTolerance = true
  ExtensionAngle = 0
  FormatSpec = %.2w
  FormatSpecOverTolerance = %+.2w
  FormatSpecUnderTolerance = %+.2w
  Inverted = false
  LineAngle = 0
  LockPosition = false
  MeasureType = 1
  OverTolerance = 0
  References2D = -> [ProjItem003]
  Rotation = 0
  ScaleType = 0
  TheoreticalExact = false
  Type = 0
  UnderTolerance = 0
  X = -6
  Y = 43.3381
FEATURE [TechDraw::DrawViewDimension] Dimension042
  AngleOverride = false
  Arbitrary = false
  ArbitraryTolerances = false
  BoxCorners = (2) [(-24,-34.32,-1e-07),(24,34.32,1e-07)]
  EqualTolerance = true
  ExtensionAngle = 0
  FormatSpec = %.2w
  FormatSpecOverTolerance = %+.2w
  FormatSpecUnderTolerance = %+.2w
  Inverted = false
  LineAngle = 0
  LockPosition = false
  MeasureType = 1
  OverTolerance = 0
  References2D = -> [ProjItem003]
  Rotation = 0
  ScaleType = 0
  TheoreticalExact = false
  Type = 0
  UnderTolerance = 0
  X = 4
  Y = 49.8709
FEATURE [TechDraw::DrawViewDimension] Dimension044
  AngleOverride = false
  Arbitrary = false
  ArbitraryTolerances = false
  BoxCorners = (2) [(-19.32,-24,-1e-07),(19.32,24,1e-07)]
  EqualTolerance = true
  ExtensionAngle = 0
  FormatSpec = %.2w
  FormatSpecOverTolerance = %+.2w
  FormatSpecUnderTolerance = %+.2w
  Inverted = false
  LineAngle = 0
  LockPosition = false
  MeasureType = 1
  OverTolerance = 0
  References2D = -> [ProjItem]
  Rotation = 0
  ScaleType = 0
  TheoreticalExact = false
  Type = 0
  UnderTolerance = 0
  X = 0
  Y = 33.9877
FEATURE [TechDraw::DrawViewDimension] Dimension045
  AngleOverride = false
  Arbitrary = false
  ArbitraryTolerances = false
  BoxCorners = (2) [(-19.32,-24,-1e-07),(19.32,24,1e-07)]
  EqualTolerance = true
  ExtensionAngle = 0
  FormatSpec = %.2w
  FormatSpecOverTolerance = %+.2w
  FormatSpecUnderTolerance = %+.2w
  Inverted = false
  LineAngle = 0
  LockPosition = false
  MeasureType = 1
  OverTolerance = 0
  References2D = -> [ProjItem001]
  Rotation = 0
  ScaleType = 0
  TheoreticalExact = false
  Type = 1
  UnderTolerance = 0
  X = 0
  Y = 33.2223
FEATURE [TechDraw::DrawViewDimension] Dimension046
  AngleOverride = false
  Arbitrary = false
  ArbitraryTolerances = false
  BoxCorners = (2) [(-19.32,-24,-1e-07),(19.32,24,1e-07)]
  EqualTolerance = true
  ExtensionAngle = 0
  FormatSpec = %.2w
  FormatSpecOverTolerance = %+.2w
  FormatSpecUnderTolerance = %+.2w
  Inverted = false
  LineAngle = 0
  LockPosition = false
  MeasureType = 1
  OverTolerance = 0
  References2D = -> [ProjItem001]
  Rotation = 0
  ScaleType = 0
  TheoreticalExact = false
  Type = 0
  UnderTolerance = 0
  X = 0
  Y = 39.7551
FEATURE [TechDraw::DrawViewDimension] Dimension047
  AngleOverride = false
  Arbitrary = false
  ArbitraryTolerances = false
  BoxCorners = (2) [(-19.32,-24,-1e-07),(19.32,24,1e-07)]
  EqualTolerance = true
  ExtensionAngle = 0
  FormatSpec = %.2w
  FormatSpecOverTolerance = %+.2w
  FormatSpecUnderTolerance = %+.2w
  Inverted = false
  LineAngle = 0
  LockPosition = false
  MeasureType = 1
  OverTolerance = 0
  References2D = -> [ProjItem001]
  Rotation = 0
  ScaleType = 0
  TheoreticalExact = false
  Type = 1
  UnderTolerance = 0
  X = -27.3233
  Y = 32.2832
FEATURE [TechDraw::DrawViewDimension] Dimension048
  AngleOverride = false
  Arbitrary = false
  ArbitraryTolerances = false
  BoxCorners = (2) [(-19.32,-24,-1e-07),(19.32,24,1e-07)]
  EqualTolerance = true
  ExtensionAngle = 0
  FormatSpec = %.2w
  FormatSpecOverTolerance = %+.2w
  FormatSpecUnderTolerance = %+.2w
  Inverted = false
  LineAngle = 0
  LockPosition = false
  MeasureType = 1
  OverTolerance = 0
  References2D = -> [ProjItem001]
  Rotation = 0
  ScaleType = 0
  TheoreticalExact = false
  Type = 1
  UnderTolerance = 0
  X = 27.4687
  Y = 32.2832
FEATURE [TechDraw::DrawViewDimension] Dimension049
  AngleOverride = false
  Arbitrary = false
  ArbitraryTolerances = false
  BoxCorners = (2) [(-24,-34.32,-1e-07),(24,34.32,1e-07)]
  EqualTolerance = true
  ExtensionAngle = 0
  FormatSpec = %.2w
  FormatSpecOverTolerance = %+.2w
  FormatSpecUnderTolerance = %+.2w
  Inverted = false
  LineAngle = 0
  LockPosition = false
  MeasureType = 1
  OverTolerance = 0
  References2D = -> [ProjItem002]
  Rotation = 0
  ScaleType = 0
  TheoreticalExact = false
  Type = 0
  UnderTolerance = 0
  X = -4
  Y = 50.9645
FEATURE [TechDraw::DrawViewDimension] Dimension050
  AngleOverride = false
  Arbitrary = false
  ArbitraryTolerances = false
  BoxCorners = (2) [(-24,-34.32,-1e-07),(24,34.32,1e-07)]
  EqualTolerance = true
  ExtensionAngle = 0
  FormatSpec = %.2w
  FormatSpecOverTolerance = %+.2w
  FormatSpecUnderTolerance = %+.2w
  Inverted = false
  LineAngle = 0
  LockPosition = false
  MeasureType = 1
  OverTolerance = 0
  References2D = -> [ProjItem002]
  Rotation = 0
  ScaleType = 0
  TheoreticalExact = false
  Type = 0
  UnderTolerance = 0
  X = 6
  Y = 43.4926
FEATURE [TechDraw::DrawViewDimension] Dimension051
  AngleOverride = false
  Arbitrary = false
  ArbitraryTolerances = false
  BoxCorners = (2) [(-24,-34.32,-1e-07),(24,34.32,1e-07)]
  EqualTolerance = true
  ExtensionAngle = 0
  FormatSpec = %.2w
  FormatSpecOverTolerance = %+.2w
  FormatSpecUnderTolerance = %+.2w
  Inverted = false
  LineAngle = 0
  LockPosition = false
  MeasureType = 1
  OverTolerance = 0
  References2D = -> [ProjItem002]
  Rotation = 0
  ScaleType = 0
  TheoreticalExact = false
  Type = 0
  UnderTolerance = 0
  X = 27.3941
  Y = 29.5627
FEATURE [TechDraw::DrawViewDimension] Dimension052
  AngleOverride = false
  Arbitrary = false
  ArbitraryTolerances = false
  BoxCorners = (2) [(-24,-34.32,-1e-07),(24,34.32,1e-07)]
  EqualTolerance = true
  ExtensionAngle = 0
  FormatSpec = %.2w
  FormatSpecOverTolerance = %+.2w
  FormatSpecUnderTolerance = %+.2w
  Inverted = false
  LineAngle = 0
  LockPosition = false
  MeasureType = 1
  OverTolerance = 0
  References2D = -> [ProjItem002]
  Rotation = 0
  ScaleType = 0
  TheoreticalExact = false
  Type = 0
  UnderTolerance = 0
  X = 27.3941
  Y = 0
FEATURE [TechDraw::DrawViewDimension] Dimension053
  AngleOverride = false
  Arbitrary = false
  ArbitraryTolerances = false
  BoxCorners = (2) [(-24,-34.32,-1e-07),(24,34.32,1e-07)]
  EqualTolerance = true
  ExtensionAngle = 0
  FormatSpec = %.2w
  FormatSpecOverTolerance = %+.2w
  FormatSpecUnderTolerance = %+.2w
  Inverted = false
  LineAngle = 0
  LockPosition = false
  MeasureType = 1
  OverTolerance = 0
  References2D = -> [ProjItem002]
  Rotation = 0
  ScaleType = 0
  TheoreticalExact = false
  Type = 0
  UnderTolerance = 0
  X = 34.3941
  Y = 2
FEATURE [TechDraw::DrawViewDimension] Dimension054
  AngleOverride = false
  Arbitrary = false
  ArbitraryTolerances = false
  BoxCorners = (2) [(-20.2,-20.2,-1e-07),(20.2,20.2,1e-07)]
  EqualTolerance = true
  ExtensionAngle = 0
  FormatSpec = %.2w
  FormatSpecOverTolerance = %+.2w
  FormatSpecUnderTolerance = %+.2w
  Inverted = false
  LineAngle = 0
  LockPosition = false
  MeasureType = 1
  OverTolerance = 0
  References2D = -> [Detail]
  Rotation = 0
  ScaleType = 0
  TheoreticalExact = false
  Type = 0
  UnderTolerance = 0
  X = 0.76724
  Y = 33.7911
FEATURE [TechDraw::DrawViewDimension] Dimension055
  AngleOverride = false
  Arbitrary = false
  ArbitraryTolerances = false
  BoxCorners = (2) [(-20.2,-20.2,-1e-07),(20.2,20.2,1e-07)]
  EqualTolerance = true
  ExtensionAngle = 0
  FormatSpec = %.2w
  FormatSpecOverTolerance = %+.2w
  FormatSpecUnderTolerance = %+.2w
  Inverted = false
  LineAngle = 0
  LockPosition = false
  MeasureType = 1
  OverTolerance = 0
  References2D = -> [Detail]
  Rotation = 0
  ScaleType = 0
  TheoreticalExact = false
  Type = 0
  UnderTolerance = 0
  X = -31.9751
  Y = -15.2343
FEATURE [TechDraw::DrawViewDimension] Dimension056
  AngleOverride = false
  Arbitrary = false
  ArbitraryTolerances = false
  BoxCorners = (2) [(-24,-34.32,-1e-07),(24,34.32,1e-07)]
  EqualTolerance = true
  ExtensionAngle = 0
  FormatSpec = %.2w
  FormatSpecOverTolerance = %+.2w
  FormatSpecUnderTolerance = %+.2w
  Inverted = false
  LineAngle = 0
  LockPosition = false
  MeasureType = 1
  OverTolerance = 0
  References2D = -> [ProjItem003]
  Rotation = 0
  ScaleType = 0
  TheoreticalExact = false
  Type = 2
  UnderTolerance = 0
  X = -40.2492
  Y = 2
FEATURE [TechDraw::DrawViewDimension] Dimension057
  AngleOverride = false
  Arbitrary = false
  ArbitraryTolerances = false
  BoxCorners = (2) [(-24,-34.32,-1e-07),(24,34.32,1e-07)]
  EqualTolerance = true
  ExtensionAngle = 0
  FormatSpec = %.2w
  FormatSpecOverTolerance = %+.2w
  FormatSpecUnderTolerance = %+.2w
  Inverted = false
  LineAngle = 0
  LockPosition = false
  MeasureType = 1
  OverTolerance = 0
  References2D = -> [ProjItem003]
  Rotation = 0
  ScaleType = 0
  TheoreticalExact = false
  Type = 2
  UnderTolerance = 0
  X = -33.2492
  Y = 29.9191
FEATURE [TechDraw::DrawViewDimension] Dimension058
  AngleOverride = false
  Arbitrary = false
  ArbitraryTolerances = false
  BoxCorners = (2) [(-24,-34.32,-1e-07),(24,34.32,1e-07)]
  EqualTolerance = true
  ExtensionAngle = 0
  FormatSpec = %.2w
  FormatSpecOverTolerance = %+.2w
  FormatSpecUnderTolerance = %+.2w
  Inverted = false
  LineAngle = 0
  LockPosition = false
  MeasureType = 1
  OverTolerance = 0
  References2D = -> [ProjItem003]
  Rotation = 0
  ScaleType = 0
  TheoreticalExact = false
  Type = 2
  UnderTolerance = 0
  X = -33.2492
  Y = 0
FEATURE [TechDraw::DrawViewDimension] Dimension061
  AngleOverride = false
  Arbitrary = false
  ArbitraryTolerances = false
  BoxCorners = (2) [(-19.32,-34.32,-1e-07),(19.32,34.32,1e-07)]
  EqualTolerance = true
  ExtensionAngle = 0
  FormatSpec = %.2w
  FormatSpecOverTolerance = %+.2w
  FormatSpecUnderTolerance = %+.2w
  Inverted = false
  LineAngle = 0
  LockPosition = false
  MeasureType = 1
  OverTolerance = 0
  References2D = -> [ProjItem004]
  Rotation = 0
  ScaleType = 0
  TheoreticalExact = false
  Type = 0
  UnderTolerance = 0
  X = 0
  Y = 50.8936
FEATURE [TechDraw::DrawViewDimension] Dimension062
  AngleOverride = false
  Arbitrary = false
  ArbitraryTolerances = false
  BoxCorners = (2) [(-19.32,-34.32,-1e-07),(19.32,34.32,1e-07)]
  EqualTolerance = true
  ExtensionAngle = 0
  FormatSpec = %.2w
  FormatSpecOverTolerance = %+.2w
  FormatSpecUnderTolerance = %+.2w
  Inverted = false
  LineAngle = 0
  LockPosition = false
  MeasureType = 1
  OverTolerance = 0
  References2D = -> [ProjItem004]
  Rotation = 0
  ScaleType = 0
  TheoreticalExact = false
  Type = 1
  UnderTolerance = 0
  X = 0
  Y = 43.8936
FEATURE [TechDraw::DrawViewDimension] Dimension063
  AngleOverride = false
  Arbitrary = false
  ArbitraryTolerances = false
  BoxCorners = (2) [(-20.2,-8.5,-1e-07),(8.48,20.2,1e-07)]
  EqualTolerance = true
  ExtensionAngle = 0
  FormatSpec = ⌀%.2w
  FormatSpecOverTolerance = %+.2w
  FormatSpecUnderTolerance = %+.2w
  Inverted = false
  LineAngle = 0
  LockPosition = false
  MeasureType = 1
  OverTolerance = 0
  References2D = -> [Detail002]
  Rotation = 0
  ScaleType = 0
  TheoreticalExact = false
  Type = 5
  UnderTolerance = 0
  X = 34.1706
  Y = 4.77526
FEATURE [TechDraw::DrawViewDimension] Dimension064
  AngleOverride = false
  Arbitrary = false
  ArbitraryTolerances = false
  BoxCorners = (2) [(-20.2,-8.5,-1e-07),(8.48,20.2,1e-07)]
  EqualTolerance = true
  ExtensionAngle = 0
  FormatSpec = %.2w
  FormatSpecOverTolerance = %+.2w
  FormatSpecUnderTolerance = %+.2w
  Inverted = false
  LineAngle = 0
  LockPosition = false
  MeasureType = 1
  OverTolerance = 0
  References2D = -> [Detail002]
  Rotation = 0
  ScaleType = 0
  TheoreticalExact = false
  Type = 2
  UnderTolerance = 0
  X = -30.0497
  Y = 12.7055
FEATURE [TechDraw::DrawViewDimension] Dimension065
  AngleOverride = false
  Arbitrary = false
  ArbitraryTolerances = false
  BoxCorners = (2) [(-20.2,-8.5,-1e-07),(8.48,20.2,1e-07)]
  EqualTolerance = true
  ExtensionAngle = 0
  FormatSpec = %.2w
  FormatSpecOverTolerance = %+.2w
  FormatSpecUnderTolerance = %+.2w
  Inverted = false
  LineAngle = 0
  LockPosition = false
  MeasureType = 1
  OverTolerance = 0
  References2D = -> [Detail002]
  Rotation = 0
  ScaleType = 0
  TheoreticalExact = false
  Type = 1
  UnderTolerance = 0
  X = -4.80486
  Y = 33.5829
FEATURE [TechDraw::DrawViewDimension] Dimension066
  AngleOverride = false
  Arbitrary = false
  ArbitraryTolerances = false
  BoxCorners = (2) [(-19.32,-34.32,-1e-07),(19.32,34.32,1e-07)]
  EqualTolerance = true
  ExtensionAngle = 0
  FormatSpec = %.2w
  FormatSpecOverTolerance = %+.2w
  FormatSpecUnderTolerance = %+.2w
  Inverted = false
  LineAngle = 0
  LockPosition = false
  MeasureType = 1
  OverTolerance = 0
  References2D = -> [ProjItem004]
  Rotation = 0
  ScaleType = 0
  TheoreticalExact = false
  Type = 0
  UnderTolerance = 0
  X = -31.8131
  Y = 42.9498
FEATURE [TechDraw::DrawViewDimension] Dimension067
  AngleOverride = false
  Arbitrary = false
  ArbitraryTolerances = false
  BoxCorners = (2) [(-19.32,-34.32,-1e-07),(19.32,34.32,1e-07)]
  EqualTolerance = true
  ExtensionAngle = 0
  FormatSpec = %.2w
  FormatSpecOverTolerance = %+.2w
  FormatSpecUnderTolerance = %+.2w
  Inverted = false
  LineAngle = 0
  LockPosition = false
  MeasureType = 1
  OverTolerance = 0
  References2D = -> [ProjItem004]
  Rotation = 0
  ScaleType = 0
  TheoreticalExact = false
  Type = 1
  UnderTolerance = 0
  X = 31.3823
  Y = 43.4217
FEATURE [TechDraw::DrawViewDimension] Dimension068
  AngleOverride = false
  Arbitrary = false
  ArbitraryTolerances = false
  BoxCorners = (2) [(-19.32,-34.32,-1e-07),(19.32,34.32,1e-07)]
  EqualTolerance = true
  ExtensionAngle = 0
  FormatSpec = %.2w
  FormatSpecOverTolerance = %+.2w
  FormatSpecUnderTolerance = %+.2w
  Inverted = false
  LineAngle = 0
  LockPosition = false
  MeasureType = 1
  OverTolerance = 0
  References2D = -> [ProjItem004]
  Rotation = 0
  ScaleType = 0
  TheoreticalExact = false
  Type = 0
  UnderTolerance = 0
  X = 22.0903
  Y = 2
FEATURE [TechDraw::DrawViewDimension] Dimension069
  AngleOverride = false
  Arbitrary = false
  ArbitraryTolerances = false
  BoxCorners = (2) [(-24,-34.32,-1e-07),(24,34.32,1e-07)]
  EqualTolerance = true
  ExtensionAngle = 0
  FormatSpec = %.2w
  FormatSpecOverTolerance = %+.2w
  FormatSpecUnderTolerance = %+.2w
  Inverted = false
  LineAngle = 0
  LockPosition = false
  MeasureType = 1
  OverTolerance = 0
  References2D = -> [ProjItem002]
  Rotation = 0
  ScaleType = 0
  TheoreticalExact = false
  Type = 0
  UnderTolerance = 0
  X = 41.3941
  Y = 0
FEATURE [TechDraw::DrawViewDimension] Dimension070
  AngleOverride = false
  Arbitrary = false
  ArbitraryTolerances = false
  BoxCorners = (2) [(-24,-34.32,-1e-07),(24,34.32,1e-07)]
  EqualTolerance = true
  ExtensionAngle = 0
  FormatSpec = %.2w
  FormatSpecOverTolerance = %+.2w
  FormatSpecUnderTolerance = %+.2w
  Inverted = false
  LineAngle = 0
  LockPosition = false
  MeasureType = 1
  OverTolerance = 0
  References2D = -> [ProjItem002]
  Rotation = 0
  ScaleType = 0
  TheoreticalExact = false
  Type = 2
  UnderTolerance = 0
  X = 27.3941
  Y = -43.2782
FEATURE [TechDraw::DrawViewDimension] Dimension071
  AngleOverride = false
  Arbitrary = false
  ArbitraryTolerances = false
  BoxCorners = (2) [(-19.32,-34.32,-1e-07),(19.32,34.32,1e-07)]
  EqualTolerance = true
  ExtensionAngle = 0
  FormatSpec = %.2w
  FormatSpecOverTolerance = %+.2w
  FormatSpecUnderTolerance = %+.2w
  Inverted = false
  LineAngle = 0
  LockPosition = false
  MeasureType = 1
  OverTolerance = 0
  References2D = -> [ProjItem004]
  Rotation = 0
  ScaleType = 0
  TheoreticalExact = false
  Type = 2
  UnderTolerance = 0
  X = 29.0903
  Y = 0
FEATURE [TechDraw::DrawViewDimension] Dimension074
  AngleOverride = false
  Arbitrary = false
  ArbitraryTolerances = false
  BoxCorners = (2) [(-19.32,-24,-1e-07),(19.32,24,1e-07)]
  EqualTolerance = true
  ExtensionAngle = 0
  FormatSpec = %.2w
  FormatSpecOverTolerance = %+.2w
  FormatSpecUnderTolerance = %+.2w
  Inverted = false
  LineAngle = 0
  LockPosition = false
  MeasureType = 1
  OverTolerance = 0
  References2D = -> [ProjItem001]
  Rotation = 0
  ScaleType = 0
  TheoreticalExact = false
  Type = 0
  UnderTolerance = 0
  X = -30.4176
  Y = 0
FEATURE [TechDraw::DrawViewDimension] Dimension077
  AngleOverride = false
  Arbitrary = false
  ArbitraryTolerances = false
  BoxCorners = (2) [(-19.32,-24,-1e-07),(19.32,24,1e-07)]
  EqualTolerance = true
  ExtensionAngle = 0
  FormatSpec = %.2w
  FormatSpecOverTolerance = %+.2w
  FormatSpecUnderTolerance = %+.2w
  Inverted = false
  LineAngle = 0
  LockPosition = false
  MeasureType = 1
  OverTolerance = 0
  References2D = -> [ProjItem]
  Rotation = 0
  ScaleType = 0
  TheoreticalExact = false
  Type = 0
  UnderTolerance = 0
  X = -49.23
  Y = 5.37784
FEATURE [TechDraw::DrawViewDimension] Dimension078
  AngleOverride = false
  Arbitrary = false
  ArbitraryTolerances = false
  BoxCorners = (2) [(-19.32,-24,-1e-07),(19.32,24,1e-07)]
  EqualTolerance = true
  ExtensionAngle = 0
  FormatSpec = %.2w
  FormatSpecOverTolerance = %+.2w
  FormatSpecUnderTolerance = %+.2w
  Inverted = false
  LineAngle = 0
  LockPosition = false
  MeasureType = 1
  OverTolerance = 0
  References2D = -> [ProjItem]
  Rotation = 0
  ScaleType = 0
  TheoreticalExact = false
  Type = 0
  UnderTolerance = 0
  X = -38.9191
  Y = -32.9437
FEATURE [TechDraw::DrawViewDimension] Dimension079
  AngleOverride = false
  Arbitrary = false
  ArbitraryTolerances = false
  BoxCorners = (2) [(-19.32,-24,-1e-07),(19.32,24,1e-07)]
  EqualTolerance = true
  ExtensionAngle = 0
  FormatSpec = %.2w
  FormatSpecOverTolerance = %+.2w
  FormatSpecUnderTolerance = %+.2w
  Inverted = false
  LineAngle = 0
  LockPosition = false
  MeasureType = 1
  OverTolerance = 0
  References2D = -> [ProjItem]
  Rotation = 0
  ScaleType = 0
  TheoreticalExact = false
  Type = 0
  UnderTolerance = 0
  X = -38.9191
  Y = 0.542818
FEATURE [TechDraw::DrawViewDetail] Detail003  label="Detail 4"
  AnchorPoint = (-0.14,7.36,0)
  BaseView = -> ProjItem
  Caption = Detail 4
  CoarseView = false
  Direction = (0,0,-1)
  Focus = 100
  HardHidden = false
  IsoCount = 0
  IsoHidden = false
  IsoVisible = false
  LockPosition = false
  Perspective = false
  Radius = 10
  Reference = 4
  Rotation = 0
  Scale = 2
  ScaleType = 2
  ScrubCount = 1
  SeamHidden = false
  SeamVisible = false
  ShowHighlight = true
  ShowMatting = true
  SmoothHidden = false
  SmoothVisible = true
  Source = -> [Assembly001]
  X = 200.011
  XDirection = (1,0,0)
  Y = 47.7495
FEATURE [TechDraw::DrawViewDimension] Dimension080
  AngleOverride = false
  Arbitrary = false
  ArbitraryTolerances = false
  BoxCorners = (2) [(-20.2,-20.2,-1e-07),(20.2,20.2,1e-07)]
  EqualTolerance = true
  ExtensionAngle = 0
  FormatSpec = %.2w
  FormatSpecOverTolerance = %+.2w
  FormatSpecUnderTolerance = %+.2w
  Inverted = false
  LineAngle = 0
  LockPosition = false
  MeasureType = 1
  OverTolerance = 0
  References2D = -> [Detail003]
  Rotation = 0
  ScaleType = 0
  TheoreticalExact = false
  Type = 0
  UnderTolerance = 0
  X = 0.539986
  Y = 34.8487
FEATURE [TechDraw::DrawViewDimension] Dimension081
  AngleOverride = false
  Arbitrary = false
  ArbitraryTolerances = false
  BoxCorners = (2) [(-20.2,-20.2,-1e-07),(20.2,20.2,1e-07)]
  EqualTolerance = true
  ExtensionAngle = 0
  FormatSpec = %.2w
  FormatSpecOverTolerance = %+.2w
  FormatSpecUnderTolerance = %+.2w
  Inverted = false
  LineAngle = 0
  LockPosition = false
  MeasureType = 1
  OverTolerance = 0
  References2D = -> [Detail003]
  Rotation = 0
  ScaleType = 0
  TheoreticalExact = false
  Type = 0
  UnderTolerance = 0
  X = -31.0789
  Y = 13.0291
FEATURE [TechDraw::DrawViewDetail] Detail004  label="Detail 5"
  AnchorPoint = (-0.18,17.3,0)
  BaseView = -> View
  Caption = Detail 5
  CoarseView = false
  Direction = (0,-1,0)
  Focus = 100
  HardHidden = false
  IsoCount = 0
  IsoHidden = false
  IsoVisible = false
  LockPosition = false
  Perspective = false
  Radius = 15
  Reference = 5
  Rotation = 0
  Scale = 2
  ScaleType = 2
  ScrubCount = 1
  SeamHidden = false
  SeamVisible = false
  ShowHighlight = true
  ShowMatting = true
  SmoothHidden = false
  SmoothVisible = true
  Source = -> [Assembly001]
  X = 275.737
  XDirection = (1,0,0)
  Y = 242.104
FEATURE [TechDraw::DrawViewBalloon] Balloon004
  BubbleShape = 3
  EndType = 0
  EndTypeScale = 1
  KinkLength = 5
  LockPosition = false
  OriginX = -5.77352
  OriginY = 10.6912
  Rotation = 0
  ScaleType = 0
  ShapeScale = 1
  SourceView = -> Detail004
  Text = Status Indicator LED
  TextWrapLen = -1
  X = -22.2813
  Y = 17.4857
FEATURE [TechDraw::DrawViewBalloon] Balloon006
  BubbleShape = 3
  EndType = 0
  EndTypeScale = 1
  KinkLength = 5
  LockPosition = false
  OriginX = 0.0864149
  OriginY = -0.290252
  Rotation = 0
  ScaleType = 0
  ShapeScale = 1
  SourceView = -> Detail
  Text = Micro USB
  TextWrapLen = -1
  X = 17.1626
  Y = 8.18667
FEATURE [TechDraw::DrawViewBalloon] Balloon007
  BubbleShape = 3
  EndType = 0
  EndTypeScale = 1
  KinkLength = 5
  LockPosition = false
  OriginX = 0.241293
  OriginY = 0.349196
  Rotation = 0
  ScaleType = 0
  ShapeScale = 1
  SourceView = -> Detail002
  Text = M2x30 | ISO7046
  TextWrapLen = -1
  X = 15.716
  Y = 12.3391
FEATURE [TechDraw::DrawViewBalloon] Balloon
  BubbleShape = 3
  EndType = 0
  EndTypeScale = 1
  KinkLength = 5
  LockPosition = false
  OriginX = 6.55957
  OriginY = 11.0682
  Rotation = 0
  ScaleType = 0
  ShapeScale = 1
  SourceView = -> Detail004
  Text = Power Indicator LED
  TextWrapLen = -1
  X = 19.6649
  Y = 17.5204
FEATURE [TechDraw::DrawViewBalloon] Balloon008
  BubbleShape = 3
  EndType = 0
  EndTypeScale = 1
  KinkLength = 5
  LockPosition = false
  OriginX = 0.713959
  OriginY = 1.54593
  Rotation = 0
  ScaleType = 0
  ShapeScale = 1
  SourceView = -> Detail004
  Text = Reset Button
  TextWrapLen = -1
  X = 16.4424
  Y = 9.71282
FEATURE [TechDraw::DrawViewBalloon] Balloon009
  BubbleShape = 3
  EndType = 0
  EndTypeScale = 1
  KinkLength = 5
  LockPosition = false
  OriginX = 0.393166
  OriginY = -6.75802
  Rotation = 0
  ScaleType = 0
  ShapeScale = 1
  SourceView = -> Detail004
  Text = Power Switch
  TextWrapLen = -1
  X = 15.8903
  Y = -0.525907
FEATURE [TechDraw::DrawViewDimension] Dimension147
  AngleOverride = false
  Arbitrary = false
  ArbitraryTolerances = false
  BoxCorners = (2) [(-19.32,-14,-1e-07),(19.32,14,1e-07)]
  EqualTolerance = true
  ExtensionAngle = 0
  FormatSpec = %.2w
  FormatSpecOverTolerance = %+.2w
  FormatSpecUnderTolerance = %+.2w
  Inverted = false
  LineAngle = 0
  LockPosition = false
  MeasureType = 1
  OverTolerance = 0
  References2D = -> [SectionView004]
  Rotation = 0
  ScaleType = 0
  TheoreticalExact = false
  Type = 0
  UnderTolerance = 0
  X = 0
  Y = 28.1653
FEATURE [TechDraw::DrawViewDimension] Dimension148
  AngleOverride = false
  Arbitrary = false
  ArbitraryTolerances = false
  BoxCorners = (2) [(-19.32,-14,-1e-07),(19.32,14,1e-07)]
  EqualTolerance = true
  ExtensionAngle = 0
  FormatSpec = %.2w
  FormatSpecOverTolerance = %+.2w
  FormatSpecUnderTolerance = %+.2w
  Inverted = false
  LineAngle = 0
  LockPosition = false
  MeasureType = 1
  OverTolerance = 0
  References2D = -> [SectionView004]
  Rotation = 0
  ScaleType = 0
  TheoreticalExact = false
  Type = 0
  UnderTolerance = 0
  X = 0
  Y = 21.1653
FEATURE [TechDraw::DrawPage] Page002  label="Page_03_EnclosureAssembly_Bottom"
  KeepUpdated = true
  NextBalloonIndex = 1
  ProjectionType = 1
  Template = -> Template002
  Views = -> [RichTextAnnotation001,ProjGroup003,Dimension114,Dimension115,Dimension116,Dimension117,Dimension118,Dimension119,Dimension120,Dimension121,Dimension122,Dimension123,Dimension124,Dimension125,Dimension126,Dimension127,Dimension128,Dimension129,Dimension130,Dimension131,Dimension132,Dimension133,Dimension134,Dimension135,Dimension136,Dimension137,Dimension138,Dimension139,Dimension140,Dimension141,+9 more]
FEATURE [TechDraw::DrawViewImage] ActiveView  label="ActiveView_BackGrounded"
  Height = 74.4
  ImageFile = <userpath>/.cache/FreeCAD/Cache/FreeCAD_Doc_eeeef674-e21c-4927-bb22-0035c11630f7_30cb35_706482/PageActiveView945xdG.png
  LockPosition = false
  Rotation = 0
  ScaleType = 2
  Width = 88
  X = 361.04
  Y = 242.104
FEATURE [TechDraw::DrawViewImage] ActiveView002  label="Isometric_SensorSideGrounded"
  Height = 92.4
  ImageFile = <userpath>/.cache/FreeCAD/Cache/FreeCAD_Doc_eeeef674-e21c-4927-bb22-0035c11630f7_30cb35_706482/PageActiveView002H9jbnc.png
  LockPosition = false
  Rotation = 0
  ScaleType = 2
  Width = 61
  X = 374.47
  Y = 143.924
FEATURE [TechDraw::DrawPage] Page  label="Page_01_IoTAssembly"
  KeepUpdated = true
  NextBalloonIndex = 19
  ProjectionType = 1
  Template = -> Template
  Views = -> [ProjGroup,Dimension019,Detail,Detail001,Dimension023,Dimension028,Dimension031,Detail002,ActiveView002,ActiveView,Dimension037,Dimension038,Dimension039,Dimension040,Dimension041,Dimension,Dimension042,Dimension044,Dimension045,Dimension046,Dimension047,Dimension048,Dimension049,Dimension050,Dimension051,Dimension052,Dimension053,Dimension054,Dimension055,Dimension056,Dimension057,Dimension058,+25 more]
FEATURE [App::DocumentObjectGroup] Group  label="Blueprints"
  Group = -> [Page,Page001,Page002]
